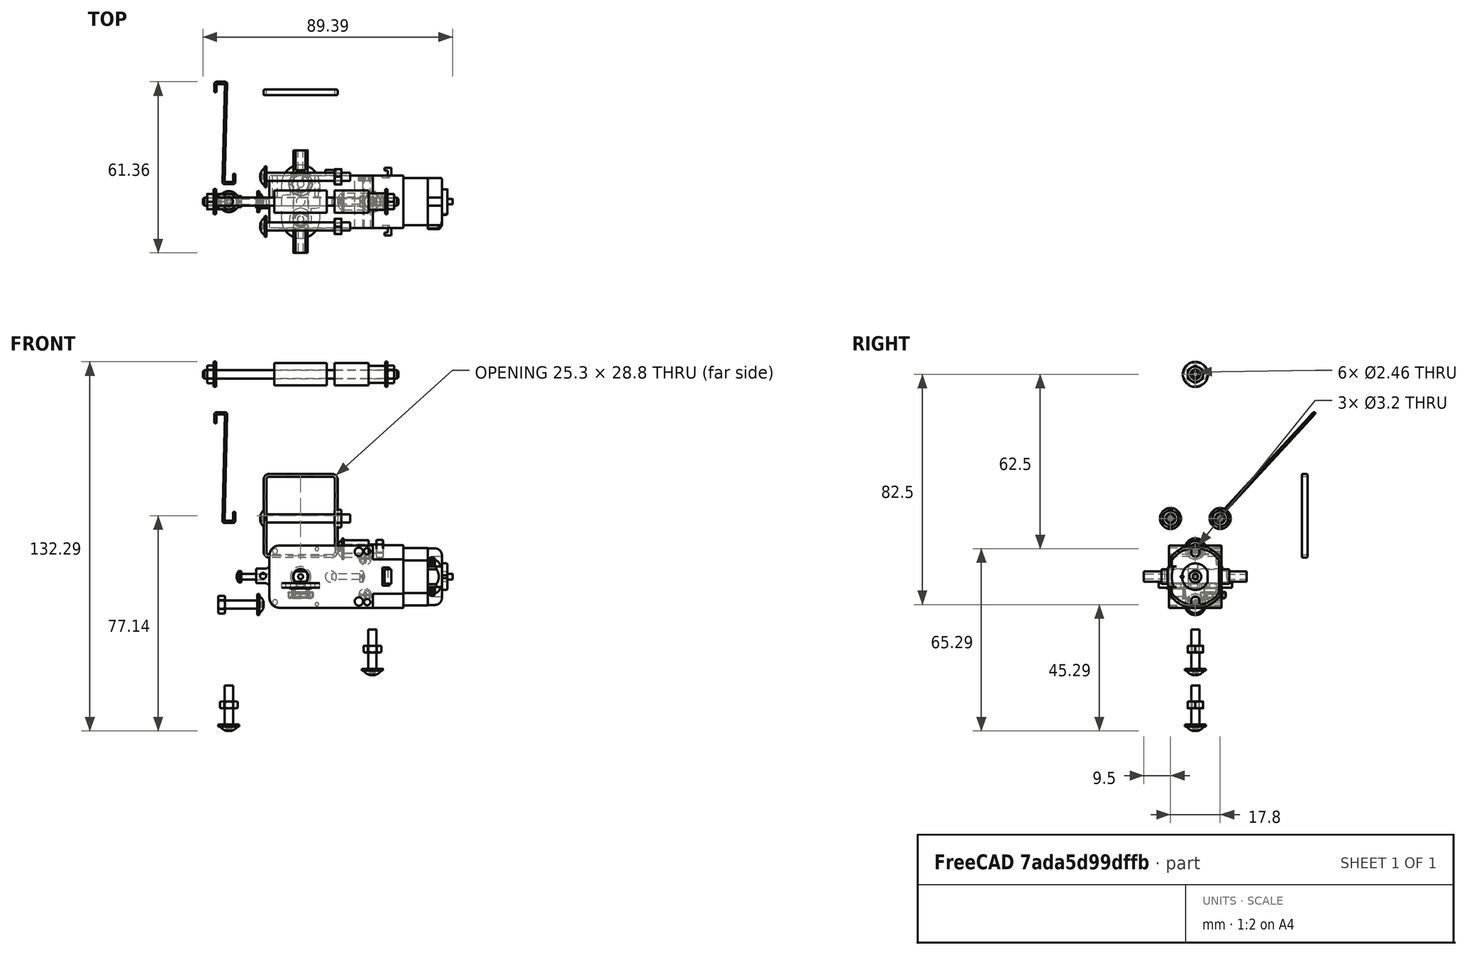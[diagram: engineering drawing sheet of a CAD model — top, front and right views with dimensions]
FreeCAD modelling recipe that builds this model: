
FCSTD DOCUMENT  (FreeCAD 0.21R33771 (Git))
Label: walking_robot_05_false_color
License: CERN Open Hardware Licence permissive
LicenseURL: https://cern-ohl.web.cern.ch/
objects: PartDesign::Body×27, PartDesign::SubShapeBinder×26, Sketcher::SketchObject×22, Part::FeaturePython×19, Part::Part2DObjectPython×19, PartDesign::Pad×15, PartDesign::FeatureBase×12, Part::Feature×10, PartDesign::Plane×7, App::DocumentObjectGroup×5, TechDraw::DrawViewDimension×5, PartDesign::FeaturePython×4, PartDesign::Fillet×3, Spreadsheet::Sheet×2, PartDesign::CoordinateSystem×2, Part::Box×2, Part::Cut×2, App::Part×2, PartDesign::Pocket×2, PartDesign::AdditivePipe×1, +4 more types
note: 199 computed .brp shape members not serialized (recipe doc carries the construction recipe); baked Part::Feature solids carry a one-line shape summary decoded from their .brp

FEATURE [Spreadsheet::Sheet] Spreadsheet
  cells = A1='acrylic_thick; B1(acrylic_thick)==4.9 mm; A2='acrylic_thin; B2(acrylic_thin)=2.8; A3='cam_length; B3(cam_length)=10; A4='angle; B4(angle)=270
FEATURE [Part::Feature] Compound002  label="motoreducteur001"
  Placement = pos=(25.85,-9.4,11.15) rot=(-1,0,0;1.5708rad)
  shape: bbox 70.34 x 38.2 x 22.5 mm, 234 faces, 3 solids (baked)
FEATURE [PartDesign::CoordinateSystem] Local_CS002
  AttacherType = Attacher::AttachEngine3D
  AttachmentOffset = pos=(0,0,0) rot=(0,-1,0;1.5708rad)
  MapMode = 11
  Placement = pos=(-2.8e-15,-19.1,1.8e-15) rot=(0,0,-1;1.5708rad)
  Support = -> [Compound002]
FEATURE [PartDesign::CoordinateSystem] Local_CS003
  AttacherType = Attacher::AttachEngine3D
  AttachmentOffset = pos=(0,0,0) rot=(0,1,0;1.5708rad)
  MapMode = 11
  Placement = pos=(-2.8e-15,19.1,1.9e-15) rot=(0,0,1;4.71239rad)
  Support = -> [Compound002]
FEATURE [PartDesign::SubShapeBinder] Binder
  BindCopyOnChange = 0
  BindMode = 0
  ClaimChildren = false
  Context = -> Body [Binder.]
  Fuse = false
  MakeFace = true
  OffsetFill = false
  OffsetIntersection = false
  OffsetJoinType = 0
  OffsetOpenResult = false
  PartialLoad = false
  Relative = true
  Support = -> [Part001]
  _Version = 2
FEATURE [Sketcher::SketchObject] Sketch
  ExternalGeometry = -> [Binder]
  FullyConstrained = true
  MapMode = 5
  Placement = pos=(-18.4,0,0) rot=(0.57735,-0.57735,-0.57735;2.0944rad)
  Support = -> [Binder]
  expr: Constraints[38] = Spreadsheet.cam_length
  expr: Constraints[81] = Spreadsheet.angle
  sketch-geometry (37):
    g0: ArcOfCircle CenterX=3.55 CenterY=5 CenterZ=0 NormalX=0 NormalY=0 NormalZ=1 AngleXU=0 Radius=0.4 StartAngle=0 EndAngle=3.14159
    g1: ArcOfCircle CenterX=3.55 CenterY=-5 CenterZ=0 NormalX=0 NormalY=0 NormalZ=1 AngleXU=0 Radius=0.4 StartAngle=3.14159 EndAngle=6.28319
    g2: LineSegment StartX=3.15 StartY=5 StartZ=0 EndX=3.15 EndY=-5 EndZ=0
    g3: LineSegment StartX=3.95 StartY=-5 StartZ=0 EndX=3.95 EndY=5 EndZ=0
    g4: ArcOfCircle CenterX=-3.55 CenterY=5 CenterZ=0 NormalX=0 NormalY=0 NormalZ=1 AngleXU=0 Radius=0.4 StartAngle=3e-16 EndAngle=3.14159
    g5: ArcOfCircle CenterX=-3.55 CenterY=-5 CenterZ=0 NormalX=0 NormalY=0 NormalZ=1 AngleXU=0 Radius=0.4 StartAngle=3.14159 EndAngle=6.28319
    g6: LineSegment StartX=-3.15 StartY=-5 StartZ=0 EndX=-3.15 EndY=5 EndZ=0
    g7: LineSegment StartX=3.55 StartY=5 StartZ=0 EndX=3.55 EndY=-5 EndZ=0
    g8: LineSegment StartX=-3.55 StartY=5 StartZ=0 EndX=-3.55 EndY=-5 EndZ=0
    g9: ArcOfCircle CenterX=1.55 CenterY=5 CenterZ=0 NormalX=0 NormalY=0 NormalZ=1 AngleXU=0 Radius=0.2 StartAngle=0 EndAngle=3.14159
    g10: ArcOfCircle CenterX=1.55 CenterY=-5 CenterZ=0 NormalX=0 NormalY=0 NormalZ=1 AngleXU=0 Radius=0.2 StartAngle=3.14159 EndAngle=6.28319
    g11: LineSegment StartX=1.35 StartY=5 StartZ=0 EndX=1.35 EndY=2.16333 EndZ=0
    g12: LineSegment StartX=1.75 StartY=-5 StartZ=0 EndX=1.75 EndY=5 EndZ=0
    g13: ArcOfCircle CenterX=-1.55 CenterY=5 CenterZ=0 NormalX=0 NormalY=0 NormalZ=1 AngleXU=0 Radius=0.2 StartAngle=5e-16 EndAngle=3.14159
    g14: ArcOfCircle CenterX=-1.55 CenterY=-5 CenterZ=0 NormalX=0 NormalY=0 NormalZ=1 AngleXU=0 Radius=0.2 StartAngle=3.14159 EndAngle=6.28319
    g15: LineSegment StartX=-1.75 StartY=5 StartZ=0 EndX=-1.75 EndY=-5 EndZ=0
    g16: LineSegment StartX=-1.35 StartY=-5 StartZ=0 EndX=-1.35 EndY=-2.16333 EndZ=0
    g17: LineSegment StartX=1.55 StartY=5 StartZ=0 EndX=1.55 EndY=-5 EndZ=0
    g18: LineSegment StartX=-1.55 StartY=5 StartZ=0 EndX=-1.55 EndY=-5 EndZ=0
    g19: LineSegment StartX=3.55 StartY=-4.2e-15 StartZ=0 EndX=1.55 EndY=-3.8e-15 EndZ=0
    g20: ArcOfCircle CenterX=9.6e-15 CenterY=5 CenterZ=0 NormalX=0 NormalY=0 NormalZ=1 AngleXU=0 Radius=7.5 StartAngle=0 EndAngle=3.14159
    g21: ArcOfCircle CenterX=6.9e-15 CenterY=-10 CenterZ=0 NormalX=0 NormalY=0 NormalZ=1 AngleXU=0 Radius=7.5 StartAngle=3.14159 EndAngle=6.28319
    g22: LineSegment StartX=-7.5 StartY=5 StartZ=0 EndX=-7.5 EndY=-10 EndZ=0
    g23: LineSegment StartX=7.5 StartY=-10 StartZ=0 EndX=7.5 EndY=5 EndZ=0
    g24: LineSegment StartX=8.7e-15 StartY=-3.6e-15 StartZ=0 EndX=9.6e-15 EndY=5 EndZ=0
    g25: LineSegment StartX=8.7e-15 StartY=-3.6e-15 StartZ=0 EndX=6.9e-15 EndY=-10 EndZ=0
    g26: Circle CenterX=6.9e-15 CenterY=-10 CenterZ=0 NormalX=0 NormalY=0 NormalZ=1 AngleXU=0 Radius=3.1
    g27: LineSegment StartX=-3.95 StartY=-5 StartZ=0 EndX=-3.95 EndY=5 EndZ=0
    g28: LineSegment StartX=1.55 StartY=-3.8e-15 StartZ=0 EndX=8.7e-15 EndY=-3.6e-15 EndZ=0
    g29: Circle CenterX=8.7e-15 CenterY=-3.6e-15 CenterZ=0 NormalX=0 NormalY=0 NormalZ=1 AngleXU=0 Radius=1.75
    g30: LineSegment StartX=-1.75 StartY=-4.1e-15 StartZ=0 EndX=-1.85 EndY=-4.1e-15 EndZ=0
    g31: LineSegment StartX=-3.55 StartY=-2.9e-15 StartZ=0 EndX=-1.55 EndY=-3.3e-15 EndZ=0
    g32: LineSegment StartX=8.7e-15 StartY=-3.6e-15 StartZ=0 EndX=-1.55 EndY=-3.3e-15 EndZ=0
    g33: LineSegment StartX=-1.35 StartY=2.16333 StartZ=0 EndX=-1.35 EndY=5 EndZ=0
    g34: LineSegment StartX=1.35 StartY=-2.16333 StartZ=0 EndX=1.35 EndY=-5 EndZ=0
    g35: ArcOfCircle CenterX=8.7e-15 CenterY=-3.6e-15 CenterZ=0 NormalX=0 NormalY=0 NormalZ=1 AngleXU=0 Radius=2.55 StartAngle=1.01289 EndAngle=2.1287
    g36: ArcOfCircle CenterX=8.7e-15 CenterY=-3.6e-15 CenterZ=0 NormalX=0 NormalY=0 NormalZ=1 AngleXU=0 Radius=2.55 StartAngle=4.15448 EndAngle=5.2703
  constraints (89):
    c: Tangent(g0,g2) = -1.5708
    c: Tangent(g2,g1) = -1.5708
    c: Tangent(g1,g3) = -1.5708
    c: Tangent(g5,g6) = -1.5708
    c: Tangent(g6,g4) = -1.5708
    c: Radius(g0) = 0.4
    c: Coincident(g7,g0)
    c: Coincident(g7,g1)
    c: Coincident(g8,g4)
    c: Coincident(g8,g5)
    c: Equal(g7,g8)
    c: Distance(g7) = 10
    c: Tangent(g9,g11) = -1.5708
    c: Tangent(g10,g12) = -1.5708
    c: Tangent(g12,g9) = -1.5708
    c: Tangent(g13,g15) = -1.5708
    c: Tangent(g15,g14) = -1.5708
    c: Tangent(g14,g16) = -1.5708
    c: Coincident(g17,g9)
    c: Coincident(g17,g10)
    c: Coincident(g18,g13)
    c: Coincident(g18,g14)
    c: Equal(g17,g7)
    c: Equal(g8,g18)
    c: Symmetric(g10,g9,g19)
    c: Distance(g19) = 2
    c: Perpendicular(g7,g19)
    c: Parallel(g17,g7)
    c: Parallel(g18,g8)
    c: Tangent(g20,g22) = -1.5708
    c: Tangent(g22,g21) = -1.5708
    c: Tangent(g21,g23) = -1.5708
    c: Tangent(g23,g20) = -1.5708
    c: Equal(g20,g21)
    c: Coincident(g24,g20)
    c: Coincident(g25,g21)
    c: Diameter(g20) = 15
    c: Distance(g24) = 5
    c: Distance(g25) = 10
    c: Coincident(g26,g21)
    c: Diameter(g26) = 6.2
    c: Tangent(g27,g4) = 1.5708
    c: Tangent(g27,g5) = 1.5708
    c: Symmetric(g0,g1,g19)
    c: Coincident(g28,g19)
    c: Parallel(g28,g19)
    c: Perpendicular(g28,g24)
    c: Tangent(g0,g3) = -1.5708
    c: PointOnObject(g30,g29)
    c: Horizontal(g30)
    c: Symmetric(g-5,g-5,g30)
    c: DistanceX(g30,g30) = 0.1
    c: Perpendicular(g25,g28)
    c: Symmetric(g14,g13,g31)
    c: Symmetric(g5,g4,g31)
    c: Equal(g31,g19)
    c: Coincident(g32,g31)
    c: Equal(g28,g32)
    c: Perpendicular(g32,g24)
    c: Perpendicular(g32,g18)
    c: Perpendicular(g18,g31)
    c: Tangent(g15,g29)
    c: PointOnObject(g34,g11)
    c: PointOnObject(g33,g-3)
    c: Parallel(g33,g17)
    c: Parallel(g17,g34)
    c: Tangent(g33,g13) = -1.5708
    c: Tangent(g34,g10) = -1.5708
    c: Coincident(g25,g32)
    c: Coincident(g25,g24)
    c: Coincident(g25,g28)
    c: Coincident(g24,g29)
    c: Coincident(g35,g24)
    c: Coincident(g35,g33)
    c: Coincident(g35,g11)
    c: Coincident(g36,g35)
    c: Coincident(g36,g34)
    c: Equal(g36,g-4)
    c: Coincident(g16,g36)
    c: Parallel(g16,g18)
    c: Coincident(g35,g-4)
    c: Angle(g25) = 4.71239
    c: Equal(g5,g1)
    c: Equal(g1,g4)
    c: Equal(g4,g0)
    c: Equal(g13,g9)
    c: Equal(g9,g14)
    c: Equal(g14,g10)
    c: Radius(g9) = 0.2
FEATURE [PartDesign::SubShapeBinder] Binder001
  BindCopyOnChange = 0
  BindMode = 0
  ClaimChildren = false
  Context = -> Body002 [Binder001.]
  Fuse = false
  MakeFace = true
  OffsetFill = false
  OffsetIntersection = false
  OffsetJoinType = 0
  OffsetOpenResult = false
  PartialLoad = false
  Relative = true
  Support = -> [Part001]
  _Version = 2
FEATURE [Part::Box] Box  label="Cube"
  AttacherType = Attacher::AttachEngine3D
  Height = 10
  Length = 10
  Placement = pos=(-5,18.4,-5) rot=(0,0,1;0rad)
  Width = 10
FEATURE [Part::Box] Box001  label="Cube001"
  AttacherType = Attacher::AttachEngine3D
  Height = 10
  Length = 10
  Placement = pos=(-5,-28.4,-5) rot=(0,0,1;0rad)
  Width = 10
FEATURE [Part::Cut] Cut
  Base = -> Compound002
  Tool = -> Box
FEATURE [Part::Cut] Cut001
  Base = -> Cut
  Tool = -> Box001
FEATURE [App::Part] Part001  label="Motor"
  Group = -> [Box001,Compound002,Local_CS002,Local_CS003,Box,Cut,Cut001]
  Origin = -> Origin004
  Placement = pos=(0,0,0) rot=(-0.57735,0.57735,-0.57735;4.18879rad)
FEATURE [PartDesign::Pad] Pad
  Direction = (-1,2e-16,-2e-16)
  Length = 2.8
  Length2 = 10
  Profile = -> Sketch
  ReferenceAxis = -> Sketch [N_Axis]
  Reversed = true
  Type = 0
  expr: Length = Spreadsheet.acrylic_thin
FEATURE [PartDesign::Body] Body  label="cam_right_1"
  Group = -> [Sketch,Binder,Pad]
  Origin = -> Origin001
  Tip = -> Pad
FEATURE [PartDesign::SubShapeBinder] Binder002
  BindCopyOnChange = 0
  BindMode = 0
  ClaimChildren = false
  Context = -> Body003 [Binder002.]
  Fuse = false
  MakeFace = true
  OffsetFill = false
  OffsetIntersection = false
  OffsetJoinType = 0
  OffsetOpenResult = false
  PartialLoad = false
  Relative = true
  Support = -> [Body]
  _Version = 2
FEATURE [PartDesign::Plane] DatumPlane001
  AttachmentOffset = pos=(0,0,0.1) rot=(0,0,1;0rad)
  Length = 60
  MapMode = 5
  Placement = pos=(-18.5,5.2e-15,-3.9e-15) rot=(-0.57735,0.57735,0.57735;4.18879rad)
  ResizeMode = 0
  Support = -> [Binder002]
  Width = 60
FEATURE [Sketcher::SketchObject] Sketch002
  ExternalGeometry = -> [Binder002]
  FullyConstrained = true
  MapMode = 5
  Placement = pos=(-18.5,5.2e-15,-3.9e-15) rot=(-0.57735,0.57735,0.57735;4.18879rad)
  Support = -> [DatumPlane001]
  sketch-geometry (6):
    g0: ArcOfCircle CenterX=-1.6948e-12 CenterY=5 CenterZ=0 NormalX=0 NormalY=0 NormalZ=1 AngleXU=0 Radius=7.5 StartAngle=2.58e-13 EndAngle=3.14159
    g1: ArcOfCircle CenterX=2.174e-12 CenterY=-10 CenterZ=0 NormalX=0 NormalY=0 NormalZ=1 AngleXU=0 Radius=7.5 StartAngle=3.14159 EndAngle=6.28319
    g2: LineSegment StartX=-7.5 StartY=5 StartZ=0 EndX=-7.5 EndY=-10 EndZ=0
    g3: LineSegment StartX=7.5 StartY=-10 StartZ=0 EndX=7.5 EndY=5 EndZ=0
    g4: Circle CenterX=2.174e-12 CenterY=-10 CenterZ=0 NormalX=0 NormalY=0 NormalZ=1 AngleXU=0 Radius=3.1
    g5: Circle CenterX=0 CenterY=0 CenterZ=0 NormalX=0 NormalY=0 NormalZ=1 AngleXU=0 Radius=1
  constraints (12):
    c: Tangent(g0,g2) = -1.5708
    c: Tangent(g2,g1) = -1.5708
    c: Tangent(g1,g3) = -1.5708
    c: Tangent(g3,g0) = -1.5708
    c: Equal(g0,g1)
    c: Coincident(g0,g-3)
    c: Coincident(g1,g-5)
    c: Equal(g0,g-3)
    c: Coincident(g4,g1)
    c: Equal(g4,g-5)
    c: Coincident(g5,g-6)
    c: Diameter(g5) = 2
FEATURE [PartDesign::Pad] Pad002
  Direction = (-1,2e-16,-2e-16)
  Length = 2.8
  Length2 = 10
  Placement = pos=(-18.5,5e-15,-4e-15) rot=(0.57735,-0.57735,-0.57735;2.0944rad)
  Profile = -> Sketch002
  ReferenceAxis = -> Sketch002 [N_Axis]
  Type = 0
  expr: Length = Spreadsheet.acrylic_thin
FEATURE [PartDesign::Body] Body003  label="cam_right_2"
  Group = -> [Binder002,DatumPlane001,Sketch002,Pad002]
  Origin = -> Origin
  Tip = -> Pad002
FEATURE [PartDesign::SubShapeBinder] Binder003
  BindCopyOnChange = 0
  BindMode = 0
  ClaimChildren = false
  Context = -> Body004 [Binder003.]
  Fuse = false
  MakeFace = true
  OffsetFill = false
  OffsetIntersection = false
  OffsetJoinType = 0
  OffsetOpenResult = false
  PartialLoad = false
  Relative = true
  Support = -> [Body003]
  _Version = 2
FEATURE [PartDesign::Plane] DatumPlane002
  AttachmentOffset = pos=(0,0,0.1) rot=(0,0,1;0rad)
  Length = 60
  MapMode = 5
  Placement = pos=(-21.4,5.3e-15,-1.05e-14) rot=(-0.57735,0.57735,0.57735;4.18879rad)
  ResizeMode = 0
  Support = -> [Binder003]
  Width = 60
FEATURE [Sketcher::SketchObject] Sketch003
  ExternalGeometry = -> [Binder003]
  FullyConstrained = true
  MapMode = 5
  Placement = pos=(-21.4,5.3e-15,-1.05e-14) rot=(-0.57735,0.57735,0.57735;4.18879rad)
  Support = -> [DatumPlane002]
  sketch-geometry (6):
    g0: ArcOfCircle CenterX=-1.6956e-12 CenterY=5 CenterZ=0 NormalX=0 NormalY=0 NormalZ=1 AngleXU=0 Radius=7.5 StartAngle=2.581e-13 EndAngle=3.14159
    g1: ArcOfCircle CenterX=2.1765e-12 CenterY=-10 CenterZ=0 NormalX=0 NormalY=0 NormalZ=1 AngleXU=0 Radius=7.5 StartAngle=3.14159 EndAngle=6.28319
    g2: LineSegment StartX=-7.5 StartY=5 StartZ=0 EndX=-7.5 EndY=-10 EndZ=0
    g3: LineSegment StartX=7.5 StartY=-10 StartZ=0 EndX=7.5 EndY=5 EndZ=0
    g4: Circle CenterX=2.1765e-12 CenterY=-10 CenterZ=0 NormalX=0 NormalY=0 NormalZ=1 AngleXU=0 Radius=3.1
    g5: Circle CenterX=0 CenterY=0 CenterZ=0 NormalX=0 NormalY=0 NormalZ=1 AngleXU=0 Radius=3
  constraints (12):
    c: Tangent(g0,g2) = -1.5708
    c: Tangent(g2,g1) = -1.5708
    c: Tangent(g1,g3) = -1.5708
    c: Tangent(g3,g0) = -1.5708
    c: Equal(g0,g1)
    c: Coincident(g0,g-3)
    c: Coincident(g1,g-5)
    c: Equal(g0,g-3)
    c: Coincident(g4,g1)
    c: Equal(g4,g-5)
    c: Coincident(g5,g-6)
    c: Diameter(g5) = 6
FEATURE [PartDesign::Pad] Pad003
  Direction = (-1,3e-16,-3e-16)
  Length = 2.8
  Length2 = 10
  Placement = pos=(-21.4,5e-15,-1e-14) rot=(0.57735,-0.57735,-0.57735;2.0944rad)
  Profile = -> Sketch003
  ReferenceAxis = -> Sketch003 [N_Axis]
  Type = 0
  expr: Length = Spreadsheet.acrylic_thin
FEATURE [PartDesign::Body] Body004  label="cam_right_3"
  Group = -> [Binder003,DatumPlane002,Sketch003,Pad003]
  Origin = -> Origin005
  Tip = -> Pad003
FEATURE [PartDesign::SubShapeBinder] Binder004
  BindCopyOnChange = 0
  BindMode = 0
  ClaimChildren = false
  Context = -> Body002 [Binder004.]
  Fuse = false
  MakeFace = true
  OffsetFill = false
  OffsetIntersection = false
  OffsetJoinType = 0
  OffsetOpenResult = false
  PartialLoad = false
  Relative = true
  Support = -> [Body004]
  _Version = 2
FEATURE [PartDesign::Plane] DatumPlane003
  AttachmentOffset = pos=(0,0,0.1) rot=(0,0,1;0rad)
  Length = 66.5529
  MapMode = 5
  Placement = pos=(-24.3,8.3e-15,-1.41e-14) rot=(-0.57735,0.57735,0.57735;4.18879rad)
  ResizeMode = 0
  Support = -> [Binder004]
  Width = 153.553
FEATURE [Sketcher::SketchObject] Sketch001
  ExternalGeometry = -> [Binder004]
  FullyConstrained = false
  MapMode = 5
  Placement = pos=(-24.3,8.3e-15,-1.41e-14) rot=(-0.57735,0.57735,0.57735;4.18879rad)
  Support = -> [DatumPlane003]
  expr: Constraints[92] = Spreadsheet.angle
  expr: Constraints[98] = Spreadsheet.acrylic_thin
  sketch-geometry (38):
    g0: LineSegment StartX=-10 StartY=84 StartZ=0 EndX=10 EndY=84 EndZ=0
    g1: LineSegment StartX=10 StartY=84 StartZ=0 EndX=10 EndY=-53 EndZ=0
    g2: LineSegment StartX=10 StartY=-53 StartZ=0 EndX=-10 EndY=-53 EndZ=0
    g3: LineSegment StartX=-10 StartY=-53 StartZ=0 EndX=-10 EndY=84 EndZ=0
    g4: LineSegment StartX=4e-15 StartY=-10 StartZ=0 EndX=-10 EndY=-10 EndZ=0
    g5: LineSegment StartX=4e-15 StartY=-10 StartZ=0 EndX=10 EndY=-10 EndZ=0
    g6: ArcOfCircle CenterX=-2e-16 CenterY=75 CenterZ=0 NormalX=0 NormalY=0 NormalZ=1 AngleXU=0 Radius=3.1 StartAngle=2e-16 EndAngle=3.14159
    g7: ArcOfCircle CenterX=6e-16 CenterY=50 CenterZ=0 NormalX=0 NormalY=0 NormalZ=1 AngleXU=0 Radius=3.1 StartAngle=3.14159 EndAngle=6.28319
    g8: LineSegment StartX=-3.1 StartY=75 StartZ=0 EndX=-3.1 EndY=50 EndZ=0
    g9: LineSegment StartX=3.1 StartY=50 StartZ=0 EndX=3.1 EndY=75 EndZ=0
    g10: LineSegment StartX=-2e-16 StartY=75 StartZ=0 EndX=-4e-16 EndY=84 EndZ=0
    g11: Circle CenterX=4e-15 CenterY=-10 CenterZ=0 NormalX=0 NormalY=0 NormalZ=1 AngleXU=0 Radius=1.55
    g12: LineSegment StartX=0 StartY=0 StartZ=0 EndX=4e-15 EndY=-10 EndZ=0
    g13: Circle CenterX=0 CenterY=71 CenterZ=0 NormalX=0 NormalY=0 NormalZ=1 AngleXU=0 Radius=3.1
    g14: LineSegment StartX=0 StartY=71 StartZ=0 EndX=0 EndY=0 EndZ=0
    g15: LineSegment StartX=6e-16 StartY=50 StartZ=0 EndX=1e-16 EndY=62.5 EndZ=0
    g16: LineSegment StartX=-2e-16 StartY=75 StartZ=0 EndX=1e-16 EndY=62.5 EndZ=0
    g17: LineSegment StartX=-10 StartY=-53 StartZ=0 EndX=-6 EndY=-53 EndZ=0
    g18: LineSegment StartX=-6 StartY=-53 StartZ=0 EndX=-6 EndY=-50.2 EndZ=0
    g19: LineSegment StartX=-6 StartY=-50.2 StartZ=0 EndX=-1.25 EndY=-50.2 EndZ=0
    g20: LineSegment StartX=-1.25 StartY=-50.2 StartZ=0 EndX=-1.25 EndY=-47.2 EndZ=0
    g21: LineSegment StartX=-1.25 StartY=-47.2 StartZ=0 EndX=-2.75 EndY=-47.2 EndZ=0
    g22: LineSegment StartX=-2.75 StartY=-47.2 StartZ=0 EndX=-2.75 EndY=-44.7 EndZ=0
    g23: LineSegment StartX=-2.75 StartY=-44.7 StartZ=0 EndX=-1.25 EndY=-44.7 EndZ=0
    g24: LineSegment StartX=-1.25 StartY=-44.7 StartZ=0 EndX=-1.25 EndY=-37.7 EndZ=0
    g25: LineSegment StartX=-1.25 StartY=-37.7 StartZ=0 EndX=1.25 EndY=-37.7 EndZ=0
    g26: LineSegment StartX=1.25 StartY=-37.7 StartZ=0 EndX=1.25 EndY=-44.7 EndZ=0
    g27: LineSegment StartX=1.25 StartY=-44.7 StartZ=0 EndX=2.75 EndY=-44.7 EndZ=0
    g28: LineSegment StartX=2.75 StartY=-44.7 StartZ=0 EndX=2.75 EndY=-47.2 EndZ=0
    g29: LineSegment StartX=2.75 StartY=-47.2 StartZ=0 EndX=1.25 EndY=-47.2 EndZ=0
    g30: LineSegment StartX=1.25 StartY=-47.2 StartZ=0 EndX=1.25 EndY=-50.2 EndZ=0
    g31: LineSegment StartX=1.25 StartY=-50.2 StartZ=0 EndX=6 EndY=-50.2 EndZ=0
    g32: LineSegment StartX=6 StartY=-50.2 StartZ=0 EndX=6 EndY=-53 EndZ=0
    g33: LineSegment StartX=6 StartY=-53 StartZ=0 EndX=10 EndY=-53 EndZ=0
    g34: LineSegment StartX=-7 StartY=-10 StartZ=0 EndX=-7 EndY=20 EndZ=0
    g35: LineSegment StartX=7 StartY=20 StartZ=0 EndX=7 EndY=-10 EndZ=0
    g36: Circle CenterX=-7 CenterY=20 CenterZ=0 NormalX=0 NormalY=0 NormalZ=1 AngleXU=0 Radius=0.6
    g37: Circle CenterX=7 CenterY=20 CenterZ=0 NormalX=0 NormalY=0 NormalZ=1 AngleXU=0 Radius=0.6
  constraints (105):
    c: Coincident(g0,g1)
    c: Coincident(g1,g2)
    c: Coincident(g2,g3)
    c: Coincident(g3,g0)
    c: Distance(g0) = 20
    c: Perpendicular(g3,g0)
    c: Perpendicular(g1,g2)
    c: Perpendicular(g2,g3)
    c: PointOnObject(g4,g3)
    c: PointOnObject(g5,g1)
    c: Perpendicular(g1,g5)
    c: Perpendicular(g3,g4)
    c: Equal(g4,g5)
    c: Distance(g3) = 137
    c: Tangent(g6,g8) = -1.5708
    c: Tangent(g8,g7) = -1.5708
    c: Tangent(g7,g9) = -1.5708
    c: Tangent(g9,g6) = -1.5708
    c: Equal(g6,g7)
    c: Diameter(g7) = 6.2
    c: Distance(g6,g7) = 25
    c: Coincident(g10,g6)
    c: Perpendicular(g0,g10)
    c: Distance(g10) = 9
    c: Symmetric(g0,g0,g10)
    c: Parallel(g8,g3)
    c: Diameter(g11) = 3.1
    c: Coincident(g14,g13)
    c: DistanceY(g14,g14) = 71
    c: Coincident(g14,g12)
    c: Coincident(g15,g7)
    c: Coincident(g16,g6)
    c: Coincident(g16,g15)
    c: Equal(g16,g15)
    c: Parallel(g16,g8)
    c: Tangent(g13,g9)
    c: Vertical(g14)
    c: Coincident(g17,g3)
    c: Coincident(g17,g18)
    c: Coincident(g18,g19)
    c: Coincident(g19,g20)
    c: Coincident(g20,g21)
    c: Coincident(g21,g22)
    c: Coincident(g22,g23)
    c: Coincident(g23,g24)
    c: Coincident(g24,g25)
    c: Coincident(g25,g26)
    c: Coincident(g26,g27)
    c: Coincident(g27,g28)
    c: Coincident(g28,g29)
    c: Coincident(g29,g30)
    c: Coincident(g30,g31)
    c: Coincident(g31,g32)
    c: Coincident(g32,g33)
    c: Coincident(g33,g1)
    c: Perpendicular(g17,g3)
    c: Perpendicular(g33,g1)
    c: Perpendicular(g32,g33)
    c: Perpendicular(g17,g18)
    c: Perpendicular(g19,g18)
    c: Perpendicular(g32,g31)
    c: Perpendicular(g31,g30)
    c: Perpendicular(g19,g20)
    c: Perpendicular(g29,g30)
    c: Perpendicular(g20,g21)
    c: Perpendicular(g28,g29)
    c: Perpendicular(g22,g21)
    c: Perpendicular(g28,g27)
    c: Perpendicular(g23,g22)
    c: Perpendicular(g27,g26)
    c: Perpendicular(g24,g23)
    c: Equal(g18,g32)
    c: Equal(g30,g20)
    c: Equal(g29,g21)
    c: Equal(g23,g27)
    c: Equal(g19,g31)
    c: Distance(g22,g27) = 5.5
    c: Equal(g25,g22)
    c: Equal(g22,g28)
    c: Distance(g24) = 7
    c: Perpendicular(g25,g26)
    c: Equal(g21,g23)
    c: PointOnObject(g34,g4)
    c: Equal(g34,g35)
    c: Distance(g34,g4) = 3
    c: Coincident(g36,g34)
    c: Coincident(g37,g35)
    c: Equal(g37,g36)
    c: Diameter(g37) = 1.2
    c: Distance(g34) = 30
    c: Perpendicular(g5,g35)
    c: Perpendicular(g4,g34)
    c: Angle(g12) = 4.71239
    c: Equal(g17,g33)
    c: Distance(g17) = 4
    c: DistanceY(g3,g12) = 53
    c: Coincident(g12,g-1)
    c: DistanceY(g22,g22) = 2.5
    c: DistanceY(g18,g18) = 2.8
    c: DistanceY(g20,g20) = 3
    c: Equal(g7,g13)
    c: Coincident(g4,g5)
    c: Coincident(g4,g12)
    c: Coincident(g4,g-3)
    c: Coincident(g4,g11)
FEATURE [PartDesign::Pad] Pad004
  Direction = (-1,5e-16,-5e-16)
  Length = 2.8
  Length2 = 10
  Placement = pos=(-24.3,8e-15,-1.4e-14) rot=(0.57735,-0.57735,-0.57735;2.0944rad)
  Profile = -> Sketch001
  ReferenceAxis = -> Sketch001 [N_Axis]
  Type = 0
  expr: Length = Spreadsheet.acrylic_thin
FEATURE [PartDesign::SubShapeBinder] Binder005
  BindCopyOnChange = 0
  BindMode = 0
  ClaimChildren = false
  Context = -> Body005 [Binder005.]
  Fuse = false
  MakeFace = true
  OffsetFill = false
  OffsetIntersection = false
  OffsetJoinType = 0
  OffsetOpenResult = false
  PartialLoad = false
  Relative = true
  Support = -> [Body004]
  _Version = 2
FEATURE [Part::FeaturePython] Screw  label="M3x14-Screw"  # Fasteners workbench fastener (typed FeaturePython)
  Placement = pos=(-15.5,7.6099e-12,-10) rot=(0,1,0;1.5708rad)
  diameter = 1
  invert = false
  leftHanded = false
  length = 6
  lengthCustom = 14
  matchOuter = false
  offset = 0
  thread = false
  type = 25
FEATURE [Part::FeaturePython] Nut  label="M3-Nut"  # Fasteners workbench fastener (typed FeaturePython)
  Placement = pos=(-29.5,7.6239e-12,-10) rot=(0,1,0;1.5708rad)
  baseObject = -> Screw [Edge71]
  diameter = 4
  invert = false
  leftHanded = false
  matchOuter = false
  offset = 0
  thread = false
  type = 25
FEATURE [PartDesign::SubShapeBinder] Binder008
  BindCopyOnChange = 0
  BindMode = 0
  ClaimChildren = false
  Context = -> Body005 [Binder008.]
  Fuse = false
  MakeFace = true
  OffsetFill = false
  OffsetIntersection = false
  OffsetJoinType = 0
  OffsetOpenResult = false
  PartialLoad = false
  Relative = true
  Support = -> [Body002[Pad004.]]
  _Version = 2
FEATURE [Sketcher::SketchObject] Sketch004
  ExternalGeometry = -> [Binder005]
  FullyConstrained = true
  MapMode = 5
  Placement = pos=(-24.3,-1.36e-14,-3.65e-14) rot=(0.57735,0.57735,0.57735;2.0944rad)
  Support = -> [Binder008]
  sketch-geometry (2):
    g0: Circle CenterX=-2.172e-12 CenterY=-10 CenterZ=0 NormalX=0 NormalY=0 NormalZ=1 AngleXU=0 Radius=3
    g1: Circle CenterX=-2.172e-12 CenterY=-10 CenterZ=0 NormalX=0 NormalY=0 NormalZ=1 AngleXU=0 Radius=1.6
  constraints (4):
    c: Diameter(g1) = 3.2
    c: Diameter(g0) = 6
    c: Coincident(g1,g-3)
    c: Coincident(g0,g1)
FEATURE [PartDesign::Pad] Pad005
  Direction = (1,0,4e-16)
  Length = 8.8
  Length2 = 10
  Profile = -> Sketch004
  ReferenceAxis = -> Sketch004 [N_Axis]
  Type = 0
FEATURE [PartDesign::Body] Body005  label="spacer_right"
  Group = -> [Binder005,Sketch004,Pad005,Binder008]
  Origin = -> Origin006
  Tip = -> Pad005
FEATURE [PartDesign::SubShapeBinder] Binder009
  BindCopyOnChange = 0
  BindMode = 0
  ClaimChildren = false
  Context = -> Body007 [Binder009.]
  Fuse = false
  MakeFace = true
  OffsetFill = false
  OffsetIntersection = false
  OffsetJoinType = 0
  OffsetOpenResult = false
  PartialLoad = false
  Relative = true
  Support = -> [Body002[Pad004.]]
  _Version = 2
FEATURE [PartDesign::Plane] DatumPlane
  Length = 74.3266
  MapMode = 5
  Placement = pos=(5.3e-14,-1.145e-13,-53) rot=(1,0,0;3.14159rad)
  ResizeMode = 0
  Support = -> [Binder009]
  Width = 119.627
FEATURE [Sketcher::SketchObject] Sketch006
  ExternalGeometry = -> [Binder009]
  FullyConstrained = true
  MapMode = 5
  Placement = pos=(5.3e-14,-1.145e-13,-53) rot=(0,0,1;3.14159rad)
  Support = -> [DatumPlane]
  sketch-geometry (51):
    g0: LineSegment StartX=-12.3 StartY=40 StartZ=0 EndX=25.7 EndY=40 EndZ=0
    g1: LineSegment StartX=25.7 StartY=40 StartZ=0 EndX=25.7 EndY=0 EndZ=0
    g2: LineSegment StartX=25.7 StartY=0 StartZ=0 EndX=25.7 EndY=-56 EndZ=0
    g3: LineSegment StartX=25.7 StartY=-56 StartZ=0 EndX=-12.3 EndY=-56 EndZ=0
    g4: ArcOfCircle CenterX=-12.3 CenterY=40 CenterZ=0 NormalX=0 NormalY=0 NormalZ=1 AngleXU=0 Radius=4 StartAngle=1.5708 EndAngle=4.71239
    g5: ArcOfCircle CenterX=-12.3 CenterY=-56 CenterZ=0 NormalX=0 NormalY=0 NormalZ=1 AngleXU=0 Radius=4 StartAngle=1.5708 EndAngle=4.71239
    g6: LineSegment StartX=-12.3 StartY=44 StartZ=0 EndX=25.7 EndY=44 EndZ=0
    g7: LineSegment StartX=-12.3 StartY=36 StartZ=0 EndX=15.7 EndY=36 EndZ=0
    g8: LineSegment StartX=-12.3 StartY=-52 StartZ=0 EndX=15.7 EndY=-52 EndZ=0
    g9: LineSegment StartX=-12.3 StartY=-60 StartZ=0 EndX=25.7 EndY=-60 EndZ=0
    g10: ArcOfCircle CenterX=25.7 CenterY=10.1 CenterZ=0 NormalX=0 NormalY=0 NormalZ=1 AngleXU=0 Radius=8 StartAngle=0 EndAngle=0.895665
    g11: ArcOfCircle CenterX=25.7 CenterY=-9.9 CenterZ=0 NormalX=0 NormalY=0 NormalZ=1 AngleXU=0 Radius=8 StartAngle=3.14159 EndAngle=4.03726
    g12: LineSegment StartX=17.7 StartY=10.1 StartZ=0 EndX=17.7 EndY=-9.9 EndZ=0
    g13: LineSegment StartX=33.7 StartY=-9.9 StartZ=0 EndX=33.7 EndY=10.1 EndZ=0
    g14: LineSegment StartX=20.7 StartY=31 StartZ=0 EndX=20.7 EndY=16.345 EndZ=0
    g15: LineSegment StartX=30.7 StartY=16.345 StartZ=0 EndX=30.7 EndY=39 EndZ=0
    g16: ArcOfCircle CenterX=25.7 CenterY=39 CenterZ=0 NormalX=0 NormalY=0 NormalZ=1 AngleXU=0 Radius=5 StartAngle=0 EndAngle=1.5708
    g17: LineSegment StartX=20.7 StartY=-47 StartZ=0 EndX=20.7 EndY=-16.145 EndZ=0
    g18: LineSegment StartX=30.7 StartY=-16.145 StartZ=0 EndX=30.7 EndY=-55 EndZ=0
    g19: ArcOfCircle CenterX=25.7 CenterY=-55 CenterZ=0 NormalX=0 NormalY=0 NormalZ=1 AngleXU=0 Radius=5 StartAngle=4.71239 EndAngle=6.28319
    g20: ArcOfCircle CenterX=25.7 CenterY=-9.9 CenterZ=0 NormalX=0 NormalY=0 NormalZ=1 AngleXU=0 Radius=8 StartAngle=5.38752 EndAngle=6.28319
    g21: ArcOfCircle CenterX=25.7 CenterY=10.1 CenterZ=0 NormalX=0 NormalY=0 NormalZ=1 AngleXU=0 Radius=8 StartAngle=2.24593 EndAngle=3.14159
    g22: Circle CenterX=25.7 CenterY=0 CenterZ=0 NormalX=0 NormalY=0 NormalZ=1 AngleXU=0 Radius=1.55
    g23: LineSegment StartX=24.2 StartY=10.1 StartZ=0 EndX=27.2 EndY=10.1 EndZ=0
    g24: LineSegment StartX=27.2 StartY=10.1 StartZ=0 EndX=27.2 EndY=6.1 EndZ=0
    g25: LineSegment StartX=27.2 StartY=6.1 StartZ=0 EndX=24.2 EndY=6.1 EndZ=0
    g26: LineSegment StartX=24.2 StartY=6.1 StartZ=0 EndX=24.2 EndY=10.1 EndZ=0
    g27: LineSegment StartX=24.3 StartY=10 StartZ=0 EndX=24.3 EndY=10.1 EndZ=0
    g28: LineSegment StartX=24.3 StartY=10 StartZ=0 EndX=24.2 EndY=10 EndZ=0
    g29: LineSegment StartX=27.1 StartY=6 StartZ=0 EndX=27.2 EndY=6 EndZ=0
    g30: LineSegment StartX=27.1 StartY=6 StartZ=0 EndX=27.1 EndY=6.1 EndZ=0
    g31: LineSegment StartX=24.2 StartY=-5.9 StartZ=0 EndX=27.2 EndY=-5.9 EndZ=0
    g32: LineSegment StartX=27.2 StartY=-5.9 StartZ=0 EndX=27.2 EndY=-9.9 EndZ=0
    g33: LineSegment StartX=27.2 StartY=-9.9 StartZ=0 EndX=24.2 EndY=-9.9 EndZ=0
    g34: LineSegment StartX=24.2 StartY=-9.9 StartZ=0 EndX=24.2 EndY=-5.9 EndZ=0
    g35: LineSegment StartX=24.3 StartY=-6 StartZ=0 EndX=24.3 EndY=-5.9 EndZ=0
    g36: LineSegment StartX=24.3 StartY=-6 StartZ=0 EndX=24.2 EndY=-6 EndZ=0
    g37: LineSegment StartX=27.1 StartY=-10 StartZ=0 EndX=27.2 EndY=-10 EndZ=0
    g38: LineSegment StartX=27.1 StartY=-10 StartZ=0 EndX=27.1 EndY=-9.9 EndZ=0
    g39: ArcOfCircle CenterX=15.7 CenterY=-47 CenterZ=0 NormalX=0 NormalY=0 NormalZ=1 AngleXU=0 Radius=5 StartAngle=4.71239 EndAngle=6.28319
    g40: GeomPoint X=20.7 Y=-52 Z=0
    g41: ArcOfCircle CenterX=15.7 CenterY=31 CenterZ=0 NormalX=0 NormalY=0 NormalZ=1 AngleXU=0 Radius=5 StartAngle=0 EndAngle=1.5708
    g42: GeomPoint X=20.7 Y=36 Z=0
    g43: LineSegment StartX=24.2 StartY=10.1 StartZ=0 EndX=17.7 EndY=10.1 EndZ=0
    g44: LineSegment StartX=27.2 StartY=10.1 StartZ=0 EndX=33.7 EndY=10.1 EndZ=0
    g45: LineSegment StartX=24.2 StartY=-9.9 StartZ=0 EndX=17.7 EndY=-9.9 EndZ=0
    g46: LineSegment StartX=27.2 StartY=-9.9 StartZ=0 EndX=33.7 EndY=-9.9 EndZ=0
    g47: LineSegment StartX=24.3 StartY=1.25 StartZ=0 EndX=24.3 EndY=-1.25 EndZ=0
    g48: LineSegment StartX=27.1 StartY=1.25 StartZ=0 EndX=27.1 EndY=-1.25 EndZ=0
    g49: LineSegment StartX=24.3 StartY=1e-15 StartZ=0 EndX=25.7 EndY=0 EndZ=0
    g50: LineSegment StartX=25.7 StartY=0 StartZ=0 EndX=27.1 EndY=1e-15 EndZ=0
  constraints (133):
    c: Horizontal(g0)
    c: Coincident(g0,g1)
    c: Vertical(g1)
    c: Coincident(g1,g2)
    c: Vertical(g2)
    c: Coincident(g2,g3)
    c: Horizontal(g3)
    c: DistanceY(g2,g2) = 56
    c: Equal(g3,g0)
    c: DistanceX(g0,g0) = 38
    c: Coincident(g4,g0)
    c: Coincident(g5,g3)
    c: Equal(g5,g4)
    c: Diameter(g5) = 8
    c: Horizontal(g6)
    c: Horizontal(g7)
    c: Tangent(g4,g6) = 1.5708
    c: Tangent(g4,g7) = -1.5708
    c: Distance(g42,g1) = 5
    c: Horizontal(g8)
    c: Horizontal(g9)
    c: Tangent(g5,g8) = 1.5708
    c: Tangent(g5,g9) = -1.5708
    c: Equal(g6,g9)
    c: Tangent(g12,g11) = -1.5708
    c: Tangent(g13,g10) = -1.5708
    c: Equal(g10,g11)
    c: Diameter(g10) = 16
    c: Vertical(g14)
    c: PointOnObject(g6,g1)
    c: Vertical(g15)
    c: Tangent(g15,g16) = -1.5708
    c: Tangent(g16,g6) = 1.5708
    c: Distance(g15,g1) = 5
    c: Vertical(g17)
    c: Vertical(g18)
    c: Distance(g18,g2) = 5
    c: Tangent(g19,g9) = -1.5708
    c: Tangent(g19,g18) = 1.5708
    c: Equal(g11,g20)
    c: Coincident(g11,g17)
    c: Coincident(g20,g18)
    c: Coincident(g11,g20)
    c: Tangent(g20,g13) = -1.5708
    c: Equal(g10,g21)
    c: Coincident(g21,g14)
    c: Coincident(g10,g21)
    c: Coincident(g10,g15)
    c: Tangent(g21,g12) = -1.5708
    c: Coincident(g22,g1)
    c: Diameter(g22) = 3.1
    c: Coincident(g23,g24)
    c: Coincident(g24,g25)
    c: Coincident(g25,g26)
    c: Coincident(g26,g23)
    c: Coincident(g28,g27)
    c: Coincident(g30,g29)
    c: Equal(g28,g27)
    c: Equal(g27,g30)
    c: Equal(g30,g29)
    c: Coincident(g31,g32)
    c: Coincident(g32,g33)
    c: Coincident(g33,g34)
    c: Coincident(g34,g31)
    c: Coincident(g36,g35)
    c: Coincident(g38,g37)
    c: Coincident(g37,g-5)
    c: Coincident(g35,g-6)
    c: Coincident(g-4,g29)
    c: Coincident(g27,g-3)
    c: PointOnObject(g40,g8)
    c: PointOnObject(g40,g17)
    c: Tangent(g8,g39) = -1.5708
    c: Tangent(g17,g39) = -1.5708
    c: Radius(g39) = 5
    c: Symmetric(g11,g18,g2)
    c: PointOnObject(g42,g7)
    c: PointOnObject(g42,g14)
    c: Tangent(g7,g41) = 1.5708
    c: Tangent(g14,g41) = 1.5708
    c: Equal(g41,g39)
    c: DistanceY(g1,g1) = 40
    c: Distance(g27) = 0.1
    c: Perpendicular(g-3,g27)
    c: Perpendicular(g28,g27)
    c: PointOnObject(g28,g26)
    c: PointOnObject(g27,g23)
    c: Perpendicular(g28,g26)
    c: Perpendicular(g23,g27)
    c: Perpendicular(g-4,g30)
    c: Perpendicular(g29,g30)
    c: PointOnObject(g29,g24)
    c: PointOnObject(g30,g25)
    c: Perpendicular(g25,g30)
    c: Perpendicular(g29,g24)
    c: Perpendicular(g-5,g38)
    c: Perpendicular(g37,g38)
    c: Perpendicular(g35,g-6)
    c: Perpendicular(g36,g35)
    c: Equal(g35,g36)
    c: Equal(g36,g37)
    c: Equal(g37,g38)
    c: Equal(g38,g27)
    c: PointOnObject(g35,g31)
    c: PointOnObject(g36,g34)
    c: Perpendicular(g34,g36)
    c: Perpendicular(g31,g35)
    c: PointOnObject(g38,g33)
    c: PointOnObject(g37,g32)
    c: Perpendicular(g32,g37)
    c: Perpendicular(g33,g38)
    c: Coincident(g43,g23)
    c: Coincident(g43,g12)
    c: Coincident(g44,g23)
    c: Coincident(g44,g10)
    c: Perpendicular(g44,g24)
    c: Perpendicular(g43,g26)
    c: Coincident(g45,g33)
    c: Coincident(g45,g11)
    c: Coincident(g46,g32)
    c: Coincident(g46,g13)
    c: Perpendicular(g32,g46)
    c: Coincident(g47,g-8)
    c: Coincident(g47,g-7)
    c: Coincident(g48,g-8)
    c: Coincident(g48,g-7)
    c: Coincident(g50,g49)
    c: PointOnObject(g50,g48)
    c: Equal(g49,g50)
    c: Perpendicular(g49,g47)
    c: Perpendicular(g48,g50)
    c: Symmetric(g47,g47,g49)
    c: Coincident(g22,g49)
FEATURE [PartDesign::Pad] Pad006
  Direction = (-6e-16,2.1e-15,1)
  Length = 2.8
  Length2 = 10
  Placement = pos=(2.9e-14,-1.09e-13,-53) rot=(1,0,0;3.14159rad)
  Profile = -> Sketch006
  ReferenceAxis = -> Sketch006 [N_Axis]
  Type = 0
  expr: Length = Spreadsheet.acrylic_thin
FEATURE [PartDesign::Body] Body007  label="feet_right"
  Group = -> [Sketch006,Binder009,DatumPlane,Pad006]
  Origin = -> Origin009
  Tip = -> Pad006
FEATURE [PartDesign::FeatureBase] Clone
  BaseFeature = -> Body
FEATURE [PartDesign::Body] Body008  label="cam_left_1"
  Group = -> [Clone]
  Origin = -> Origin010
  Placement = pos=(0,0,0) rot=(0,1,0;3.14159rad)
  Tip = -> Clone
FEATURE [PartDesign::FeatureBase] Clone001
  BaseFeature = -> Body003
FEATURE [PartDesign::Body] Body009  label="cam_left_2"
  Group = -> [Clone001]
  Origin = -> Origin011
  Placement = pos=(0,0,0) rot=(0,1,0;3.14159rad)
  Tip = -> Clone001
FEATURE [PartDesign::FeatureBase] Clone002
  BaseFeature = -> Body004
FEATURE [PartDesign::Body] Body010  label="cam_left_3"
  Group = -> [Clone002]
  Origin = -> Origin012
  Placement = pos=(0,0,0) rot=(0,1,0;3.14159rad)
  Tip = -> Clone002
FEATURE [PartDesign::FeatureBase] Clone003
  BaseFeature = -> Body005
FEATURE [PartDesign::Body] Body011  label="spacer_left"
  Group = -> [Clone003]
  Origin = -> Origin013
  Placement = pos=(0,0,0) rot=(0,1,0;3.14159rad)
  Tip = -> Clone003
FEATURE [PartDesign::FeatureBase] Clone007
  BaseFeature = -> Body007
FEATURE [PartDesign::Body] Body015  label="feet_left"
  Group = -> [Clone007]
  Origin = -> Origin017
  Placement = pos=(1e-14,0,-83.2) rot=(0,1,0;3.14159rad)
  Tip = -> Clone007
FEATURE [PartDesign::Fillet] Fillet
  Base = -> Pad004 [Edge1,Edge2,Edge11,Edge14,Edge53,Edge20,Edge38,Edge35,Edge50,Edge23,Edge41,Edge32,Edge26,Edge47,Edge44,Edge29]
  BaseFeature = -> Pad004
  Placement = pos=(-24.3,8e-15,-1.4e-14) rot=(0.57735,-0.57735,-0.57735;2.0944rad)
  Radius = 0.4
  SupportTransform = false
  UseAllEdges = false
FEATURE [PartDesign::Fillet] Fillet001
  Base = -> Fillet [Edge91,Edge93]
  BaseFeature = -> Fillet
  Placement = pos=(-24.3,8e-15,-1.4e-14) rot=(0.57735,-0.57735,-0.57735;2.0944rad)
  Radius = 5
  SupportTransform = false
  UseAllEdges = false
FEATURE [PartDesign::SubShapeBinder] Binder010
  BindCopyOnChange = 0
  BindMode = 0
  ClaimChildren = false
  Context = -> Body017 [Binder010.]
  Fuse = false
  MakeFace = true
  OffsetFill = false
  OffsetIntersection = false
  OffsetJoinType = 0
  OffsetOpenResult = false
  PartialLoad = false
  Relative = true
  Support = -> [Part001]
  _Version = 2
FEATURE [PartDesign::SubShapeBinder] Binder011
  BindCopyOnChange = 0
  BindMode = 0
  ClaimChildren = false
  Context = -> Body017 [Binder011.]
  Fuse = false
  MakeFace = true
  OffsetFill = false
  OffsetIntersection = false
  OffsetJoinType = 0
  OffsetOpenResult = false
  PartialLoad = false
  Relative = true
  Support = -> [Body002]
  _Version = 2
FEATURE [PartDesign::SubShapeBinder] Binder012
  BindCopyOnChange = 0
  BindMode = 0
  ClaimChildren = false
  Context = -> Body017 [Binder012.]
  Fuse = false
  MakeFace = true
  OffsetFill = false
  OffsetIntersection = false
  OffsetJoinType = 0
  OffsetOpenResult = false
  PartialLoad = false
  Relative = true
  Support = -> [Body014]
  _Version = 2
FEATURE [Sketcher::SketchObject] Sketch007
  ExternalGeometry = -> [Binder010,Binder011,Binder012]
  FullyConstrained = true
  MapMode = 5
  Placement = pos=(-9.4,0,0) rot=(0.57735,-0.57735,-0.57735;2.0944rad)
  Support = -> [Binder010]
  expr: Constraints[77] = Spreadsheet.acrylic_thin
  expr: Constraints[80] = Spreadsheet.acrylic_thin
  expr: Constraints[84] = Spreadsheet.acrylic_thin * 2
  sketch-geometry (39):
    g0: Circle CenterX=0 CenterY=10.85 CenterZ=0 NormalX=0 NormalY=0 NormalZ=1 AngleXU=0 Radius=2.1
    g1: Circle CenterX=-8.9 CenterY=20.85 CenterZ=0 NormalX=0 NormalY=0 NormalZ=1 AngleXU=0 Radius=1.55
    g2: Circle CenterX=8.9 CenterY=20.85 CenterZ=0 NormalX=0 NormalY=0 NormalZ=1 AngleXU=0 Radius=1.55
    g3: Circle CenterX=-1.19e-14 CenterY=72.5 CenterZ=0 NormalX=0 NormalY=0 NormalZ=1 AngleXU=0 Radius=1.55
    g4: ArcOfCircle CenterX=-8.15 CenterY=75.1 CenterZ=0 NormalX=0 NormalY=0 NormalZ=1 AngleXU=0 Radius=3 StartAngle=1.5708 EndAngle=3.14159
    g5: ArcOfCircle CenterX=8.15 CenterY=75.1 CenterZ=0 NormalX=0 NormalY=0 NormalZ=1 AngleXU=0 Radius=3 StartAngle=1.6841e-12 EndAngle=1.5708
    g6: LineSegment StartX=11.15 StartY=75.1 StartZ=0 EndX=11.15 EndY=36.85 EndZ=0
    g7: ArcOfCircle CenterX=8.15 CenterY=9.85 CenterZ=0 NormalX=0 NormalY=0 NormalZ=1 AngleXU=0 Radius=3 StartAngle=4.71239 EndAngle=6.28319
    g8: LineSegment StartX=8.15 StartY=6.85 StartZ=0 EndX=-11.15 EndY=6.85 EndZ=0
    g9: LineSegment StartX=-11.15 StartY=39.85 StartZ=0 EndX=-11.15 EndY=75.1 EndZ=0
    g10: GeomPoint X=11.15 Y=6.85 Z=0
    g11: ArcOfCircle CenterX=-3.18082 CenterY=49.59 CenterZ=0 NormalX=0 NormalY=0 NormalZ=1 AngleXU=0 Radius=3 StartAngle=1.5708 EndAngle=3.14159
    g12: LineSegment StartX=-3.18082 StartY=52.59 StartZ=0 EndX=3.18082 EndY=52.59 EndZ=0
    g13: ArcOfCircle CenterX=3.18082 CenterY=49.59 CenterZ=0 NormalX=0 NormalY=0 NormalZ=1 AngleXU=0 Radius=3 StartAngle=-7.3053e-12 EndAngle=1.5708
    g14: ArcOfCircle CenterX=3.18082 CenterY=28.85 CenterZ=0 NormalX=0 NormalY=0 NormalZ=1 AngleXU=0 Radius=3 StartAngle=4.71239 EndAngle=6.28319
    g15: LineSegment StartX=3.18082 StartY=25.85 StartZ=0 EndX=-3.18082 EndY=25.85 EndZ=0
    g16: ArcOfCircle CenterX=-3.18082 CenterY=28.85 CenterZ=0 NormalX=0 NormalY=0 NormalZ=1 AngleXU=0 Radius=3 StartAngle=3.14159 EndAngle=4.71239
    g17: LineSegment StartX=-6.18082 StartY=28.85 StartZ=0 EndX=-6.18082 EndY=49.59 EndZ=0
    g18: LineSegment StartX=6.18082 StartY=49.59 StartZ=0 EndX=6.18082 EndY=28.85 EndZ=0
    g19: LineSegment StartX=-11.15 StartY=6.85 StartZ=0 EndX=-37.15 EndY=6.85 EndZ=0
    g20: ArcOfCircle CenterX=-37.15 CenterY=7.85 CenterZ=0 NormalX=0 NormalY=0 NormalZ=1 AngleXU=0 Radius=1 StartAngle=3.14159 EndAngle=4.71239
    g21: ArcOfCircle CenterX=-39.15 CenterY=7.85 CenterZ=0 NormalX=0 NormalY=0 NormalZ=1 AngleXU=0 Radius=1 StartAngle=0 EndAngle=3.14159
    g22: ArcOfCircle CenterX=-41.15 CenterY=7.85 CenterZ=0 NormalX=0 NormalY=0 NormalZ=1 AngleXU=0 Radius=1 StartAngle=3.14159 EndAngle=6.28319
    g23: LineSegment StartX=-42.15 StartY=7.85 StartZ=0 EndX=-42.15 EndY=35.85 EndZ=0
    g24: ArcOfCircle CenterX=-41.15 CenterY=35.85 CenterZ=0 NormalX=0 NormalY=0 NormalZ=1 AngleXU=0 Radius=1 StartAngle=-1.8e-15 EndAngle=3.14159
    g25: ArcOfCircle CenterX=-39.15 CenterY=35.85 CenterZ=0 NormalX=0 NormalY=0 NormalZ=1 AngleXU=0 Radius=1 StartAngle=3.14159 EndAngle=6.28319
    g26: ArcOfCircle CenterX=-37.15 CenterY=35.85 CenterZ=0 NormalX=0 NormalY=0 NormalZ=1 AngleXU=0 Radius=1 StartAngle=1.5708 EndAngle=3.14159
    g27: LineSegment StartX=-37.15 StartY=36.85 StartZ=0 EndX=-14.15 EndY=36.85 EndZ=0
    g28: ArcOfCircle CenterX=-14.15 CenterY=39.85 CenterZ=0 NormalX=0 NormalY=0 NormalZ=1 AngleXU=0 Radius=3 StartAngle=4.71239 EndAngle=6.28319
    g29: LineSegment StartX=-8.15 StartY=78.1 StartZ=0 EndX=8.15 EndY=78.1 EndZ=0
    g30: ArcOfCircle CenterX=12.55 CenterY=13.85 CenterZ=0 NormalX=0 NormalY=0 NormalZ=1 AngleXU=0 Radius=1.4 StartAngle=6e-16 EndAngle=3.14159
    g31: LineSegment StartX=13.95 StartY=13.85 StartZ=0 EndX=13.95 EndY=8.25 EndZ=0
    g32: ArcOfCircle CenterX=15.35 CenterY=8.25 CenterZ=0 NormalX=0 NormalY=0 NormalZ=1 AngleXU=0 Radius=1.4 StartAngle=3.14159 EndAngle=6.28319
    g33: LineSegment StartX=16.75 StartY=8.25 StartZ=0 EndX=16.75 EndY=39.65 EndZ=0
    g34: ArcOfCircle CenterX=15.35 CenterY=39.65 CenterZ=0 NormalX=0 NormalY=0 NormalZ=1 AngleXU=0 Radius=1.4 StartAngle=-9e-16 EndAngle=3.14159
    g35: LineSegment StartX=13.95 StartY=39.65 StartZ=0 EndX=13.95 EndY=36.85 EndZ=0
    g36: LineSegment StartX=13.95 StartY=36.85 StartZ=0 EndX=11.15 EndY=36.85 EndZ=0
    g37: LineSegment StartX=8.15 StartY=6.85 StartZ=0 EndX=15.35 EndY=6.85 EndZ=0
    g38: LineSegment StartX=11.15 StartY=13.85 StartZ=0 EndX=11.15 EndY=9.85 EndZ=0
  constraints (98):
    c: Equal(g1,g2)
    c: Diameter(g1) = 3.1
    c: Diameter(g3) = 3.1
    c: Tangent(g5,g6) = 1.5708
    c: Tangent(g7,g8) = 1.5708
    c: Tangent(g9,g4) = 1.5708
    c: Horizontal(g8)
    c: Vertical(g6)
    c: Vertical(g9)
    c: Equal(g4,g5)
    c: Equal(g5,g7)
    c: PointOnObject(g10,g6)
    c: PointOnObject(g10,g8)
    c: Distance(g0,g8) = 4
    c: Tangent(g11,g12) = 1.5708
    c: Tangent(g12,g13) = 1.5708
    c: Tangent(g14,g15) = 1.5708
    c: Tangent(g15,g16) = 1.5708
    c: Tangent(g17,g11) = 1.5708
    c: Horizontal(g12)
    c: Horizontal(g15)
    c: Vertical(g17)
    c: Radius(g11) = 3
    c: Coincident(g0,g-5)
    c: Coincident(g1,g-3)
    c: Coincident(g2,g-4)
    c: PointOnObject(g38,g-7)
    c: Tangent(g16,g17) = 1.5708
    c: Vertical(g18)
    c: Tangent(g18,g14) = 1.5708
    c: Tangent(g18,g13) = 1.5708
    c: Equal(g11,g13)
    c: Equal(g13,g14)
    c: Equal(g14,g16)
    c: PointOnObject(g16,g-10)
    c: PointOnObject(g14,g-11)
    c: Horizontal(g15,g-10)
    c: PointOnObject(g19,g-6)
    c: Horizontal(g19)
    c: Tangent(g19,g20) = 1.5708
    c: Tangent(g20,g21) = 1.5708
    c: Tangent(g21,g22) = 1.5708
    c: Vertical(g23)
    c: Tangent(g23,g24) = 1.5708
    c: Tangent(g24,g25) = 1.5708
    c: Tangent(g25,g26) = 1.5708
    c: Horizontal(g27)
    c: Coincident(g8,g19)
    c: Tangent(g9,g28) = -1.5708
    c: Tangent(g27,g28) = -1.5708
    c: Tangent(g26,g27) = 1.5708
    c: Tangent(g22,g23) = 1.5708
    c: Equal(g20,g21)
    c: Equal(g20,g22)
    c: Equal(g20,g24)
    c: Equal(g20,g25)
    c: Equal(g20,g26)
    c: Radius(g20) = 1
    c: Angle(g20) = 1.5708
    c: Angle(g21) = 3.14159
    c: Angle(g26) = 1.5708
    c: Angle(g25) = 3.14159
    c: Radius(g4) = 3
    c: Equal(g28,g4)
    c: DistanceY(g8,g27) = 30
    c: DistanceX(g19,g19) = 26
    c: Vertical(g9,g8)
    c: Horizontal(g29)
    c: Tangent(g29,g4) = 1.5708
    c: Tangent(g29,g5) = 1.5708
    c: Vertical(g31)
    c: Tangent(g31,g32) = -1.5708
    c: Vertical(g33)
    c: Vertical(g35)
    c: Coincident(g35,g36)
    c: Horizontal(g36)
    c: Equal(g36,g35)
    c: DistanceX(g36,g36) = 2.8
    c: Tangent(g33,g34) = -1.5708
    c: Tangent(g34,g35) = -1.5708
    c: Diameter(g34) = 2.8
    c: Equal(g32,g34)
    c: Tangent(g32,g33) = -1.5708
    c: Tangent(g30,g31) = 1.5708
    c: DistanceY(g32,g30) = 5.6
    c: Tangent(g30,g6) = -1.5708
    c: Coincident(g37,g7)
    c: Horizontal(g37)
    c: Horizontal(g36,g27)
    c: Tangent(g37,g32) = -1.5708
    c: Coincident(g6,g36)
    c: Vertical(g38)
    c: Coincident(g38,g30)
    c: Tangent(g38,g7) = 1.5708
    c: Diameter(g0) = 4.2
    c: Symmetric(g-12,g-13,g3)
    c: Tangent(g29,g-12)
    c: PointOnObject(g11,g-14)
FEATURE [PartDesign::Pad] Pad007
  Direction = (-1,0,0)
  Length = 2.8
  Length2 = 10
  Profile = -> Sketch007
  ReferenceAxis = -> Sketch007 [N_Axis]
  Type = 0
  expr: Length = Spreadsheet.acrylic_thin
FEATURE [PartDesign::Body] Body017  label="body_right"
  Group = -> [Sketch007,Binder010,Binder011,Binder012,Pad007]
  Origin = -> Origin019
  Tip = -> Pad007
FEATURE [Part::Feature] Part__Feature  label="batt_9V005_cp_sp"
  shape: bbox 13.59 x 26.29 x 1.575 mm, 21 faces (baked)
FEATURE [Part::Feature] Part__Feature003  label="batt_9V005_cp_sp003"
  shape: bbox 7.925 x 7.925 x 3.557 mm, 27 faces (baked)
FEATURE [Part::Feature] Part__Feature004  label="batt_9V005_cp_sp004"
  shape: bbox 9.35 x 9.35 x 4.186 mm, 125 faces (baked)
FEATURE [Part::Feature] Part__Feature005  label="batt_9V005_cp_sp005"
  shape: bbox 15.74 x 25.33 x 0.8457 mm, 1 faces, 0 solids (baked)
FEATURE [Part::Feature] Part__Feature006  label="batt_9V005_cp_sp006"
  shape: bbox 15.38 x 24.78 x 2e-07 mm, 1 faces, 0 solids (baked)
FEATURE [Part::Feature] Part__Feature007  label="batt_9V005_cp_sp007"
  shape: bbox 16.6 x 26 x 42.82 mm, 188 faces, 0 solids (baked)
FEATURE [Part::Feature] Part__Feature008  label="batt_9V005_cp_sp008"
  shape: bbox 7.6 x 8.776 x 3 mm, 28 faces, 0 solids (baked)
FEATURE [Part::Feature] Part__Feature009  label="batt_9V005_cp_sp009"
  shape: bbox 6.35 x 6.35 x 1.5 mm, 2 faces, 0 solids (baked)
FEATURE [Part::Feature] Part__Feature010  label="batt_9V005_cp_sp010"
  shape: bbox 8 x 8 x 3.2 mm, 10 faces, 0 solids (baked)
FEATURE [App::Part] batt_9V005_cp_sp  label="batt_9V005_cp_sp011"
  Group = -> [Part__Feature,Part__Feature003,Part__Feature004,Part__Feature005,Part__Feature006,Part__Feature007,Part__Feature008,Part__Feature009,Part__Feature010]
  Origin = -> Origin020
  Placement = pos=(0,25,40) rot=(0,0,1;0rad)
FEATURE [PartDesign::FeatureBase] Clone008
  BaseFeature = -> Body017
FEATURE [PartDesign::Body] Body018  label="body_left"
  Group = -> [Clone008]
  Origin = -> Origin021
  Placement = pos=(21.6,0,0) rot=(0,0,1;0rad)
  Tip = -> Clone008
FEATURE [PartDesign::SubShapeBinder] Binder013
  BindCopyOnChange = 0
  BindMode = 0
  ClaimChildren = false
  Context = -> Body019 [Binder013.]
  Fuse = false
  MakeFace = true
  OffsetFill = false
  OffsetIntersection = false
  OffsetJoinType = 0
  OffsetOpenResult = false
  PartialLoad = false
  Relative = true
  Support = -> [Body017]
  _Version = 2
FEATURE [PartDesign::SubShapeBinder] Binder014
  BindCopyOnChange = 0
  BindMode = 0
  ClaimChildren = false
  Context = -> Body019 [Binder014.]
  Fuse = false
  MakeFace = true
  OffsetFill = false
  OffsetIntersection = false
  OffsetJoinType = 0
  OffsetOpenResult = false
  PartialLoad = false
  Relative = true
  Support = -> [Body018]
  _Version = 2
FEATURE [Sketcher::SketchObject] Sketch008
  ExternalGeometry = -> [Binder014]
  FullyConstrained = true
  MapMode = 5
  Placement = pos=(0,0,0) rot=(0.57735,0.57735,0.57735;2.0944rad)
  Support = -> [YZ_Plane020]
  sketch-geometry (2):
    g0: Circle CenterX=5e-16 CenterY=72.5 CenterZ=0 NormalX=0 NormalY=0 NormalZ=1 AngleXU=0 Radius=1.55
    g1: Circle CenterX=5e-16 CenterY=72.5 CenterZ=0 NormalX=0 NormalY=0 NormalZ=1 AngleXU=0 Radius=4
  constraints (4):
    c: Coincident(g0,g-3)
    c: Coincident(g1,g0)
    c: Equal(g0,g-3)
    c: Diameter(g1) = 8
FEATURE [PartDesign::Pad] Pad008
  Direction = (1,-2e-16,3e-16)
  Length = 18.8
  Length2 = 10
  Midplane = true
  Placement = pos=(0,0,0) rot=(0.57735,0.57735,0.57735;2.0944rad)
  Profile = -> Sketch008
  ReferenceAxis = -> Sketch008 [N_Axis]
  Type = 0
FEATURE [PartDesign::Body] Body019  label="spacer_top_centre"
  Group = -> [Sketch008,Binder013,Binder014,Pad008]
  Origin = -> Origin022
  Tip = -> Pad008
FEATURE [PartDesign::SubShapeBinder] Binder015
  BindCopyOnChange = 0
  BindMode = 0
  ClaimChildren = false
  Context = -> Body020 [Binder015.]
  Fuse = false
  MakeFace = true
  OffsetFill = false
  OffsetIntersection = false
  OffsetJoinType = 0
  OffsetOpenResult = false
  PartialLoad = false
  Relative = true
  Support = -> [Body017]
  _Version = 2
FEATURE [PartDesign::SubShapeBinder] Binder016
  BindCopyOnChange = 0
  BindMode = 0
  ClaimChildren = false
  Context = -> Body020 [Binder016.]
  Fuse = false
  MakeFace = true
  OffsetFill = false
  OffsetIntersection = false
  OffsetJoinType = 0
  OffsetOpenResult = false
  PartialLoad = false
  Relative = true
  Support = -> [Body002]
  _Version = 2
FEATURE [Sketcher::SketchObject] Sketch009
  ExternalGeometry = -> [Binder015]
  FullyConstrained = true
  MapMode = 5
  Placement = pos=(-12.2,0,0) rot=(0.57735,-0.57735,-0.57735;2.0944rad)
  Support = -> [Binder015]
  sketch-geometry (2):
    g0: Circle CenterX=-5.8e-15 CenterY=72.5 CenterZ=0 NormalX=0 NormalY=0 NormalZ=1 AngleXU=0 Radius=1.55
    g1: Circle CenterX=-5.8e-15 CenterY=72.5 CenterZ=0 NormalX=0 NormalY=0 NormalZ=1 AngleXU=0 Radius=4
  constraints (4):
    c: Coincident(g1,g0)
    c: Diameter(g1) = 8
    c: Equal(g0,g-3)
    c: Coincident(g0,g-3)
FEATURE [PartDesign::Pad] Pad009
  Direction = (-1,0,0)
  Length = 10
  Length2 = 10
  Profile = -> Sketch009
  ReferenceAxis = -> Sketch009 [N_Axis]
  Type = 3
  UpToFace = -> Binder016 [Face1]
FEATURE [Sketcher::SketchObject] Sketch010
  ExternalGeometry = -> [Pad009,Binder016]
  FullyConstrained = true
  MapMode = 5
  Placement = pos=(-24.3,-1.09e-14,-2.58e-14) rot=(0.57735,-0.57735,-0.57735;2.0944rad)
  Support = -> [Pad009]
  sketch-geometry (2):
    g0: Circle CenterX=-2.06e-14 CenterY=72.5 CenterZ=0 NormalX=0 NormalY=0 NormalZ=1 AngleXU=0 Radius=3
    g1: Circle CenterX=-2.06e-14 CenterY=72.5 CenterZ=0 NormalX=0 NormalY=0 NormalZ=1 AngleXU=0 Radius=1.55
  constraints (4):
    c: Equal(g1,g-6)
    c: Coincident(g0,g-6)
    c: Coincident(g0,g1)
    c: Diameter(g0) = 6
FEATURE [PartDesign::Pad] Pad010
  BaseFeature = -> Pad009
  Direction = (-1,-3e-16,-1e-15)
  Length = 6
  Length2 = 10
  Profile = -> Sketch010
  ReferenceAxis = -> Sketch010 [N_Axis]
  Type = 0
  expr: Length = Spreadsheet.acrylic_thin * 2 + 0.4
FEATURE [PartDesign::Body] Body020  label="spacer_top_right"
  Group = -> [Binder015,Binder016,Sketch009,Pad009,Sketch010,Pad010]
  Origin = -> Origin023
  Tip = -> Pad010
FEATURE [PartDesign::FeatureBase] Clone009
  BaseFeature = -> Body020
FEATURE [PartDesign::Body] Body021  label="spacer_top_left"
  Group = -> [Clone009]
  Origin = -> Origin024
  Placement = pos=(0,0,0) rot=(0,0,1;3.14159rad)
  Tip = -> Clone009
FEATURE [Part::FeaturePython] ThreadedRod  label="M3x70-ThreadedRod"  # Fasteners workbench fastener (typed FeaturePython)
  Placement = pos=(-35,0,72.5) rot=(0,-1,0;1.5708rad)
  diameter = 4
  diameterCustom = 6
  invert = false
  leftHanded = false
  length = 70
  matchOuter = false
  offset = 0
  pitchCustom = 1
  thread = false
  type = 4
FEATURE [PartDesign::SubShapeBinder] Binder017
  BindCopyOnChange = 0
  BindMode = 0
  ClaimChildren = false
  Context = -> Body022 [Binder017.]
  Fuse = false
  MakeFace = true
  OffsetFill = false
  OffsetIntersection = false
  OffsetJoinType = 0
  OffsetOpenResult = false
  PartialLoad = false
  Relative = true
  Support = -> [Body017]
  _Version = 2
FEATURE [PartDesign::SubShapeBinder] Binder018
  BindCopyOnChange = 0
  BindMode = 0
  ClaimChildren = false
  Context = -> Body022 [Binder018.]
  Fuse = false
  MakeFace = true
  OffsetFill = false
  OffsetIntersection = false
  OffsetJoinType = 0
  OffsetOpenResult = false
  PartialLoad = false
  Relative = true
  Support = -> [Body018]
  _Version = 2
FEATURE [PartDesign::SubShapeBinder] Binder019
  BindCopyOnChange = 0
  BindMode = 0
  ClaimChildren = false
  Context = -> Body022 [Binder019.]
  Fuse = false
  MakeFace = true
  OffsetFill = false
  OffsetIntersection = false
  OffsetJoinType = 0
  OffsetOpenResult = false
  PartialLoad = false
  Relative = true
  Support = -> [Part001]
  _Version = 2
FEATURE [Sketcher::SketchObject] Sketch011
  ExternalGeometry = -> [Binder017,Binder018]
  FullyConstrained = true
  MapMode = 5
  Placement = pos=(0,-11.15,0) rot=(1,0,0;1.5708rad)
  Support = -> [Binder019]
  expr: Constraints[23] = Spreadsheet.acrylic_thin - 0.3
  expr: Constraints[24] = Spreadsheet.acrylic_thin + 0.3
  sketch-geometry (36):
    g0: LineSegment StartX=-9.4 StartY=36.85 StartZ=0 EndX=-12.2 EndY=36.85 EndZ=0
    g1: LineSegment StartX=-12.2 StartY=36.85 StartZ=0 EndX=-12.2 EndY=76.6 EndZ=0
    g2: ArcOfCircle CenterX=-10.7 CenterY=76.6 CenterZ=0 NormalX=0 NormalY=0 NormalZ=1 AngleXU=0 Radius=1.5 StartAngle=1.5708 EndAngle=3.14159
    g3: LineSegment StartX=-5 StartY=79.6 StartZ=0 EndX=-5 EndY=81.6 EndZ=0
    g4: LineSegment StartX=-9.4 StartY=36.85 StartZ=0 EndX=-9.4 EndY=11.35 EndZ=0
    g5: LineSegment StartX=-9.4 StartY=11.35 StartZ=0 EndX=-12.2 EndY=11.35 EndZ=0
    g6: LineSegment StartX=-12.2 StartY=11.35 StartZ=0 EndX=-12.2 EndY=8.25 EndZ=0
    g7: LineSegment StartX=-12.2 StartY=8.25 StartZ=0 EndX=0 EndY=8.25 EndZ=0
    g8: LineSegment StartX=-10.7 StartY=78.1 StartZ=0 EndX=-6.5 EndY=78.1 EndZ=0
    g9: ArcOfCircle CenterX=-6.5 CenterY=79.6 CenterZ=0 NormalX=0 NormalY=0 NormalZ=1 AngleXU=0 Radius=1.5 StartAngle=4.71239 EndAngle=6.28319
    g10: LineSegment StartX=12.2 StartY=11.35 StartZ=0 EndX=9.4 EndY=11.35 EndZ=0
    g11: LineSegment StartX=9.4 StartY=11.35 StartZ=0 EndX=9.4 EndY=36.85 EndZ=0
    g12: LineSegment StartX=9.4 StartY=36.85 StartZ=0 EndX=12.2 EndY=36.85 EndZ=0
    g13: LineSegment StartX=12.2 StartY=36.85 StartZ=0 EndX=12.2 EndY=76.6 EndZ=0
    g14: ArcOfCircle CenterX=10.7 CenterY=76.6 CenterZ=0 NormalX=0 NormalY=0 NormalZ=1 AngleXU=0 Radius=1.5 StartAngle=4e-15 EndAngle=1.5708
    g15: LineSegment StartX=10.7 StartY=78.1 StartZ=0 EndX=6.5 EndY=78.1 EndZ=0
    g16: ArcOfCircle CenterX=6.5 CenterY=79.6 CenterZ=0 NormalX=0 NormalY=0 NormalZ=1 AngleXU=0 Radius=1.5 StartAngle=3.14159 EndAngle=4.71239
    g17: LineSegment StartX=5 StartY=79.6 StartZ=0 EndX=5 EndY=81.6 EndZ=0
    g18: LineSegment StartX=12.2 StartY=11.35 StartZ=0 EndX=12.2 EndY=8.25 EndZ=0
    g19: LineSegment StartX=12.2 StartY=8.25 StartZ=0 EndX=0 EndY=8.25 EndZ=0
    g20: LineSegment StartX=-19 StartY=104.35 StartZ=0 EndX=19 EndY=104.35 EndZ=0
    g21: LineSegment StartX=19 StartY=104.35 StartZ=0 EndX=19 EndY=96.3913 EndZ=0
    g22: LineSegment StartX=19 StartY=83.1 StartZ=0 EndX=6.5 EndY=83.1 EndZ=0
    g23: LineSegment StartX=-19 StartY=83.1 StartZ=0 EndX=-19 EndY=86.8087 EndZ=0
    g24: LineSegment StartX=-6.5 StartY=83.1 StartZ=0 EndX=-19 EndY=83.1 EndZ=0
    g25: ArcOfCircle CenterX=-6.5 CenterY=81.6 CenterZ=0 NormalX=0 NormalY=0 NormalZ=1 AngleXU=0 Radius=1.5 StartAngle=-3.6e-15 EndAngle=1.5708
    g26: GeomPoint X=-5 Y=83.1 Z=0
    g27: ArcOfCircle CenterX=6.5 CenterY=81.6 CenterZ=0 NormalX=0 NormalY=0 NormalZ=1 AngleXU=0 Radius=1.5 StartAngle=1.5708 EndAngle=3.14159
    g28: ArcOfCircle CenterX=-18 CenterY=94.1 CenterZ=0 NormalX=0 NormalY=0 NormalZ=1 AngleXU=0 Radius=2.5 StartAngle=1.98231 EndAngle=3.14159
    g29: ArcOfCircle CenterX=-18 CenterY=89.1 CenterZ=0 NormalX=0 NormalY=0 NormalZ=1 AngleXU=0 Radius=2.5 StartAngle=3.14159 EndAngle=4.30087
    g30: LineSegment StartX=-20.5 StartY=94.1 StartZ=0 EndX=-20.5 EndY=89.1 EndZ=0
    g31: ArcOfCircle CenterX=18 CenterY=94.1 CenterZ=0 NormalX=0 NormalY=0 NormalZ=1 AngleXU=0 Radius=2.5 StartAngle=6e-16 EndAngle=1.15928
    g32: ArcOfCircle CenterX=18 CenterY=89.1 CenterZ=0 NormalX=0 NormalY=0 NormalZ=1 AngleXU=0 Radius=2.5 StartAngle=5.12391 EndAngle=6.28319
    g33: LineSegment StartX=20.5 StartY=89.1 StartZ=0 EndX=20.5 EndY=94.1 EndZ=0
    g34: LineSegment StartX=-19 StartY=96.3913 StartZ=0 EndX=-19 EndY=104.35 EndZ=0
    g35: LineSegment StartX=19 StartY=86.8087 StartZ=0 EndX=19 EndY=83.1 EndZ=0
  constraints (94):
    c: Coincident(g-3,g0)
    c: Coincident(g0,g-3)
    c: Coincident(g0,g1)
    c: Vertical(g1)
    c: Tangent(g1,g2) = 1.5708
    c: Vertical(g3)
    c: Coincident(g0,g4)
    c: Vertical(g4)
    c: Coincident(g4,g5)
    c: Horizontal(g5)
    c: Coincident(g5,g6)
    c: Vertical(g6)
    c: Coincident(g6,g7)
    c: Horizontal(g7)
    c: Radius(g2) = 1.5
    c: Angle(g2) = 1.5708
    c: DistanceX(g-2,g3) = -5
    c: DistanceY(g3,g26) = 3.5
    c: Tangent(g2,g8) = 1.5708
    c: Tangent(g8,g9) = -1.5708
    c: Tangent(g9,g3) = -1.5708
    c: Equal(g9,g2)
    c: Equal(g0,g5)
    c: DistanceY(g5,g-5) = 2.5
    c: DistanceY(g6,g6) = 3.1
    c: PointOnObject(g7,g-2)
    c: Horizontal(g10)
    c: Coincident(g10,g11)
    c: Coincident(g11,g-4)
    c: Vertical(g11)
    c: Coincident(g11,g12)
    c: Coincident(g12,g-4)
    c: Coincident(g12,g13)
    c: Vertical(g13)
    c: Tangent(g13,g14) = -1.5708
    c: Horizontal(g15)
    c: Tangent(g15,g16) = 1.5708
    c: Vertical(g17)
    c: Tangent(g14,g15) = -1.5708
    c: Equal(g14,g16)
    c: Equal(g16,g2)
    c: Tangent(g16,g17) = 1.5708
    c: Equal(g13,g1)
    c: Equal(g15,g8)
    c: Equal(g11,g4)
    c: Equal(g10,g5)
    c: Coincident(g10,g18)
    c: Vertical(g18)
    c: Coincident(g18,g19)
    c: Coincident(g19,g7)
    c: Horizontal(g19)
    c: PointOnObject(g-9,g8)
    c: Coincident(g20,g21)
    c: Coincident(g35,g22)
    c: Coincident(g24,g23)
    c: Coincident(g34,g20)
    c: Horizontal(g20)
    c: Vertical(g21)
    c: Vertical(g23)
    c: DistanceY(g23,g34) = 21.25
    c: DistanceX(g24,g22) = 38
    c: Symmetric(g24,g35,g-2)
    c: Horizontal(g24)
    c: Horizontal(g22)
    c: PointOnObject(g26,g24)
    c: PointOnObject(g26,g3)
    c: Tangent(g24,g25) = -1.5708
    c: Tangent(g3,g25) = -1.5708
    c: Tangent(g22,g27) = -1.5708
    c: Tangent(g17,g27) = 1.5708
    c: Equal(g25,g27)
    c: Equal(g27,g9)
    c: Tangent(g28,g30) = -1.5708
    c: Tangent(g30,g29) = -1.5708
    c: Equal(g28,g29)
    c: Vertical(g30)
    c: Tangent(g32,g33) = -1.5708
    c: Tangent(g33,g31) = -1.5708
    c: Equal(g31,g32)
    c: Symmetric(g28,g31,g-2)
    c: Symmetric(g29,g32,g-2)
    c: DistanceY(g29,g28) = 5
    c: Equal(g28,g31)
    c: DistanceX(g23,g29) = 1
    c: Radius(g28) = 2.5
    c: DistanceY(g23,g29) = 6
    c: Coincident(g23,g29)
    c: Coincident(g34,g28)
    c: Coincident(g21,g31)
    c: Coincident(g35,g32)
    c: Vertical(g34)
    c: Vertical(g23,g28)
    c: Vertical(g21,g32)
    c: Vertical(g35)
FEATURE [PartDesign::Pad] Pad011
  Direction = (0,-1,2e-16)
  Length = 2.8
  Length2 = 10
  Profile = -> Sketch011
  ReferenceAxis = -> Sketch011 [N_Axis]
  Type = 0
  expr: Length = Spreadsheet.acrylic_thin
FEATURE [PartDesign::SubShapeBinder] Binder020
  BindCopyOnChange = 0
  BindMode = 0
  ClaimChildren = false
  Context = -> Body023 [Binder020.]
  Fuse = false
  MakeFace = true
  OffsetFill = false
  OffsetIntersection = false
  OffsetJoinType = 0
  OffsetOpenResult = false
  PartialLoad = false
  Relative = true
  Support = -> [Body020]
  _Version = 2
FEATURE [PartDesign::SubShapeBinder] Binder021
  BindCopyOnChange = 0
  BindMode = 0
  ClaimChildren = false
  Context = -> Body023 [Binder021.]
  Fuse = false
  MakeFace = true
  OffsetFill = false
  OffsetIntersection = false
  OffsetJoinType = 0
  OffsetOpenResult = false
  PartialLoad = false
  Relative = true
  Support = -> [Body002]
  _Version = 2
FEATURE [PartDesign::Plane] DatumPlane004
  AttachmentOffset = pos=(0,0,0.1) rot=(0,0,1;0rad)
  Length = 148.256
  MapMode = 5
  Placement = pos=(-27.2,9e-15,1.36e-14) rot=(0.57735,-0.57735,-0.57735;2.0944rad)
  ResizeMode = 0
  Support = -> [Binder021]
  Width = 130.375
FEATURE [Sketcher::SketchObject] Sketch012
  ExternalGeometry = -> [Binder020,Binder021]
  FullyConstrained = true
  MapMode = 5
  Placement = pos=(-27.2,9e-15,1.36e-14) rot=(-0.57735,0.57735,0.57735;4.18879rad)
  Support = -> [DatumPlane004]
  sketch-geometry (34):
    g0: LineSegment StartX=-44.0703 StartY=62.2032 StartZ=0 EndX=-2.75559 EndY=81.4686 EndZ=0
    g1: LineSegment StartX=7.87582 StartY=77.5991 StartZ=0 EndX=23.7603 EndY=43.5348 EndZ=0
    g2: LineSegment StartX=27.747 StartY=42.0837 StartZ=0 EndX=61.2804 EndY=57.7206 EndZ=0
    g3: LineSegment StartX=61.2804 StartY=57.7206 StartZ=0 EndX=65.5066 EndY=48.6575 EndZ=0
    g4: LineSegment StartX=65.5066 StartY=48.6575 StartZ=0 EndX=31.9732 EndY=33.0207 EndZ=0
    g5: LineSegment StartX=14.6972 StartY=39.3086 StartZ=0 EndX=2.64634 EndY=65.1517 EndZ=0
    g6: LineSegment StartX=-6.75058 StartY=68.5719 StartZ=0 EndX=-39.8442 EndY=53.1402 EndZ=0
    g7: ArcOfCircle CenterX=-41.9572 CenterY=57.6717 CenterZ=0 NormalX=0 NormalY=0 NormalZ=1 AngleXU=0 Radius=5 StartAngle=2.00713 EndAngle=5.14872
    g8: ArcOfCircle CenterX=26.4792 CenterY=44.8027 CenterZ=0 NormalX=0 NormalY=0 NormalZ=1 AngleXU=0 Radius=3 StartAngle=3.57792 EndAngle=5.14872
    g9: LineSegment StartX=-44.0703 StartY=62.2032 StartZ=0 EndX=-39.8442 EndY=53.1402 EndZ=0
    g10: LineSegment StartX=-6.75058 StartY=68.5719 StartZ=0 EndX=2.64634 EndY=65.1517 EndZ=0
    g11: ArcOfCircle CenterX=26.4792 CenterY=44.8027 CenterZ=0 NormalX=0 NormalY=0 NormalZ=1 AngleXU=0 Radius=13 StartAngle=3.57792 EndAngle=5.14872
    g12: LineSegment StartX=-41.9572 StartY=57.6717 StartZ=0 EndX=-5.70494 EndY=74.5764 EndZ=0
    g13: LineSegment StartX=5.70494 StartY=70.4236 StartZ=0 EndX=22.6097 EndY=34.1713 EndZ=0
    g14: LineSegment StartX=22.6097 StartY=34.1713 StartZ=0 EndX=63.3935 EndY=53.1891 EndZ=0
    g15: LineSegment StartX=-5.70494 StartY=74.5764 StartZ=0 EndX=5.70494 EndY=70.4236 EndZ=0
    g16: LineSegment StartX=-1.92e-14 StartY=72.5 StartZ=0 EndX=-2.05212 EndY=66.8618 EndZ=0
    g17: Circle CenterX=-1.92e-14 CenterY=72.5 CenterZ=0 NormalX=0 NormalY=0 NormalZ=1 AngleXU=0 Radius=3
    g18: ArcOfCircle CenterX=0.625359 CenterY=74.2182 CenterZ=0 NormalX=0 NormalY=0 NormalZ=1 AngleXU=0 Radius=8 StartAngle=0.436332 EndAngle=2.00713
    g19: LineSegment StartX=71.0274 StartY=51.0155 StartZ=0 EndX=76.4652 EndY=53.5512 EndZ=0
    g20: LineSegment StartX=76.4652 StartY=53.5512 StartZ=0 EndX=76.9881 EndY=59.5284 EndZ=0
    g21: LineSegment StartX=76.9881 StartY=59.5284 StartZ=0 EndX=72.0732 EndY=62.9698 EndZ=0
    g22: LineSegment StartX=72.0732 StartY=62.9698 StartZ=0 EndX=66.6354 EndY=60.4341 EndZ=0
    g23: LineSegment StartX=66.6354 StartY=60.4341 StartZ=0 EndX=66.1124 EndY=54.4569 EndZ=0
    g24: LineSegment StartX=66.1124 StartY=54.4569 StartZ=0 EndX=71.0274 EndY=51.0155 EndZ=0
    g25: Circle CenterX=71.5503 CenterY=56.9926 CenterZ=0 NormalX=0 NormalY=0 NormalZ=1 AngleXU=0 Radius=6
    g26: LineSegment StartX=63.3935 StartY=53.1891 StartZ=0 EndX=66.1124 EndY=54.4569 EndZ=0
    g27: LineSegment StartX=72.0732 StartY=62.9698 StartZ=0 EndX=70.3828 EndY=66.595 EndZ=0
    g28: LineSegment StartX=70.3828 StartY=66.595 StartZ=0 EndX=61.7027 EndY=62.5475 EndZ=0
    g29: LineSegment StartX=61.7027 StartY=62.5475 StartZ=0 EndX=61.2804 EndY=57.7206 EndZ=0
    g30: LineSegment StartX=65.5066 StartY=48.6575 StartZ=0 EndX=69.4756 EndY=45.8784 EndZ=0
    g31: LineSegment StartX=69.4756 StartY=45.8784 StartZ=0 EndX=78.1557 EndY=49.926 EndZ=0
    g32: LineSegment StartX=78.1557 StartY=49.926 StartZ=0 EndX=76.4652 EndY=53.5512 EndZ=0
    g33: Circle CenterX=-41.9572 CenterY=57.6717 CenterZ=0 NormalX=0 NormalY=0 NormalZ=1 AngleXU=0 Radius=0.6
  constraints (84):
    c: Coincident(g2,g3)
    c: Coincident(g3,g4)
    c: Tangent(g6,g7) = 1.5708
    c: Tangent(g1,g8) = -1.5708
    c: Tangent(g2,g8) = -1.5708
    c: Perpendicular(g2,g3)
    c: Perpendicular(g4,g3)
    c: Perpendicular(g5,g4)
    c: Perpendicular(g2,g1)
    c: Tangent(g7,g0) = 1.5708
    c: Perpendicular(g5,g6)
    c: Angle(g7) = 3.14159
    c: Coincident(g9,g0)
    c: Coincident(g9,g6)
    c: Distance(g9) = 10
    c: Coincident(g10,g6)
    c: Coincident(g10,g5)
    c: Tangent(g11,g5) = 1.5708
    c: Tangent(g11,g4) = 1.5708
    c: Coincident(g11,g8)
    c: Symmetric(g2,g3,g14)
    c: Perpendicular(g14,g3)
    c: Coincident(g14,g13)
    c: Distance(g14) = 45
    c: Perpendicular(g13,g14)
    c: Perpendicular(g12,g13)
    c: Coincident(g12,g7)
    c: Angle(g10,g5) = 2.35619
    c: Coincident(g12,g15)
    c: Coincident(g13,g15)
    c: Perpendicular(g16,g10)
    c: Perpendicular(g16,g15)
    c: Symmetric(g6,g5,g16)
    c: Symmetric(g12,g13,g16)
    c: Coincident(g16,g-3)
    c: Equal(g12,g13)
    c: Distance(g12) = 40
    c: Coincident(g17,g16)
    c: Equal(g17,g-3)
    c: Tangent(g18,g1) = 1.5708
    c: Tangent(g18,g0) = 1.5708
    c: Equal(g3,g9)
    c: Coincident(g19,g20)
    c: Coincident(g20,g21)
    c: Coincident(g21,g22)
    c: Coincident(g22,g23)
    c: Coincident(g23,g24)
    c: Coincident(g24,g19)
    c: Equal(g19, g20-g24) x5
    c: PointOnObject(g19,g25)
    c: PointOnObject(g20,g25)
    c: PointOnObject(g21,g25)
    c: PointOnObject(g22,g25)
    c: PointOnObject(g23,g25)
    c: PointOnObject(g24,g25)
    c: Parallel(g22,g14)
    c: Coincident(g26,g14)
    c: Coincident(g26,g23)
    c: Perpendicular(g3,g26)
    c: Distance(g23) = 6
    c: Distance(g26) = 3
    c: Coincident(g22,g27)
    c: Coincident(g27,g28)
    c: Coincident(g28,g29)
    c: Coincident(g29,g2)
    c: Coincident(g4,g30)
    c: Coincident(g30,g31)
    c: Coincident(g31,g32)
    c: Coincident(g32,g19)
    c: Equal(g27,g32)
    c: Perpendicular(g22,g27)
    c: Perpendicular(g32,g19)
    c: Distance(g27) = 4
    c: Perpendicular(g28,g27)
    c: Perpendicular(g31,g32)
    c: Parallel(g24,g30)
    c: Parallel(g29,g23)
    c: Distance(g10) = 10
    c: Distance(g16) = 6
    c: Radius(g18) = 8
    c: Radius(g8) = 3
    c: Coincident(g33,g7)
    c: Diameter(g33) = 1.2
    c: Angle(g16) = -1.91986
FEATURE [PartDesign::Pad] Pad012
  Direction = (-1,-2e-16,-8e-16)
  Length = 2.8
  Length2 = 10
  Placement = pos=(-27.2,-1.2e-14,-2.9e-14) rot=(0.57735,-0.57735,-0.57735;2.0944rad)
  Profile = -> Sketch012
  ReferenceAxis = -> Sketch012 [N_Axis]
  Type = 0
  expr: Length = Spreadsheet.acrylic_thin
FEATURE [PartDesign::Body] Body023  label="arm_right"
  Group = -> [Binder020,Binder021,DatumPlane004,Sketch012,Pad012]
  Origin = -> Origin026
  Tip = -> Pad012
FEATURE [PartDesign::FeatureBase] Clone010
  BaseFeature = -> Body023
FEATURE [PartDesign::Body] Body024  label="arm_left"
  Group = -> [Clone010]
  Origin = -> Origin027
  Placement = pos=(57.2,30.65,6.9) rot=(1,0,0;0.436332rad)
  Tip = -> Clone010
FEATURE [Part::FeaturePython] Washer  label="M3-Washer"  # Fasteners workbench fastener (typed FeaturePython)
  Placement = pos=(-30.3,1.6e-14,72.5) rot=(0,-1,0;1.5708rad)
  baseObject = -> Body020 [Edge11]
  diameter = 1
  invert = false
  matchOuter = false
  offset = 0
  type = 11
FEATURE [Part::FeaturePython] Nut001  label="M3-Nut063"  # Fasteners workbench fastener (typed FeaturePython)
  Placement = pos=(-31.1,1.6e-14,72.5) rot=(0,-1,0;1.5708rad)
  baseObject = -> Washer [Edge1]
  diameter = 4
  invert = false
  leftHanded = false
  matchOuter = false
  offset = 0
  thread = false
  type = 25
FEATURE [Part::FeaturePython] Washer001  label="M3-Washer001"  # Fasteners workbench fastener (typed FeaturePython)
  Placement = pos=(30.3,-1.6e-14,72.5) rot=(0,1,0;1.5708rad)
  baseObject = -> Body021 [Edge11]
  diameter = 1
  invert = false
  matchOuter = false
  offset = 0
  type = 11
FEATURE [Part::FeaturePython] Nut002  label="M3-Nut064"  # Fasteners workbench fastener (typed FeaturePython)
  Placement = pos=(31.1,-1.6e-14,72.5) rot=(0,1,0;1.5708rad)
  baseObject = -> Washer001 [Edge1]
  diameter = 4
  invert = false
  leftHanded = false
  matchOuter = false
  offset = 0
  thread = false
  type = 25
FEATURE [Part::FeaturePython] Screw001  label="M2x10-Screw"  # Fasteners workbench fastener (typed FeaturePython)
  Placement = pos=(-21.3,1e-14,-9e-15) rot=(0,-1,0;1.5708rad)
  baseObject = -> Body003 [Edge18]
  diameter = 2
  invert = false
  leftHanded = false
  length = 5
  lengthCustom = 10
  matchOuter = false
  offset = 0
  thread = false
  type = 49
FEATURE [Part::FeaturePython] Screw002  label="M2x10-Screw001"  # Fasteners workbench fastener (typed FeaturePython)
  Placement = pos=(21.3,1e-14,1e-14) rot=(0,1,0;1.5708rad)
  baseObject = -> Body009 [Edge18]
  diameter = 2
  invert = false
  leftHanded = false
  length = 5
  lengthCustom = 10
  matchOuter = false
  offset = 0
  thread = false
  type = 49
FEATURE [Part::FeaturePython] Screw003  label="M3x14-Screw021"  # Fasteners workbench fastener (typed FeaturePython)
  Placement = pos=(-25.7,-1.09e-13,-53) rot=(0.969846,0.243717,0;3.14159rad)
  baseObject = -> Body007 [Edge86]
  diameter = 1
  invert = true
  leftHanded = false
  length = 6
  lengthCustom = 14
  matchOuter = false
  offset = 0
  thread = false
  type = 25
FEATURE [Part::FeaturePython] Nut003  label="M3-Nut060"  # Fasteners workbench fastener (typed FeaturePython)
  Placement = pos=(-25.7,-1.08e-13,-44.75) rot=(1,0,0;3.14159rad)
  baseObject = -> Screw003 [Edge71]
  diameter = 4
  invert = false
  leftHanded = false
  matchOuter = false
  offset = 5.75
  thread = false
  type = 25
FEATURE [Part::FeaturePython] Screw004  label="M3x14-Screw022"  # Fasteners workbench fastener (typed FeaturePython)
  Placement = pos=(25.7,-1.03e-13,-33) rot=(0.969846,-0.243717,0;3.14159rad)
  baseObject = -> Body015 [Edge87]
  diameter = 1
  invert = false
  leftHanded = false
  length = 6
  lengthCustom = 14
  matchOuter = false
  offset = 0
  thread = false
  type = 25
FEATURE [Part::FeaturePython] Nut004  label="M3-Nut061"  # Fasteners workbench fastener (typed FeaturePython)
  Placement = pos=(25.7,-1.04e-13,-24.75) rot=(1,0,0;3.14159rad)
  baseObject = -> Screw004 [Edge71]
  diameter = 4
  invert = false
  leftHanded = false
  matchOuter = false
  offset = 5.75
  thread = false
  type = 25
FEATURE [Part::FeaturePython] Screw005  label="M3x30-Screw"  # Fasteners workbench fastener (typed FeaturePython)
  Placement = pos=(-12.2,-8.9,20.85) rot=(0,-1,0;1.5708rad)
  baseObject = -> Body017 [Edge105]
  diameter = 1
  invert = false
  leftHanded = false
  length = 10
  lengthCustom = 30
  matchOuter = false
  offset = 0
  thread = false
  type = 25
FEATURE [Part::FeaturePython] Nut005  label="M3-Nut065"  # Fasteners workbench fastener (typed FeaturePython)
  Placement = pos=(12.2,-8.9,20.85) rot=(0,1,0;1.5708rad)
  baseObject = -> Body018 [Edge104]
  diameter = 4
  invert = true
  leftHanded = false
  matchOuter = false
  offset = 0
  thread = false
  type = 25
FEATURE [Part::FeaturePython] Screw006  label="M3x30-Screw001"  # Fasteners workbench fastener (typed FeaturePython)
  Placement = pos=(-12.2,8.9,20.85) rot=(0,-1,0;1.5708rad)
  baseObject = -> Body017 [Edge108]
  diameter = 1
  invert = false
  leftHanded = false
  length = 10
  lengthCustom = 30
  matchOuter = false
  offset = 0
  thread = false
  type = 25
FEATURE [Part::FeaturePython] Nut006  label="M3-Nut066"  # Fasteners workbench fastener (typed FeaturePython)
  Placement = pos=(12.2,8.9,20.85) rot=(0,1,0;1.5708rad)
  baseObject = -> Body018 [Edge107]
  diameter = 4
  invert = true
  leftHanded = false
  matchOuter = false
  offset = 0
  thread = false
  type = 25
FEATURE [App::DocumentObjectGroup] Group001  label="3D_prints"
  Group = -> [Body005,Body011,Body019,Body020,Body021]
FEATURE [Part::FeaturePython] Screw007  label="M3x14-Screw023"  # Fasteners workbench fastener (typed FeaturePython)
  Placement = pos=(15.5,-2.165e-12,10) rot=(0,-1,0;1.5708rad)
  baseObject = -> Body011 [Edge6]
  diameter = 1
  invert = false
  leftHanded = false
  length = 6
  lengthCustom = 14
  matchOuter = false
  offset = 0
  thread = false
  type = 25
FEATURE [Part::FeaturePython] Nut007  label="M3-Nut062"  # Fasteners workbench fastener (typed FeaturePython)
  Placement = pos=(29.5,-2.168e-12,10) rot=(0,-1,0;1.5708rad)
  baseObject = -> Screw007 [Edge71]
  diameter = 4
  invert = false
  leftHanded = false
  matchOuter = false
  offset = 0
  thread = false
  type = 25
FEATURE [App::DocumentObjectGroup] Group  label="Fasteners"
  Group = -> [Washer,Nut001,Washer001,Nut002,ThreadedRod,Screw,Nut,Screw001,Screw002,Screw003,Nut003,Screw004,Nut004,Screw005,Nut005,Screw006,Nut006,Screw007,Nut007]
FEATURE [PartDesign::SubShapeBinder] Binder022
  BindCopyOnChange = 0
  BindMode = 0
  ClaimChildren = false
  Context = -> Body025 [Binder022.]
  Fuse = false
  MakeFace = true
  OffsetFill = false
  OffsetIntersection = false
  OffsetJoinType = 0
  OffsetOpenResult = false
  PartialLoad = false
  Relative = true
  Support = -> [Body017[Pad007.]]
  _Version = 2
FEATURE [Sketcher::SketchObject] Sketch013
  ExternalGeometry = -> [Binder022]
  FullyConstrained = true
  MapMode = 5
  Placement = pos=(0,0,0) rot=(0.57735,0.57735,0.57735;2.0944rad)
  Support = -> [YZ_Plane026]
  sketch-geometry (4):
    g0: LineSegment StartX=38.15 StartY=36.85 StartZ=0 EndX=40.15 EndY=36.85 EndZ=0
    g1: LineSegment StartX=40.15 StartY=36.85 StartZ=0 EndX=40.15 EndY=35.85 EndZ=0
    g2: LineSegment StartX=40.15 StartY=35.85 StartZ=0 EndX=38.15 EndY=35.85 EndZ=0
    g3: LineSegment StartX=38.15 StartY=35.85 StartZ=0 EndX=38.15 EndY=36.85 EndZ=0
  constraints (11):
    c: Coincident(g0,g1)
    c: Coincident(g1,g2)
    c: Coincident(g2,g3)
    c: Coincident(g3,g0)
    c: Horizontal(g0)
    c: Horizontal(g2)
    c: Vertical(g1)
    c: Vertical(g3)
    c: DistanceX(g0,g0) = 2
    c: DistanceY(g1,g1) = 1
    c: Symmetric(g2,g1,g-3)
FEATURE [PartDesign::Pad] Pad013
  Direction = (1,-2e-16,3e-16)
  Length = 22.5
  Length2 = 10
  Midplane = true
  Placement = pos=(0,0,0) rot=(0.57735,0.57735,0.57735;2.0944rad)
  Profile = -> Sketch013
  ReferenceAxis = -> Sketch013 [N_Axis]
  Type = 0
FEATURE [PartDesign::FeaturePython] Bend  # WARN: FeaturePython — macro-defined, semantics opaque (R4)
  AutoMiter = true
  BaseFeature = -> Pad013
  BendType = 0
  LengthList = [26]
  LengthSpec = 0
  ReliefFactor = 0.7
  UseReliefFactor = false
  angle = 90
  baseObject = -> Pad013 [Face5]
  bendAList = [90]
  extend1 = 0
  extend2 = 0
  gap1 = 0
  gap2 = 0
  invert = false
  kfactor = 0.5
  length = 26
  maxExtendDist = 5
  minGap = 0.2
  minReliefGap = 1
  miterangle1 = 0
  miterangle2 = 0
  offset = 0
  radius = 1
  reliefType = 0
  reliefd = 1
  reliefw = 0.8
  sketchflip = false
  sketchinvert = false
  unfold = false
FEATURE [PartDesign::FeaturePython] Bend001  # WARN: FeaturePython — macro-defined, semantics opaque (R4)
  AutoMiter = true
  BaseFeature = -> Bend
  BendType = 0
  LengthList = [22.5]
  LengthSpec = 0
  ReliefFactor = 0.7
  UseReliefFactor = false
  angle = 90
  baseObject = -> Bend [Face3]
  bendAList = [90]
  extend1 = 0
  extend2 = 0
  gap1 = 0
  gap2 = 0
  invert = false
  kfactor = 0.5
  length = 22.5
  maxExtendDist = 5
  minGap = 0.2
  minReliefGap = 1
  miterangle1 = 0
  miterangle2 = 0
  offset = 0
  radius = 1
  reliefType = 0
  reliefd = 1
  reliefw = 0.8
  sketchflip = false
  sketchinvert = false
  unfold = false
FEATURE [PartDesign::SubShapeBinder] Binder023
  BindCopyOnChange = 0
  BindMode = 0
  ClaimChildren = false
  Context = -> Body025 [Binder023.]
  Fuse = false
  MakeFace = true
  OffsetFill = false
  OffsetIntersection = false
  OffsetJoinType = 0
  OffsetOpenResult = false
  PartialLoad = false
  Relative = true
  Support = -> [Body018[Clone008.]]
  _Version = 2
FEATURE [PartDesign::FeaturePython] Bend002  # WARN: FeaturePython — macro-defined, semantics opaque (R4)
  AutoMiter = true
  BaseFeature = -> Bend001
  BendType = 0
  LengthList = [26]
  LengthSpec = 0
  ReliefFactor = 0.7
  UseReliefFactor = false
  angle = 90
  baseObject = -> Bend001 [Face3]
  bendAList = [90]
  extend1 = 0
  extend2 = 0
  gap1 = 0
  gap2 = 0
  invert = false
  kfactor = 0.5
  length = 26
  maxExtendDist = 5
  minGap = 0.2
  minReliefGap = 1
  miterangle1 = 0
  miterangle2 = 0
  offset = 0
  radius = 1
  reliefType = 0
  reliefd = 1
  reliefw = 0.8
  sketchflip = false
  sketchinvert = false
  unfold = false
FEATURE [PartDesign::FeaturePython] Bend003  # WARN: FeaturePython — macro-defined, semantics opaque (R4)
  AutoMiter = true
  BaseFeature = -> Bend002
  BendType = 0
  LengthList = [0.1]
  LengthSpec = 0
  ReliefFactor = 0.7
  UseReliefFactor = false
  angle = 90
  baseObject = -> Bend002 [Face3]
  bendAList = [90]
  extend1 = 0
  extend2 = 0
  gap1 = 0
  gap2 = 0
  invert = false
  kfactor = 0.5
  length = 0.1
  maxExtendDist = 5
  minGap = 0.2
  minReliefGap = 1
  miterangle1 = 0
  miterangle2 = 0
  offset = 0
  radius = 1
  reliefType = 0
  reliefd = 1
  reliefw = 0.8
  sketchflip = false
  sketchinvert = false
  unfold = false
FEATURE [PartDesign::Fillet] Fillet002
  Base = -> Bend003 [Edge1,Edge2,Edge3,Edge4,Edge5,Edge6,Edge7,Edge8,Edge9,Edge10,Edge11,Edge12,Edge13,Edge14,Edge15,Edge16,Edge17,Edge18,Edge19,Edge20,Edge21,Edge22,Edge23,Edge24,Edge25,Edge26,Edge27,Edge28,Edge29,Edge30,Edge31,Edge32,Edge33,Edge34,Edge35,Edge36,Edge37,Edge38,Edge39,Edge40,+32 more]
  BaseFeature = -> Bend003
  Radius = 0.4
  Refine = true
  SupportTransform = false
  UseAllEdges = true
FEATURE [PartDesign::Body] Body025  label="elastic_band"
  Group = -> [Binder022,Sketch013,Pad013,Bend,Bend001,Binder023,Bend002,Bend003,Fillet002]
  Origin = -> Origin028
  Tip = -> Fillet002
FEATURE [PartDesign::SubShapeBinder] Binder024
  BindCopyOnChange = 0
  BindMode = 0
  ClaimChildren = false
  Context = -> Body026 [Binder024.]
  Fuse = false
  MakeFace = true
  OffsetFill = false
  OffsetIntersection = false
  OffsetJoinType = 0
  OffsetOpenResult = false
  PartialLoad = false
  Relative = true
  Support = -> [Body017[Pad007.]]
  _Version = 2
FEATURE [Sketcher::SketchObject] Sketch014
  ExternalGeometry = -> [Binder024]
  FullyConstrained = true
  MapMode = 5
  Placement = pos=(-9.4,0,0) rot=(0.57735,0.57735,0.57735;2.0944rad)
  Support = -> [Binder024]
  sketch-geometry (10):
    g0: ArcOfCircle CenterX=14.15 CenterY=31.85 CenterZ=0 NormalX=0 NormalY=0 NormalZ=1 AngleXU=0 Radius=3 StartAngle=1.5708 EndAngle=3.14159
    g1: LineSegment StartX=14.15 StartY=34.85 StartZ=0 EndX=39.15 EndY=34.85 EndZ=0
    g2: ArcOfCircle CenterX=39.15 CenterY=31.85 CenterZ=0 NormalX=0 NormalY=0 NormalZ=1 AngleXU=0 Radius=3 StartAngle=1e-16 EndAngle=1.5708
    g3: LineSegment StartX=42.15 StartY=31.85 StartZ=0 EndX=42.15 EndY=11.85 EndZ=0
    g4: ArcOfCircle CenterX=39.15 CenterY=11.85 CenterZ=0 NormalX=0 NormalY=0 NormalZ=1 AngleXU=0 Radius=3 StartAngle=4.71239 EndAngle=6.28319
    g5: LineSegment StartX=39.15 StartY=8.85 StartZ=0 EndX=14.15 EndY=8.85 EndZ=0
    g6: ArcOfCircle CenterX=14.15 CenterY=11.85 CenterZ=0 NormalX=0 NormalY=0 NormalZ=1 AngleXU=0 Radius=3 StartAngle=3.14159 EndAngle=4.71239
    g7: LineSegment StartX=11.15 StartY=11.85 StartZ=0 EndX=11.15 EndY=31.85 EndZ=0
    g8: GeomPoint X=11.15 Y=34.85 Z=0
    g9: GeomPoint X=42.15 Y=8.85 Z=0
  constraints (24):
    c: Tangent(g0,g1) = 1.5708
    c: Tangent(g1,g2) = 1.5708
    c: Tangent(g2,g3) = 1.5708
    c: Tangent(g3,g4) = 1.5708
    c: Tangent(g4,g5) = 1.5708
    c: Tangent(g5,g6) = 1.5708
    c: Tangent(g6,g7) = 1.5708
    c: Tangent(g7,g0) = 1.5708
    c: Horizontal(g1)
    c: Horizontal(g5)
    c: Vertical(g3)
    c: Vertical(g7)
    c: Equal(g0,g2)
    c: Equal(g2,g4)
    c: Equal(g4,g6)
    c: PointOnObject(g8,g1)
    c: PointOnObject(g8,g7)
    c: PointOnObject(g9,g3)
    c: PointOnObject(g9,g5)
    c: Radius(g0) = 3
    c: PointOnObject(g2,g-4)
    c: Vertical(g0,g-3)
    c: PointOnObject(g1,g-5)
    c: PointOnObject(g4,g-6)
FEATURE [PartDesign::Pad] Pad014
  Direction = (1,0,0)
  Length = 1
  Length2 = 10
  Profile = -> Sketch014
  ReferenceAxis = -> Sketch014 [N_Axis]
  Type = 0
FEATURE [PartDesign::Body] Body026  label="foam_battery_right"
  Group = -> [Binder024,Sketch014,Pad014]
  Origin = -> Origin029
  Tip = -> Pad014
FEATURE [PartDesign::FeatureBase] Clone011
  BaseFeature = -> Body026
FEATURE [PartDesign::Body] Body027  label="foam_battery_left"
  Group = -> [Clone011]
  Origin = -> Origin030
  Placement = pos=(17.8,0,0) rot=(0,0,1;0rad)
  Tip = -> Clone011
FEATURE [PartDesign::SubShapeBinder] Binder025
  BindCopyOnChange = 0
  BindMode = 0
  ClaimChildren = false
  Context = -> Body028 [Binder025.]
  Fuse = false
  MakeFace = true
  OffsetFill = false
  OffsetIntersection = false
  OffsetJoinType = 0
  OffsetOpenResult = false
  PartialLoad = false
  Relative = true
  Support = -> [Body007[Pad006.]]
  _Version = 2
FEATURE [Sketcher::SketchObject] Sketch015
  ExternalGeometry = -> [Binder025]
  FullyConstrained = true
  MapMode = 5
  Placement = pos=(2.92e-14,-1.081e-13,-53) rot=(1,0,0;3.14159rad)
  Support = -> [Binder025]
  sketch-geometry (21):
    g0: LineSegment StartX=-25.7 StartY=44 StartZ=0 EndX=12.3 EndY=44 EndZ=0
    g1: ArcOfCircle CenterX=12.3 CenterY=40 CenterZ=0 NormalX=0 NormalY=0 NormalZ=1 AngleXU=0 Radius=4 StartAngle=4.71239 EndAngle=7.85398
    g2: LineSegment StartX=12.3 StartY=36 StartZ=0 EndX=-15.7 EndY=36 EndZ=0
    g3: ArcOfCircle CenterX=-15.7 CenterY=31 CenterZ=0 NormalX=0 NormalY=0 NormalZ=1 AngleXU=0 Radius=5 StartAngle=1.5708 EndAngle=3.14159
    g4: LineSegment StartX=-20.7 StartY=31 StartZ=0 EndX=-20.7 EndY=16.345 EndZ=0
    g5: ArcOfCircle CenterX=-25.7 CenterY=10.1 CenterZ=0 NormalX=0 NormalY=0 NormalZ=1 AngleXU=0 Radius=8 StartAngle=1e-16 EndAngle=0.895665
    g6: LineSegment StartX=-17.7 StartY=10.1 StartZ=0 EndX=-17.7 EndY=-9.9 EndZ=0
    g7: ArcOfCircle CenterX=-25.7 CenterY=-9.9 CenterZ=0 NormalX=0 NormalY=0 NormalZ=1 AngleXU=0 Radius=8 StartAngle=5.38752 EndAngle=6.28319
    g8: LineSegment StartX=-20.7 StartY=-16.145 StartZ=0 EndX=-20.7 EndY=-47 EndZ=0
    g9: ArcOfCircle CenterX=-15.7 CenterY=-47 CenterZ=0 NormalX=0 NormalY=0 NormalZ=1 AngleXU=0 Radius=5 StartAngle=3.14159 EndAngle=4.71239
    g10: LineSegment StartX=-15.7 StartY=-52 StartZ=0 EndX=12.3 EndY=-52 EndZ=0
    g11: ArcOfCircle CenterX=12.3 CenterY=-56 CenterZ=0 NormalX=0 NormalY=0 NormalZ=1 AngleXU=0 Radius=4 StartAngle=4.71239 EndAngle=7.85398
    g12: LineSegment StartX=12.3 StartY=-60 StartZ=0 EndX=-25.7 EndY=-60 EndZ=0
    g13: ArcOfCircle CenterX=-25.7 CenterY=-55 CenterZ=0 NormalX=0 NormalY=0 NormalZ=1 AngleXU=0 Radius=5 StartAngle=3.14159 EndAngle=4.71239
    g14: LineSegment StartX=-30.7 StartY=-55 StartZ=0 EndX=-30.7 EndY=-16.145 EndZ=0
    g15: ArcOfCircle CenterX=-25.7 CenterY=-9.9 CenterZ=0 NormalX=0 NormalY=0 NormalZ=1 AngleXU=0 Radius=8 StartAngle=3.14159 EndAngle=4.03726
    g16: LineSegment StartX=-33.7 StartY=-9.9 StartZ=0 EndX=-33.7 EndY=10.1 EndZ=0
    g17: ArcOfCircle CenterX=-25.7 CenterY=10.1 CenterZ=0 NormalX=0 NormalY=0 NormalZ=1 AngleXU=0 Radius=8 StartAngle=2.24593 EndAngle=3.14159
    g18: LineSegment StartX=-30.7 StartY=16.345 StartZ=0 EndX=-30.7 EndY=39 EndZ=0
    g19: ArcOfCircle CenterX=-25.7 CenterY=39 CenterZ=0 NormalX=0 NormalY=0 NormalZ=1 AngleXU=0 Radius=5 StartAngle=1.5708 EndAngle=3.14159
    g20: Circle CenterX=-25.7 CenterY=0 CenterZ=0 NormalX=0 NormalY=0 NormalZ=1 AngleXU=0 Radius=4.5
  constraints (46):
    c: Horizontal(g0)
    c: Tangent(g0,g1) = 1.5708
    c: Horizontal(g2)
    c: Tangent(g2,g3) = -1.5708
    c: Vertical(g6)
    c: Tangent(g6,g7) = 1.5708
    c: Vertical(g8)
    c: Tangent(g8,g9) = -1.5708
    c: Horizontal(g10)
    c: Tangent(g10,g11) = 1.5708
    c: Tangent(g11,g12) = 1.5708
    c: Vertical(g14)
    c: Vertical(g16)
    c: Tangent(g16,g17) = 1.5708
    c: Vertical(g18)
    c: Tangent(g18,g19) = 1.5708
    c: Tangent(g19,g0) = 1.5708
    c: Tangent(g1,g2) = 1.5708
    c: Tangent(g3,g4) = -1.5708
    c: Tangent(g5,g6) = 1.5708
    c: Coincident(g17,g18)
    c: Coincident(g4,g5)
    c: Vertical(g4)
    c: Coincident(g7,g8)
    c: Tangent(g9,g10) = -1.5708
    c: Tangent(g13,g14) = 1.5708
    c: Coincident(g14,g15)
    c: Tangent(g15,g16) = 1.5708
    c: Coincident(g19,g-7)
    c: Coincident(g1,g-3)
    c: Coincident(g3,g-8)
    c: Coincident(g5,g-11)
    c: Coincident(g5,g17)
    c: Coincident(g7,g-13)
    c: Coincident(g15,g7)
    c: Coincident(g9,g-5)
    c: Coincident(g11,g-4)
    c: Coincident(g13,g-6)
    c: Equal(g1,g-3)
    c: Equal(g-11,g5)
    c: Equal(g-5,g9)
    c: Tangent(g12,g13) = 1.5708
    c: Equal(g13,g-6)
    c: Equal(g15,g-13)
    c: Coincident(g20,g-9)
    c: Diameter(g20) = 9
FEATURE [PartDesign::Pad] Pad015
  Direction = (5e-16,-2.2e-15,-1)
  Length = 2
  Length2 = 10
  Profile = -> Sketch015
  ReferenceAxis = -> Sketch015 [N_Axis]
  Type = 0
FEATURE [PartDesign::Body] Body028  label="foam_feet_right"
  Group = -> [Binder025,Sketch015,Pad015]
  Origin = -> Origin031
  Tip = -> Pad015
FEATURE [PartDesign::FeatureBase] Clone012
  BaseFeature = -> Body028
FEATURE [PartDesign::Body] Body029  label="foam_feet_left"
  Group = -> [Clone012]
  Origin = -> Origin032
  Placement = pos=(1.1e-14,0,-88) rot=(0,1,0;3.14159rad)
  Tip = -> Clone012
FEATURE [Part::Part2DObjectPython] Shape2DView  label="foam_battery_right_DXF"  # Draft 2D object (typed FeaturePython)
  AutoUpdate = true
  Base = -> Body026
  Clip = false
  FuseArch = false
  HiddenLines = false
  InPlace = true
  OnlySolids = false
  Projection = (-1,0,0)
  ProjectionMode = 0
  SegmentLength = 0.05
  Tessellation = false
  VisibleOnly = false
FEATURE [Part::Part2DObjectPython] Shape2DView001  label="foam_feet_right_DXF"  # Draft 2D object (typed FeaturePython)
  AutoUpdate = true
  Base = -> Body028
  Clip = false
  FuseArch = false
  HiddenLines = false
  InPlace = true
  OnlySolids = false
  Projection = (0,0,1)
  ProjectionMode = 0
  SegmentLength = 0.05
  Tessellation = false
  VisibleOnly = false
FEATURE [Part::Part2DObjectPython] Shape2DView002  label="foam_feet_left_DXF"  # Draft 2D object (typed FeaturePython)
  AutoUpdate = true
  Base = -> Body029
  Clip = false
  FuseArch = false
  HiddenLines = false
  InPlace = true
  OnlySolids = false
  Projection = (0,0,1)
  ProjectionMode = 0
  SegmentLength = 0.05
  Tessellation = false
  VisibleOnly = false
FEATURE [Part::Part2DObjectPython] Shape2DView003  label="foam_battery_left_DXF"  # Draft 2D object (typed FeaturePython)
  AutoUpdate = true
  Base = -> Body027
  Clip = false
  FuseArch = false
  HiddenLines = false
  InPlace = true
  OnlySolids = false
  Projection = (-1,0,0)
  ProjectionMode = 0
  SegmentLength = 0.05
  Tessellation = false
  VisibleOnly = false
FEATURE [Part::Part2DObjectPython] Shape2DView004  label="cam_right_1_DXF"  # Draft 2D object (typed FeaturePython)
  AutoUpdate = true
  Base = -> Body
  Clip = false
  FuseArch = false
  HiddenLines = false
  InPlace = true
  OnlySolids = false
  Projection = (-1,0,0)
  ProjectionMode = 0
  SegmentLength = 0.05
  Tessellation = false
  VisibleOnly = false
FEATURE [Part::Part2DObjectPython] Shape2DView005  label="cam_right_2_DXF"  # Draft 2D object (typed FeaturePython)
  AutoUpdate = true
  Base = -> Body003
  Clip = false
  FuseArch = false
  HiddenLines = false
  InPlace = true
  OnlySolids = false
  Projection = (-1,0,0)
  ProjectionMode = 0
  SegmentLength = 0.05
  Tessellation = false
  VisibleOnly = false
FEATURE [Part::Part2DObjectPython] Shape2DView006  label="cam_right_3_DXF"  # Draft 2D object (typed FeaturePython)
  AutoUpdate = true
  Base = -> Body004
  Clip = false
  FuseArch = false
  HiddenLines = false
  InPlace = true
  OnlySolids = false
  Projection = (-1,0,0)
  ProjectionMode = 0
  SegmentLength = 0.05
  Tessellation = false
  VisibleOnly = false
FEATURE [Part::Part2DObjectPython] Shape2DView008  label="cam_left_1_DXF"  # Draft 2D object (typed FeaturePython)
  AutoUpdate = true
  Base = -> Body008
  Clip = false
  FuseArch = false
  HiddenLines = false
  InPlace = true
  OnlySolids = false
  Projection = (1,0,0)
  ProjectionMode = 0
  SegmentLength = 0.05
  Tessellation = false
  VisibleOnly = false
FEATURE [Part::Part2DObjectPython] Shape2DView009  label="cam_left_2_DXF"  # Draft 2D object (typed FeaturePython)
  AutoUpdate = true
  Base = -> Body009
  Clip = false
  FuseArch = false
  HiddenLines = false
  InPlace = true
  OnlySolids = false
  Projection = (1,0,0)
  ProjectionMode = 0
  SegmentLength = 0.05
  Tessellation = false
  VisibleOnly = false
FEATURE [Part::Part2DObjectPython] Shape2DView010  label="cam_left_3_DXF"  # Draft 2D object (typed FeaturePython)
  AutoUpdate = true
  Base = -> Body010
  Clip = false
  FuseArch = false
  HiddenLines = false
  InPlace = true
  OnlySolids = false
  Projection = (1,0,0)
  ProjectionMode = 0
  SegmentLength = 0.05
  Tessellation = false
  VisibleOnly = false
FEATURE [Part::Part2DObjectPython] Shape2DView012  label="feet_right_DXF"  # Draft 2D object (typed FeaturePython)
  AutoUpdate = true
  Base = -> Body007
  Clip = false
  FuseArch = false
  HiddenLines = false
  InPlace = true
  OnlySolids = false
  Projection = (0,0,1)
  ProjectionMode = 0
  SegmentLength = 0.05
  Tessellation = false
  VisibleOnly = false
FEATURE [Part::Part2DObjectPython] Shape2DView013  label="feet_left_DXF"  # Draft 2D object (typed FeaturePython)
  AutoUpdate = true
  Base = -> Body015
  Clip = false
  FuseArch = false
  HiddenLines = false
  InPlace = true
  OnlySolids = false
  Projection = (0,0,1)
  ProjectionMode = 0
  SegmentLength = 0.05
  Tessellation = false
  VisibleOnly = false
FEATURE [Part::Part2DObjectPython] Shape2DView014  label="body_right_DXF"  # Draft 2D object (typed FeaturePython)
  AutoUpdate = true
  Base = -> Body017
  Clip = false
  FuseArch = false
  HiddenLines = false
  InPlace = true
  OnlySolids = false
  Projection = (-1,0,0)
  ProjectionMode = 0
  SegmentLength = 0.05
  Tessellation = false
  VisibleOnly = false
FEATURE [Part::Part2DObjectPython] Shape2DView015  label="body_left_DXF"  # Draft 2D object (typed FeaturePython)
  AutoUpdate = true
  Base = -> Body018
  Clip = false
  FuseArch = false
  HiddenLines = false
  InPlace = true
  OnlySolids = false
  Projection = (1,0,0)
  ProjectionMode = 0
  SegmentLength = 0.05
  Tessellation = false
  VisibleOnly = false
FEATURE [Part::Part2DObjectPython] Shape2DView016  label="arm_right_DXF"  # Draft 2D object (typed FeaturePython)
  AutoUpdate = true
  Base = -> Body024
  Clip = false
  FuseArch = false
  HiddenLines = false
  InPlace = true
  OnlySolids = false
  Projection = (1,0,0)
  ProjectionMode = 0
  SegmentLength = 0.05
  Tessellation = false
  VisibleOnly = false
FEATURE [Part::Part2DObjectPython] Shape2DView019  label="arm_left_DXF"  # Draft 2D object (typed FeaturePython)
  AutoUpdate = true
  Base = -> Body024
  Clip = false
  FuseArch = false
  HiddenLines = false
  InPlace = true
  OnlySolids = false
  Projection = (-1,0,0)
  ProjectionMode = 0
  SegmentLength = 0.05
  Tessellation = false
  VisibleOnly = false
FEATURE [PartDesign::SubShapeBinder] Binder028
  BindCopyOnChange = 0
  BindMode = 0
  ClaimChildren = false
  Context = -> Body030 [Binder028.]
  Fuse = false
  MakeFace = true
  OffsetFill = false
  OffsetIntersection = false
  OffsetJoinType = 0
  OffsetOpenResult = false
  PartialLoad = false
  Relative = true
  Support = -> [Body024]
  _Version = 2
FEATURE [PartDesign::SubShapeBinder] Binder029
  BindCopyOnChange = 0
  BindMode = 0
  ClaimChildren = false
  Context = -> Body030 [Binder029.]
  Fuse = false
  MakeFace = true
  OffsetFill = false
  OffsetIntersection = false
  OffsetJoinType = 0
  OffsetOpenResult = false
  PartialLoad = false
  Relative = true
  Support = -> [Body014]
  _Version = 2
FEATURE [Sketcher::SketchObject] Sketch016
  ExternalGeometry = -> [Binder028,Binder029]
  FullyConstrained = true
  MapMode = 5
  Placement = pos=(27.1,3.3e-15,1.4e-15) rot=(0.57735,0.57735,0.57735;2.0944rad)
  Support = -> [Binder029]
  sketch-geometry (3):
    g0: LineSegment StartX=43.8765 StartY=76.4783 StartZ=0 EndX=7.42656 EndY=40.422 EndZ=0
    g1: LineSegment StartX=7.42656 StartY=40.422 StartZ=0 EndX=7 EndY=40 EndZ=0
    g2: LineSegment StartX=43.8765 StartY=76.4783 StartZ=0 EndX=44.3031 EndY=76.9002 EndZ=0
  constraints (8):
    c: Coincident(g1,g0)
    c: Parallel(g1,g0)
    c: Coincident(g2,g0)
    c: Parallel(g2,g0)
    c: Coincident(g1,g-4)
    c: PointOnObject(g0,g-4)
    c: Coincident(g2,g-3)
    c: PointOnObject(g0,g-3)
FEATURE [PartDesign::Plane] DatumPlane005
  AttachmentOffset = pos=(0,0,0) rot=(1,0,0;1.5708rad)
  Length = 72.3981
  MapMode = 7
  Placement = pos=(27.1,43.8765,76.4783) rot=(0,0.924915,0.380174;3.14159rad)
  ResizeMode = 0
  Support = -> [Sketch016]
  Width = 138.227
FEATURE [Sketcher::SketchObject] Sketch017
  ExternalGeometry = -> [Binder028,Binder029]
  FullyConstrained = true
  MapMode = 5
  Placement = pos=(27.1,43.8765,76.4783) rot=(0,0.924915,0.380174;3.14159rad)
  Support = -> [DatumPlane005]
  sketch-geometry (9):
    g0: LineSegment StartX=-3.3e-14 StartY=-52.3704 StartZ=0 EndX=2.8 EndY=-52.3704 EndZ=0
    g1: LineSegment StartX=-2.9 StartY=0.6 StartZ=0 EndX=-0.1 EndY=0.6 EndZ=0
    g2: ArcOfCircle CenterX=2.8 CenterY=-51.8704 CenterZ=0 NormalX=0 NormalY=0 NormalZ=1 AngleXU=0 Radius=0.5 StartAngle=4.71239 EndAngle=6.28319
    g3: LineSegment StartX=3.3 StartY=-51.8704 StartZ=0 EndX=3.3 EndY=-47.8704 EndZ=0
    g4: ArcOfCircle CenterX=-2.9 CenterY=0.1 CenterZ=0 NormalX=0 NormalY=0 NormalZ=1 AngleXU=0 Radius=0.5 StartAngle=1.5708 EndAngle=3.14159
    g5: LineSegment StartX=-3.4 StartY=0.1 StartZ=0 EndX=-3.4 EndY=-3.9 EndZ=0
    g6: ArcOfCircle CenterX=-0.1 CenterY=0.1 CenterZ=0 NormalX=0 NormalY=0 NormalZ=1 AngleXU=0 Radius=0.5 StartAngle=6.26587 EndAngle=7.85398
    g7: ArcOfCircle CenterX=-3.55e-14 CenterY=-51.8704 CenterZ=0 NormalX=0 NormalY=0 NormalZ=1 AngleXU=0 Radius=0.5 StartAngle=3.12427 EndAngle=4.71239
    g8: LineSegment StartX=-0.499925 StartY=-51.8618 StartZ=0 EndX=0.399925 EndY=0.0913411 EndZ=0
  constraints (20):
    c: Tangent(g2,g0) = -1.5708
    c: Tangent(g3,g2) = -1.5708
    c: Radius(g2) = 0.5
    c: Perpendicular(g0,g3)
    c: Distance(g3) = 4
    c: Tangent(g4,g1) = 1.5708
    c: Perpendicular(g5,g1)
    c: Equal(g4,g2)
    c: Equal(g3,g5)
    c: Tangent(g4,g5) = -1.5708
    c: Tangent(g0,g7) = -1.5708
    c: Tangent(g6,g1) = 1.5708
    c: Equal(g6,g4)
    c: Equal(g7,g2)
    c: Tangent(g6,g8) = -1.5708
    c: Tangent(g8,g7) = 1.5708
    c: Symmetric(g-5,g-5,g7)
    c: Symmetric(g-6,g-6,g2)
    c: Symmetric(g-3,g-3,g1)
    c: Symmetric(g-4,g-4,g1)
FEATURE [PartDesign::Plane] DatumPlane006
  AttachmentOffset = pos=(0,0,4) rot=(0,0,1;0rad)
  Length = 72.415
  MapMode = 7
  Placement = pos=(30.5,41.1039,73.7355) rot=(1,0,0;2.35076rad)
  ResizeMode = 0
  Support = -> [Sketch017]
  Width = 138.494
FEATURE [Sketcher::SketchObject] Sketch018
  FullyConstrained = true
  MapMode = 5
  Placement = pos=(30.5,41.1039,73.7355) rot=(1,0,0;2.35076rad)
  Support = -> [DatumPlane006]
  sketch-geometry (1):
    g0: Circle CenterX=0 CenterY=0 CenterZ=0 NormalX=0 NormalY=0 NormalZ=1 AngleXU=0 Radius=0.4
  constraints (2):
    c: Diameter(g0) = 0.8
    c: Coincident(g0,g-1)
FEATURE [PartDesign::AdditivePipe] AdditivePipe
  AuxilleryCurvelinear = true
  AuxillerySpineTangent = false
  Binormal = (0,0,0)
  Mode = 0
  Placement = pos=(30.5,41.1039,73.7355) rot=(1,0,0;2.35076rad)
  Profile = -> Sketch018
  Spine = -> Sketch017 [Edge1,Edge2,Edge3,Edge4,Edge5,Edge6,Edge7,Edge8,Edge9]
  SpineTangent = false
  Transformation = 0
  Transition = 0
FEATURE [PartDesign::Body] Body030  label="brass_wire_left"
  Group = -> [Binder028,Binder029,Sketch016,DatumPlane005,Sketch017,DatumPlane006,Sketch018,AdditivePipe]
  Origin = -> Origin033
  Tip = -> AdditivePipe
FEATURE [PartDesign::FeatureBase] Clone013
  BaseFeature = -> Body030
FEATURE [PartDesign::Body] Body031  label="brass_wire_right"
  Group = -> [Clone013]
  Origin = -> Origin034
  Placement = pos=(-4e-15,-32.75,11.6) rot=(0,0.694658,0.71934;3.14159rad)
  Tip = -> Clone013
FEATURE [App::DocumentObjectGroup] Group003  label="other_parts"
  Group = -> [Part001,batt_9V005_cp_sp,Body025,Body026,Body027,Body028,Body029,Body030,Body031]
FEATURE [TechDraw::DrawSVGTemplate] Template
  Height = 210
  Orientation = 1
  Template = <userpath>/Documents/FreeCAD/Templates/A4_Landscape_blank.svg
  Width = 297
FEATURE [TechDraw::DrawViewPart] View
  CoarseView = false
  Direction = (0,-0.707107,0.707107)
  Focus = 100
  HardHidden = false
  IsoCount = 0
  IsoHidden = false
  IsoVisible = false
  LockPosition = false
  Perspective = false
  Rotation = 0
  ScaleType = 0
  ScrubCount = 0
  SeamHidden = false
  SeamVisible = false
  SmoothHidden = false
  SmoothVisible = true
  Source = -> [Body030]
  X = 148.5
  XDirection = (0,0.707107,0.707107)
  Y = 105
FEATURE [TechDraw::DrawViewDimension] Dimension001
  AngleOverride = false
  Arbitrary = false
  ArbitraryTolerances = false
  EqualTolerance = true
  ExtensionAngle = 0
  FormatSpec = %.2w
  FormatSpecOverTolerance = %+.2w
  FormatSpecUnderTolerance = %+.2w
  Inverted = false
  LineAngle = 0
  LockPosition = false
  MeasureType = 1
  OverTolerance = 0
  References2D = -> [View]
  Rotation = 0
  ScaleType = 0
  TheoreticalExact = false
  Type = 1
  UnderTolerance = 0
  X = -15.7775
  Y = 11.3138
FEATURE [TechDraw::DrawViewDimension] Dimension002
  AngleOverride = false
  Arbitrary = false
  ArbitraryTolerances = false
  EqualTolerance = true
  ExtensionAngle = 0
  FormatSpec = %.2w
  FormatSpecOverTolerance = %+.2w
  FormatSpecUnderTolerance = %+.2w
  Inverted = false
  LineAngle = 0
  LockPosition = false
  MeasureType = 1
  OverTolerance = 0
  References2D = -> [View]
  Rotation = 0
  ScaleType = 0
  TheoreticalExact = false
  Type = 2
  UnderTolerance = 0
  X = -41.2836
  Y = 11.8169
FEATURE [TechDraw::DrawViewDimension] Dimension
  AngleOverride = false
  Arbitrary = false
  ArbitraryTolerances = false
  EqualTolerance = true
  ExtensionAngle = 0
  FormatSpec = %.2w
  FormatSpecOverTolerance = %+.2w
  FormatSpecUnderTolerance = %+.2w
  Inverted = false
  LineAngle = 0
  LockPosition = false
  MeasureType = 1
  OverTolerance = 0
  References2D = -> [View]
  Rotation = 0
  ScaleType = 0
  TheoreticalExact = false
  Type = 2
  UnderTolerance = 0
  X = 36.672
  Y = 8.64568
FEATURE [TechDraw::DrawViewDimension] Dimension003
  AngleOverride = false
  Arbitrary = false
  ArbitraryTolerances = false
  EqualTolerance = true
  ExtensionAngle = 0
  FormatSpec = %.2w
  FormatSpecOverTolerance = %+.2w
  FormatSpecUnderTolerance = %+.2w
  Inverted = false
  LineAngle = 0
  LockPosition = false
  MeasureType = 1
  OverTolerance = 0
  References2D = -> [View]
  Rotation = 0
  ScaleType = 0
  TheoreticalExact = false
  Type = 1
  UnderTolerance = 0
  X = 15.7775
  Y = -14.8137
FEATURE [TechDraw::DrawViewDimension] Dimension004
  AngleOverride = false
  Arbitrary = false
  ArbitraryTolerances = false
  EqualTolerance = true
  ExtensionAngle = 0
  FormatSpec = %.2w
  FormatSpecOverTolerance = %+.2w
  FormatSpecUnderTolerance = %+.2w
  Inverted = false
  LineAngle = 0
  LockPosition = false
  MeasureType = 1
  OverTolerance = 0
  References2D = -> [View]
  Rotation = 0
  ScaleType = 0
  TheoreticalExact = false
  Type = 1
  UnderTolerance = 0
  X = 1.18251
  Y = -21.3199
FEATURE [TechDraw::DrawViewAnnotation] Annotation
  Font = Droid Sans Mono
  LineSpace = 100
  LockPosition = false
  MaxWidth = -1
  Rotation = 0
  ScaleType = 0
  Text = Brass Wire, 0.8mm dia | length  = 4+4+2.8+2.8+51.95 | length = approx 66 mm long
  TextSize = 3
  TextStyle = 0
  X = 150.297
  Y = 144.338
FEATURE [TechDraw::DrawPage] Page
  KeepUpdated = true
  NextBalloonIndex = 1
  ProjectionType = 1
  Template = -> Template
  Views = -> [View,Dimension001,Dimension002,Dimension,Dimension003,Dimension004,Annotation]
FEATURE [Sketcher::SketchObject] Sketch019
  FullyConstrained = true
  MapMode = 5
  Placement = pos=(-27.1,7.1e-15,-1.82e-14) rot=(0.57735,-0.57735,-0.57735;2.0944rad)
  Support = -> [Fillet001]
  sketch-geometry (1):
    g0: Circle CenterX=0 CenterY=0 CenterZ=0 NormalX=0 NormalY=0 NormalZ=1 AngleXU=0 Radius=3.5
  constraints (2):
    c: Coincident(g0,g-1)
    c: Diameter(g0) = 7
FEATURE [PartDesign::Pocket] Pocket
  BaseFeature = -> Fillet001
  Direction = (1,-1e-16,5e-16)
  Length = 5
  Length2 = 5
  Placement = pos=(-24.3,8e-15,-1.4e-14) rot=(0.57735,-0.57735,-0.57735;2.0944rad)
  Profile = -> Sketch019
  ReferenceAxis = -> Sketch019 [N_Axis]
  Type = 1
FEATURE [PartDesign::Body] Body002  label="leg_right"
  Group = -> [Sketch001,Binder001,Binder004,DatumPlane003,Pad004,Fillet,Fillet001,Sketch019,Pocket]
  Origin = -> Origin003
  Tip = -> Pocket
FEATURE [PartDesign::FeatureBase] Clone006
  BaseFeature = -> Body002
FEATURE [PartDesign::Body] Body014  label="leg_left"
  Group = -> [Clone006]
  Origin = -> Origin016
  Placement = pos=(0,0,20) rot=(0,0,1;3.14159rad)
  Tip = -> Clone006
FEATURE [Part::Part2DObjectPython] Shape2DView007  label="leg_right_DXF"  # Draft 2D object (typed FeaturePython)
  AutoUpdate = true
  Base = -> Body002
  Clip = false
  FuseArch = false
  HiddenLines = false
  InPlace = true
  OnlySolids = false
  Projection = (-1,0,0)
  ProjectionMode = 0
  SegmentLength = 0.05
  Tessellation = false
  VisibleOnly = false
FEATURE [Part::Part2DObjectPython] Shape2DView011  label="leg_left_DXF"  # Draft 2D object (typed FeaturePython)
  AutoUpdate = true
  Base = -> Body014
  Clip = false
  FuseArch = false
  HiddenLines = false
  InPlace = true
  OnlySolids = false
  Projection = (1,0,0)
  ProjectionMode = 0
  SegmentLength = 0.05
  Tessellation = false
  VisibleOnly = false
FEATURE [Sketcher::SketchObject] Sketch020  label="Sketch_MuSo"
  AttachmentOffset = pos=(-8.7,-37,-84) rot=(0,0,1;-1.5708rad)
  FullyConstrained = false
  MapMode = 5
  Placement = pos=(12.7,-8.7,8.53e-14) rot=(0,0,1;0rad)
  Support = -> [Pocket]
  sketch-geometry (369):
    g0: BSplineCurve PolesCount=2 KnotsCount=2 Degree=1 IsPeriodic=0
    g1: BSplineCurve PolesCount=2 KnotsCount=2 Degree=1 IsPeriodic=0
    g2: BSplineCurve PolesCount=4 KnotsCount=2 Degree=3 IsPeriodic=0
    g3: BSplineCurve PolesCount=2 KnotsCount=2 Degree=1 IsPeriodic=0
    g4: BSplineCurve PolesCount=4 KnotsCount=2 Degree=3 IsPeriodic=0
    g5: BSplineCurve PolesCount=2 KnotsCount=2 Degree=1 IsPeriodic=0
    g6: BSplineCurve PolesCount=2 KnotsCount=2 Degree=1 IsPeriodic=0
    g7: BSplineCurve PolesCount=2 KnotsCount=2 Degree=1 IsPeriodic=0
    g8: BSplineCurve PolesCount=4 KnotsCount=2 Degree=3 IsPeriodic=0
    g9: BSplineCurve PolesCount=2 KnotsCount=2 Degree=1 IsPeriodic=0
    g10: BSplineCurve PolesCount=4 KnotsCount=2 Degree=3 IsPeriodic=0
    g11: BSplineCurve PolesCount=2 KnotsCount=2 Degree=1 IsPeriodic=0
    g12: BSplineCurve PolesCount=2 KnotsCount=2 Degree=1 IsPeriodic=0
    g13: BSplineCurve PolesCount=2 KnotsCount=2 Degree=1 IsPeriodic=0
    g14: BSplineCurve PolesCount=2 KnotsCount=2 Degree=1 IsPeriodic=0
    g15: BSplineCurve PolesCount=2 KnotsCount=2 Degree=1 IsPeriodic=0
    g16: BSplineCurve PolesCount=4 KnotsCount=2 Degree=3 IsPeriodic=0
    g17: BSplineCurve PolesCount=2 KnotsCount=2 Degree=1 IsPeriodic=0
    g18: BSplineCurve PolesCount=4 KnotsCount=2 Degree=3 IsPeriodic=0
    g19: BSplineCurve PolesCount=2 KnotsCount=2 Degree=1 IsPeriodic=0
    g20: BSplineCurve PolesCount=2 KnotsCount=2 Degree=1 IsPeriodic=0
    g21: BSplineCurve PolesCount=2 KnotsCount=2 Degree=1 IsPeriodic=0
    g22: BSplineCurve PolesCount=2 KnotsCount=2 Degree=1 IsPeriodic=0
    g23: BSplineCurve PolesCount=2 KnotsCount=2 Degree=1 IsPeriodic=0
    g24: BSplineCurve PolesCount=2 KnotsCount=2 Degree=1 IsPeriodic=0
    g25: BSplineCurve PolesCount=4 KnotsCount=2 Degree=3 IsPeriodic=0
    g26: BSplineCurve PolesCount=2 KnotsCount=2 Degree=1 IsPeriodic=0
    g27: BSplineCurve PolesCount=4 KnotsCount=2 Degree=3 IsPeriodic=0
    g28: BSplineCurve PolesCount=4 KnotsCount=2 Degree=3 IsPeriodic=0
    g29: BSplineCurve PolesCount=2 KnotsCount=2 Degree=1 IsPeriodic=0
    g30: BSplineCurve PolesCount=2 KnotsCount=2 Degree=1 IsPeriodic=0
    g31: BSplineCurve PolesCount=2 KnotsCount=2 Degree=1 IsPeriodic=0
    g32: BSplineCurve PolesCount=4 KnotsCount=2 Degree=3 IsPeriodic=0
    g33: BSplineCurve PolesCount=4 KnotsCount=2 Degree=3 IsPeriodic=0
    g34: BSplineCurve PolesCount=2 KnotsCount=2 Degree=1 IsPeriodic=0
    g35: BSplineCurve PolesCount=2 KnotsCount=2 Degree=1 IsPeriodic=0
    g36: BSplineCurve PolesCount=4 KnotsCount=2 Degree=3 IsPeriodic=0
    g37: BSplineCurve PolesCount=4 KnotsCount=2 Degree=3 IsPeriodic=0
    g38: BSplineCurve PolesCount=4 KnotsCount=2 Degree=3 IsPeriodic=0
    g39: BSplineCurve PolesCount=4 KnotsCount=2 Degree=3 IsPeriodic=0
    g40: BSplineCurve PolesCount=2 KnotsCount=2 Degree=1 IsPeriodic=0
    g41: BSplineCurve PolesCount=4 KnotsCount=2 Degree=3 IsPeriodic=0
    g42: BSplineCurve PolesCount=4 KnotsCount=2 Degree=3 IsPeriodic=0
    g43: BSplineCurve PolesCount=4 KnotsCount=2 Degree=3 IsPeriodic=0
    g44: BSplineCurve PolesCount=4 KnotsCount=2 Degree=3 IsPeriodic=0
    g45: BSplineCurve PolesCount=4 KnotsCount=2 Degree=3 IsPeriodic=0
    g46: BSplineCurve PolesCount=2 KnotsCount=2 Degree=1 IsPeriodic=0
    g47: BSplineCurve PolesCount=4 KnotsCount=2 Degree=3 IsPeriodic=0
    g48: BSplineCurve PolesCount=4 KnotsCount=2 Degree=3 IsPeriodic=0
    g49: BSplineCurve PolesCount=4 KnotsCount=2 Degree=3 IsPeriodic=0
    g50: BSplineCurve PolesCount=4 KnotsCount=2 Degree=3 IsPeriodic=0
    g51: BSplineCurve PolesCount=4 KnotsCount=2 Degree=3 IsPeriodic=0
    g52: BSplineCurve PolesCount=4 KnotsCount=2 Degree=3 IsPeriodic=0
    g53: BSplineCurve PolesCount=4 KnotsCount=2 Degree=3 IsPeriodic=0
    g54: BSplineCurve PolesCount=4 KnotsCount=2 Degree=3 IsPeriodic=0
    g55: BSplineCurve PolesCount=4 KnotsCount=2 Degree=3 IsPeriodic=0
    g56: BSplineCurve PolesCount=2 KnotsCount=2 Degree=1 IsPeriodic=0
    g57: BSplineCurve PolesCount=2 KnotsCount=2 Degree=1 IsPeriodic=0
    g58: BSplineCurve PolesCount=2 KnotsCount=2 Degree=1 IsPeriodic=0
    g59: BSplineCurve PolesCount=2 KnotsCount=2 Degree=1 IsPeriodic=0
    g60: BSplineCurve PolesCount=2 KnotsCount=2 Degree=1 IsPeriodic=0
    g61: BSplineCurve PolesCount=2 KnotsCount=2 Degree=1 IsPeriodic=0
    g62: BSplineCurve PolesCount=2 KnotsCount=2 Degree=1 IsPeriodic=0
    g63: BSplineCurve PolesCount=2 KnotsCount=2 Degree=1 IsPeriodic=0
    g64: BSplineCurve PolesCount=2 KnotsCount=2 Degree=1 IsPeriodic=0
    g65: BSplineCurve PolesCount=2 KnotsCount=2 Degree=1 IsPeriodic=0
    g66: BSplineCurve PolesCount=4 KnotsCount=2 Degree=3 IsPeriodic=0
    g67: BSplineCurve PolesCount=2 KnotsCount=2 Degree=1 IsPeriodic=0
    g68: BSplineCurve PolesCount=4 KnotsCount=2 Degree=3 IsPeriodic=0
    g69: BSplineCurve PolesCount=2 KnotsCount=2 Degree=1 IsPeriodic=0
    g70: BSplineCurve PolesCount=2 KnotsCount=2 Degree=1 IsPeriodic=0
    g71: BSplineCurve PolesCount=2 KnotsCount=2 Degree=1 IsPeriodic=0
    g72: BSplineCurve PolesCount=4 KnotsCount=2 Degree=3 IsPeriodic=0
    g73: BSplineCurve PolesCount=2 KnotsCount=2 Degree=1 IsPeriodic=0
    g74: BSplineCurve PolesCount=4 KnotsCount=2 Degree=3 IsPeriodic=0
    g75: BSplineCurve PolesCount=2 KnotsCount=2 Degree=1 IsPeriodic=0
    g76: BSplineCurve PolesCount=2 KnotsCount=2 Degree=1 IsPeriodic=0
    g77: BSplineCurve PolesCount=2 KnotsCount=2 Degree=1 IsPeriodic=0
    g78: BSplineCurve PolesCount=2 KnotsCount=2 Degree=1 IsPeriodic=0
    g79: BSplineCurve PolesCount=2 KnotsCount=2 Degree=1 IsPeriodic=0
    g80: BSplineCurve PolesCount=4 KnotsCount=2 Degree=3 IsPeriodic=0
    g81: BSplineCurve PolesCount=2 KnotsCount=2 Degree=1 IsPeriodic=0
    g82: BSplineCurve PolesCount=4 KnotsCount=2 Degree=3 IsPeriodic=0
    g83: BSplineCurve PolesCount=2 KnotsCount=2 Degree=1 IsPeriodic=0
    g84: BSplineCurve PolesCount=2 KnotsCount=2 Degree=1 IsPeriodic=0
    g85: BSplineCurve PolesCount=2 KnotsCount=2 Degree=1 IsPeriodic=0
    g86: BSplineCurve PolesCount=2 KnotsCount=2 Degree=1 IsPeriodic=0
    g87: BSplineCurve PolesCount=4 KnotsCount=2 Degree=3 IsPeriodic=0
    g88: BSplineCurve PolesCount=4 KnotsCount=2 Degree=3 IsPeriodic=0
    g89: BSplineCurve PolesCount=2 KnotsCount=2 Degree=1 IsPeriodic=0
    g90: BSplineCurve PolesCount=4 KnotsCount=2 Degree=3 IsPeriodic=0
    g91: BSplineCurve PolesCount=4 KnotsCount=2 Degree=3 IsPeriodic=0
    g92: BSplineCurve PolesCount=2 KnotsCount=2 Degree=1 IsPeriodic=0
    g93: BSplineCurve PolesCount=2 KnotsCount=2 Degree=1 IsPeriodic=0
    g94: BSplineCurve PolesCount=2 KnotsCount=2 Degree=1 IsPeriodic=0
    g95: BSplineCurve PolesCount=4 KnotsCount=2 Degree=3 IsPeriodic=0
    g96: BSplineCurve PolesCount=4 KnotsCount=2 Degree=3 IsPeriodic=0
    g97: BSplineCurve PolesCount=2 KnotsCount=2 Degree=1 IsPeriodic=0
    g98: BSplineCurve PolesCount=2 KnotsCount=2 Degree=1 IsPeriodic=0
    g99: BSplineCurve PolesCount=2 KnotsCount=2 Degree=1 IsPeriodic=0
    g100: BSplineCurve PolesCount=4 KnotsCount=2 Degree=3 IsPeriodic=0
    g101: BSplineCurve PolesCount=4 KnotsCount=2 Degree=3 IsPeriodic=0
    g102: BSplineCurve PolesCount=2 KnotsCount=2 Degree=1 IsPeriodic=0
    g103: BSplineCurve PolesCount=4 KnotsCount=2 Degree=3 IsPeriodic=0
    g104: BSplineCurve PolesCount=4 KnotsCount=2 Degree=3 IsPeriodic=0
    g105: BSplineCurve PolesCount=4 KnotsCount=2 Degree=3 IsPeriodic=0
    g106: BSplineCurve PolesCount=4 KnotsCount=2 Degree=3 IsPeriodic=0
    g107: BSplineCurve PolesCount=4 KnotsCount=2 Degree=3 IsPeriodic=0
    g108: BSplineCurve PolesCount=2 KnotsCount=2 Degree=1 IsPeriodic=0
    g109: BSplineCurve PolesCount=4 KnotsCount=2 Degree=3 IsPeriodic=0
    g110: BSplineCurve PolesCount=4 KnotsCount=2 Degree=3 IsPeriodic=0
    g111: BSplineCurve PolesCount=4 KnotsCount=2 Degree=3 IsPeriodic=0
    g112: BSplineCurve PolesCount=4 KnotsCount=2 Degree=3 IsPeriodic=0
    g113: BSplineCurve PolesCount=4 KnotsCount=2 Degree=3 IsPeriodic=0
    g114: BSplineCurve PolesCount=4 KnotsCount=2 Degree=3 IsPeriodic=0
    g115: BSplineCurve PolesCount=2 KnotsCount=2 Degree=1 IsPeriodic=0
    g116: BSplineCurve PolesCount=4 KnotsCount=2 Degree=3 IsPeriodic=0
    g117: BSplineCurve PolesCount=2 KnotsCount=2 Degree=1 IsPeriodic=0
    g118: BSplineCurve PolesCount=4 KnotsCount=2 Degree=3 IsPeriodic=0
    g119: BSplineCurve PolesCount=4 KnotsCount=2 Degree=3 IsPeriodic=0
    g120: BSplineCurve PolesCount=4 KnotsCount=2 Degree=3 IsPeriodic=0
    g121: BSplineCurve PolesCount=4 KnotsCount=2 Degree=3 IsPeriodic=0
    g122: BSplineCurve PolesCount=4 KnotsCount=2 Degree=3 IsPeriodic=0
    g123: BSplineCurve PolesCount=2 KnotsCount=2 Degree=1 IsPeriodic=0
    g124: BSplineCurve PolesCount=4 KnotsCount=2 Degree=3 IsPeriodic=0
    g125: BSplineCurve PolesCount=4 KnotsCount=2 Degree=3 IsPeriodic=0
    g126: BSplineCurve PolesCount=2 KnotsCount=2 Degree=1 IsPeriodic=0
    g127: BSplineCurve PolesCount=4 KnotsCount=2 Degree=3 IsPeriodic=0
    g128: BSplineCurve PolesCount=4 KnotsCount=2 Degree=3 IsPeriodic=0
    g129: BSplineCurve PolesCount=4 KnotsCount=2 Degree=3 IsPeriodic=0
    g130: BSplineCurve PolesCount=4 KnotsCount=2 Degree=3 IsPeriodic=0
    g131: BSplineCurve PolesCount=4 KnotsCount=2 Degree=3 IsPeriodic=0
    g132: BSplineCurve PolesCount=2 KnotsCount=2 Degree=1 IsPeriodic=0
    g133: BSplineCurve PolesCount=4 KnotsCount=2 Degree=3 IsPeriodic=0
    g134: BSplineCurve PolesCount=4 KnotsCount=2 Degree=3 IsPeriodic=0
    g135: BSplineCurve PolesCount=2 KnotsCount=2 Degree=1 IsPeriodic=0
    g136: BSplineCurve PolesCount=2 KnotsCount=2 Degree=1 IsPeriodic=0
    g137: BSplineCurve PolesCount=2 KnotsCount=2 Degree=1 IsPeriodic=0
    g138: BSplineCurve PolesCount=4 KnotsCount=2 Degree=3 IsPeriodic=0
    g139: BSplineCurve PolesCount=4 KnotsCount=2 Degree=3 IsPeriodic=0
    g140: BSplineCurve PolesCount=2 KnotsCount=2 Degree=1 IsPeriodic=0
    g141: BSplineCurve PolesCount=2 KnotsCount=2 Degree=1 IsPeriodic=0
    g142: BSplineCurve PolesCount=2 KnotsCount=2 Degree=1 IsPeriodic=0
    g143: BSplineCurve PolesCount=4 KnotsCount=2 Degree=3 IsPeriodic=0
    g144: BSplineCurve PolesCount=4 KnotsCount=2 Degree=3 IsPeriodic=0
    g145: BSplineCurve PolesCount=2 KnotsCount=2 Degree=1 IsPeriodic=0
    g146: BSplineCurve PolesCount=4 KnotsCount=2 Degree=3 IsPeriodic=0
    g147: BSplineCurve PolesCount=4 KnotsCount=2 Degree=3 IsPeriodic=0
    g148: BSplineCurve PolesCount=2 KnotsCount=2 Degree=1 IsPeriodic=0
    g149: BSplineCurve PolesCount=4 KnotsCount=2 Degree=3 IsPeriodic=0
    g150: BSplineCurve PolesCount=4 KnotsCount=2 Degree=3 IsPeriodic=0
    g151: BSplineCurve PolesCount=2 KnotsCount=2 Degree=1 IsPeriodic=0
    g152: BSplineCurve PolesCount=2 KnotsCount=2 Degree=1 IsPeriodic=0
    g153: BSplineCurve PolesCount=2 KnotsCount=2 Degree=1 IsPeriodic=0
    g154: BSplineCurve PolesCount=4 KnotsCount=2 Degree=3 IsPeriodic=0
    g155: BSplineCurve PolesCount=4 KnotsCount=2 Degree=3 IsPeriodic=0
    g156: BSplineCurve PolesCount=2 KnotsCount=2 Degree=1 IsPeriodic=0
    g157: BSplineCurve PolesCount=2 KnotsCount=2 Degree=1 IsPeriodic=0
    g158: BSplineCurve PolesCount=2 KnotsCount=2 Degree=1 IsPeriodic=0
    g159: BSplineCurve PolesCount=2 KnotsCount=2 Degree=1 IsPeriodic=0
    g160: BSplineCurve PolesCount=4 KnotsCount=2 Degree=3 IsPeriodic=0
    g161: BSplineCurve PolesCount=2 KnotsCount=2 Degree=1 IsPeriodic=0
    g162: BSplineCurve PolesCount=4 KnotsCount=2 Degree=3 IsPeriodic=0
    g163: BSplineCurve PolesCount=4 KnotsCount=2 Degree=3 IsPeriodic=0
    g164: BSplineCurve PolesCount=4 KnotsCount=2 Degree=3 IsPeriodic=0
    g165: BSplineCurve PolesCount=4 KnotsCount=2 Degree=3 IsPeriodic=0
    g166: BSplineCurve PolesCount=2 KnotsCount=2 Degree=1 IsPeriodic=0
    g167: BSplineCurve PolesCount=4 KnotsCount=2 Degree=3 IsPeriodic=0
    g168: BSplineCurve PolesCount=4 KnotsCount=2 Degree=3 IsPeriodic=0
    g169: BSplineCurve PolesCount=2 KnotsCount=2 Degree=1 IsPeriodic=0
    g170: BSplineCurve PolesCount=4 KnotsCount=2 Degree=3 IsPeriodic=0
    g171: BSplineCurve PolesCount=4 KnotsCount=2 Degree=3 IsPeriodic=0
    g172: BSplineCurve PolesCount=4 KnotsCount=2 Degree=3 IsPeriodic=0
    g173: BSplineCurve PolesCount=4 KnotsCount=2 Degree=3 IsPeriodic=0
    g174: BSplineCurve PolesCount=4 KnotsCount=2 Degree=3 IsPeriodic=0
    g175: BSplineCurve PolesCount=4 KnotsCount=2 Degree=3 IsPeriodic=0
    g176: BSplineCurve PolesCount=4 KnotsCount=2 Degree=3 IsPeriodic=0
    g177: BSplineCurve PolesCount=4 KnotsCount=2 Degree=3 IsPeriodic=0
    g178: BSplineCurve PolesCount=2 KnotsCount=2 Degree=1 IsPeriodic=0
    g179: BSplineCurve PolesCount=2 KnotsCount=2 Degree=1 IsPeriodic=0
    g180: BSplineCurve PolesCount=2 KnotsCount=2 Degree=1 IsPeriodic=0
    g181: BSplineCurve PolesCount=2 KnotsCount=2 Degree=1 IsPeriodic=0
    g182: BSplineCurve PolesCount=2 KnotsCount=2 Degree=1 IsPeriodic=0
    g183: BSplineCurve PolesCount=2 KnotsCount=2 Degree=1 IsPeriodic=0
    g184: BSplineCurve PolesCount=2 KnotsCount=2 Degree=1 IsPeriodic=0
    g185: BSplineCurve PolesCount=2 KnotsCount=2 Degree=1 IsPeriodic=0
    g186: BSplineCurve PolesCount=2 KnotsCount=2 Degree=1 IsPeriodic=0
    g187: BSplineCurve PolesCount=2 KnotsCount=2 Degree=1 IsPeriodic=0
    g188: BSplineCurve PolesCount=4 KnotsCount=2 Degree=3 IsPeriodic=0
    g189: BSplineCurve PolesCount=4 KnotsCount=2 Degree=3 IsPeriodic=0
    g190: BSplineCurve PolesCount=2 KnotsCount=2 Degree=1 IsPeriodic=0
    g191: BSplineCurve PolesCount=4 KnotsCount=2 Degree=3 IsPeriodic=0
    g192: BSplineCurve PolesCount=4 KnotsCount=2 Degree=3 IsPeriodic=0
    g193: BSplineCurve PolesCount=2 KnotsCount=2 Degree=1 IsPeriodic=0
    g194: BSplineCurve PolesCount=4 KnotsCount=2 Degree=3 IsPeriodic=0
    g195: BSplineCurve PolesCount=4 KnotsCount=2 Degree=3 IsPeriodic=0
    g196: BSplineCurve PolesCount=4 KnotsCount=2 Degree=3 IsPeriodic=0
    g197: BSplineCurve PolesCount=4 KnotsCount=2 Degree=3 IsPeriodic=0
    g198: BSplineCurve PolesCount=2 KnotsCount=2 Degree=1 IsPeriodic=0
    g199: BSplineCurve PolesCount=4 KnotsCount=2 Degree=3 IsPeriodic=0
    g200: BSplineCurve PolesCount=4 KnotsCount=2 Degree=3 IsPeriodic=0
    g201: BSplineCurve PolesCount=4 KnotsCount=2 Degree=3 IsPeriodic=0
    g202: BSplineCurve PolesCount=4 KnotsCount=2 Degree=3 IsPeriodic=0
    g203: BSplineCurve PolesCount=4 KnotsCount=2 Degree=3 IsPeriodic=0
    g204: BSplineCurve PolesCount=2 KnotsCount=2 Degree=1 IsPeriodic=0
    g205: BSplineCurve PolesCount=4 KnotsCount=2 Degree=3 IsPeriodic=0
    g206: BSplineCurve PolesCount=4 KnotsCount=2 Degree=3 IsPeriodic=0
    g207: BSplineCurve PolesCount=4 KnotsCount=2 Degree=3 IsPeriodic=0
    g208: BSplineCurve PolesCount=4 KnotsCount=2 Degree=3 IsPeriodic=0
    g209: BSplineCurve PolesCount=4 KnotsCount=2 Degree=3 IsPeriodic=0
    g210: BSplineCurve PolesCount=4 KnotsCount=2 Degree=3 IsPeriodic=0
    g211: BSplineCurve PolesCount=4 KnotsCount=2 Degree=3 IsPeriodic=0
    g212: BSplineCurve PolesCount=4 KnotsCount=2 Degree=3 IsPeriodic=0
    g213: BSplineCurve PolesCount=4 KnotsCount=2 Degree=3 IsPeriodic=0
    g214: BSplineCurve PolesCount=2 KnotsCount=2 Degree=1 IsPeriodic=0
    g215: BSplineCurve PolesCount=2 KnotsCount=2 Degree=1 IsPeriodic=0
    g216: BSplineCurve PolesCount=2 KnotsCount=2 Degree=1 IsPeriodic=0
    g217: BSplineCurve PolesCount=2 KnotsCount=2 Degree=1 IsPeriodic=0
    g218: BSplineCurve PolesCount=4 KnotsCount=2 Degree=3 IsPeriodic=0
    g219: BSplineCurve PolesCount=4 KnotsCount=2 Degree=3 IsPeriodic=0
    g220: BSplineCurve PolesCount=2 KnotsCount=2 Degree=1 IsPeriodic=0
    g221: BSplineCurve PolesCount=4 KnotsCount=2 Degree=3 IsPeriodic=0
    g222: BSplineCurve PolesCount=4 KnotsCount=2 Degree=3 IsPeriodic=0
    g223: BSplineCurve PolesCount=2 KnotsCount=2 Degree=1 IsPeriodic=0
    g224: BSplineCurve PolesCount=2 KnotsCount=2 Degree=1 IsPeriodic=0
    g225: BSplineCurve PolesCount=2 KnotsCount=2 Degree=1 IsPeriodic=0
    g226: BSplineCurve PolesCount=4 KnotsCount=2 Degree=3 IsPeriodic=0
    g227: BSplineCurve PolesCount=4 KnotsCount=2 Degree=3 IsPeriodic=0
    g228: BSplineCurve PolesCount=2 KnotsCount=2 Degree=1 IsPeriodic=0
    g229: BSplineCurve PolesCount=2 KnotsCount=2 Degree=1 IsPeriodic=0
    g230: BSplineCurve PolesCount=2 KnotsCount=2 Degree=1 IsPeriodic=0
    g231: BSplineCurve PolesCount=4 KnotsCount=2 Degree=3 IsPeriodic=0
    g232: BSplineCurve PolesCount=4 KnotsCount=2 Degree=3 IsPeriodic=0
    g233: BSplineCurve PolesCount=2 KnotsCount=2 Degree=1 IsPeriodic=0
    g234: BSplineCurve PolesCount=4 KnotsCount=2 Degree=3 IsPeriodic=0
    g235: BSplineCurve PolesCount=4 KnotsCount=2 Degree=3 IsPeriodic=0
    g236: BSplineCurve PolesCount=2 KnotsCount=2 Degree=1 IsPeriodic=0
    g237: BSplineCurve PolesCount=2 KnotsCount=2 Degree=1 IsPeriodic=0
    g238: BSplineCurve PolesCount=2 KnotsCount=2 Degree=1 IsPeriodic=0
    g239: BSplineCurve PolesCount=2 KnotsCount=2 Degree=1 IsPeriodic=0
    g240: BSplineCurve PolesCount=2 KnotsCount=2 Degree=1 IsPeriodic=0
    g241: BSplineCurve PolesCount=2 KnotsCount=2 Degree=1 IsPeriodic=0
    g242: BSplineCurve PolesCount=2 KnotsCount=2 Degree=1 IsPeriodic=0
    g243: BSplineCurve PolesCount=2 KnotsCount=2 Degree=1 IsPeriodic=0
    g244: BSplineCurve PolesCount=2 KnotsCount=2 Degree=1 IsPeriodic=0
    g245: BSplineCurve PolesCount=2 KnotsCount=2 Degree=1 IsPeriodic=0
    g246: BSplineCurve PolesCount=2 KnotsCount=2 Degree=1 IsPeriodic=0
    g247: BSplineCurve PolesCount=4 KnotsCount=2 Degree=3 IsPeriodic=0
    g248: BSplineCurve PolesCount=4 KnotsCount=2 Degree=3 IsPeriodic=0
    g249: BSplineCurve PolesCount=2 KnotsCount=2 Degree=1 IsPeriodic=0
    g250: BSplineCurve PolesCount=4 KnotsCount=2 Degree=3 IsPeriodic=0
    g251: BSplineCurve PolesCount=4 KnotsCount=2 Degree=3 IsPeriodic=0
    g252: BSplineCurve PolesCount=4 KnotsCount=2 Degree=3 IsPeriodic=0
    g253: BSplineCurve PolesCount=4 KnotsCount=2 Degree=3 IsPeriodic=0
    g254: BSplineCurve PolesCount=2 KnotsCount=2 Degree=1 IsPeriodic=0
    g255: BSplineCurve PolesCount=2 KnotsCount=2 Degree=1 IsPeriodic=0
    g256: BSplineCurve PolesCount=2 KnotsCount=2 Degree=1 IsPeriodic=0
    g257: BSplineCurve PolesCount=2 KnotsCount=2 Degree=1 IsPeriodic=0
    g258: BSplineCurve PolesCount=4 KnotsCount=2 Degree=3 IsPeriodic=0
    g259: BSplineCurve PolesCount=4 KnotsCount=2 Degree=3 IsPeriodic=0
    g260: BSplineCurve PolesCount=4 KnotsCount=2 Degree=3 IsPeriodic=0
    g261: BSplineCurve PolesCount=4 KnotsCount=2 Degree=3 IsPeriodic=0
    g262: BSplineCurve PolesCount=4 KnotsCount=2 Degree=3 IsPeriodic=0
    g263: BSplineCurve PolesCount=4 KnotsCount=2 Degree=3 IsPeriodic=0
    g264: BSplineCurve PolesCount=4 KnotsCount=2 Degree=3 IsPeriodic=0
    g265: BSplineCurve PolesCount=4 KnotsCount=2 Degree=3 IsPeriodic=0
    g266: BSplineCurve PolesCount=4 KnotsCount=2 Degree=3 IsPeriodic=0
    g267: BSplineCurve PolesCount=4 KnotsCount=2 Degree=3 IsPeriodic=0
    g268: BSplineCurve PolesCount=2 KnotsCount=2 Degree=1 IsPeriodic=0
    g269: BSplineCurve PolesCount=4 KnotsCount=2 Degree=3 IsPeriodic=0
    g270: BSplineCurve PolesCount=4 KnotsCount=2 Degree=3 IsPeriodic=0
    g271: BSplineCurve PolesCount=2 KnotsCount=2 Degree=1 IsPeriodic=0
    g272: BSplineCurve PolesCount=2 KnotsCount=2 Degree=1 IsPeriodic=0
    g273: BSplineCurve PolesCount=2 KnotsCount=2 Degree=1 IsPeriodic=0
    g274: BSplineCurve PolesCount=2 KnotsCount=2 Degree=1 IsPeriodic=0
    g275: BSplineCurve PolesCount=4 KnotsCount=2 Degree=3 IsPeriodic=0
    g276: BSplineCurve PolesCount=2 KnotsCount=2 Degree=1 IsPeriodic=0
    g277: BSplineCurve PolesCount=4 KnotsCount=2 Degree=3 IsPeriodic=0
    g278: BSplineCurve PolesCount=4 KnotsCount=2 Degree=3 IsPeriodic=0
    g279: BSplineCurve PolesCount=2 KnotsCount=2 Degree=1 IsPeriodic=0
    g280: BSplineCurve PolesCount=4 KnotsCount=2 Degree=3 IsPeriodic=0
    g281: BSplineCurve PolesCount=4 KnotsCount=2 Degree=3 IsPeriodic=0
    g282: BSplineCurve PolesCount=2 KnotsCount=2 Degree=1 IsPeriodic=0
    g283: BSplineCurve PolesCount=4 KnotsCount=2 Degree=3 IsPeriodic=0
    g284: BSplineCurve PolesCount=4 KnotsCount=2 Degree=3 IsPeriodic=0
    g285: BSplineCurve PolesCount=4 KnotsCount=2 Degree=3 IsPeriodic=0
    g286: BSplineCurve PolesCount=4 KnotsCount=2 Degree=3 IsPeriodic=0
    g287: BSplineCurve PolesCount=4 KnotsCount=2 Degree=3 IsPeriodic=0
    g288: BSplineCurve PolesCount=2 KnotsCount=2 Degree=1 IsPeriodic=0
    g289: BSplineCurve PolesCount=4 KnotsCount=2 Degree=3 IsPeriodic=0
    g290: BSplineCurve PolesCount=4 KnotsCount=2 Degree=3 IsPeriodic=0
    g291: BSplineCurve PolesCount=4 KnotsCount=2 Degree=3 IsPeriodic=0
    g292: BSplineCurve PolesCount=4 KnotsCount=2 Degree=3 IsPeriodic=0
    g293: BSplineCurve PolesCount=4 KnotsCount=2 Degree=3 IsPeriodic=0
    g294: BSplineCurve PolesCount=4 KnotsCount=2 Degree=3 IsPeriodic=0
    g295: BSplineCurve PolesCount=2 KnotsCount=2 Degree=1 IsPeriodic=0
    g296: BSplineCurve PolesCount=4 KnotsCount=2 Degree=3 IsPeriodic=0
    g297: BSplineCurve PolesCount=4 KnotsCount=2 Degree=3 IsPeriodic=0
    g298: BSplineCurve PolesCount=4 KnotsCount=2 Degree=3 IsPeriodic=0
    g299: BSplineCurve PolesCount=4 KnotsCount=2 Degree=3 IsPeriodic=0
    g300: BSplineCurve PolesCount=4 KnotsCount=2 Degree=3 IsPeriodic=0
    g301: BSplineCurve PolesCount=4 KnotsCount=2 Degree=3 IsPeriodic=0
    g302: BSplineCurve PolesCount=4 KnotsCount=2 Degree=3 IsPeriodic=0
    g303: BSplineCurve PolesCount=4 KnotsCount=2 Degree=3 IsPeriodic=0
    g304: BSplineCurve PolesCount=4 KnotsCount=2 Degree=3 IsPeriodic=0
    g305: BSplineCurve PolesCount=4 KnotsCount=2 Degree=3 IsPeriodic=0
    g306: BSplineCurve PolesCount=4 KnotsCount=2 Degree=3 IsPeriodic=0
    g307: BSplineCurve PolesCount=4 KnotsCount=2 Degree=3 IsPeriodic=0
    g308: BSplineCurve PolesCount=4 KnotsCount=2 Degree=3 IsPeriodic=0
    g309: BSplineCurve PolesCount=4 KnotsCount=2 Degree=3 IsPeriodic=0
    g310: BSplineCurve PolesCount=4 KnotsCount=2 Degree=3 IsPeriodic=0
    g311: BSplineCurve PolesCount=4 KnotsCount=2 Degree=3 IsPeriodic=0
    g312: BSplineCurve PolesCount=4 KnotsCount=2 Degree=3 IsPeriodic=0
    g313: BSplineCurve PolesCount=4 KnotsCount=2 Degree=3 IsPeriodic=0
    g314: BSplineCurve PolesCount=4 KnotsCount=2 Degree=3 IsPeriodic=0
    g315: BSplineCurve PolesCount=4 KnotsCount=2 Degree=3 IsPeriodic=0
    g316: BSplineCurve PolesCount=4 KnotsCount=2 Degree=3 IsPeriodic=0
    g317: BSplineCurve PolesCount=4 KnotsCount=2 Degree=3 IsPeriodic=0
    g318: BSplineCurve PolesCount=4 KnotsCount=2 Degree=3 IsPeriodic=0
    g319: BSplineCurve PolesCount=4 KnotsCount=2 Degree=3 IsPeriodic=0
    g320: BSplineCurve PolesCount=4 KnotsCount=2 Degree=3 IsPeriodic=0
    g321: BSplineCurve PolesCount=4 KnotsCount=2 Degree=3 IsPeriodic=0
    g322: BSplineCurve PolesCount=4 KnotsCount=2 Degree=3 IsPeriodic=0
    g323: BSplineCurve PolesCount=4 KnotsCount=2 Degree=3 IsPeriodic=0
    g324: BSplineCurve PolesCount=4 KnotsCount=2 Degree=3 IsPeriodic=0
    g325: BSplineCurve PolesCount=4 KnotsCount=2 Degree=3 IsPeriodic=0
    g326: BSplineCurve PolesCount=2 KnotsCount=2 Degree=1 IsPeriodic=0
    g327: BSplineCurve PolesCount=4 KnotsCount=2 Degree=3 IsPeriodic=0
    g328: BSplineCurve PolesCount=4 KnotsCount=2 Degree=3 IsPeriodic=0
    g329: BSplineCurve PolesCount=4 KnotsCount=2 Degree=3 IsPeriodic=0
    g330: BSplineCurve PolesCount=4 KnotsCount=2 Degree=3 IsPeriodic=0
    g331: BSplineCurve PolesCount=4 KnotsCount=2 Degree=3 IsPeriodic=0
    g332: BSplineCurve PolesCount=4 KnotsCount=2 Degree=3 IsPeriodic=0
    g333: BSplineCurve PolesCount=4 KnotsCount=2 Degree=3 IsPeriodic=0
    g334: BSplineCurve PolesCount=4 KnotsCount=2 Degree=3 IsPeriodic=0
    g335: BSplineCurve PolesCount=4 KnotsCount=2 Degree=3 IsPeriodic=0
    g336: BSplineCurve PolesCount=2 KnotsCount=2 Degree=1 IsPeriodic=0
    g337: BSplineCurve PolesCount=4 KnotsCount=2 Degree=3 IsPeriodic=0
    g338: BSplineCurve PolesCount=4 KnotsCount=2 Degree=3 IsPeriodic=0
    g339: BSplineCurve PolesCount=4 KnotsCount=2 Degree=3 IsPeriodic=0
    g340: BSplineCurve PolesCount=4 KnotsCount=2 Degree=3 IsPeriodic=0
    g341: BSplineCurve PolesCount=4 KnotsCount=2 Degree=3 IsPeriodic=0
    g342: BSplineCurve PolesCount=4 KnotsCount=2 Degree=3 IsPeriodic=0
    g343: BSplineCurve PolesCount=4 KnotsCount=2 Degree=3 IsPeriodic=0
    g344: BSplineCurve PolesCount=4 KnotsCount=2 Degree=3 IsPeriodic=0
    g345: BSplineCurve PolesCount=4 KnotsCount=2 Degree=3 IsPeriodic=0
    g346: BSplineCurve PolesCount=4 KnotsCount=2 Degree=3 IsPeriodic=0
    g347: BSplineCurve PolesCount=4 KnotsCount=2 Degree=3 IsPeriodic=0
    g348: BSplineCurve PolesCount=4 KnotsCount=2 Degree=3 IsPeriodic=0
    g349: BSplineCurve PolesCount=4 KnotsCount=2 Degree=3 IsPeriodic=0
    g350: BSplineCurve PolesCount=4 KnotsCount=2 Degree=3 IsPeriodic=0
    g351: BSplineCurve PolesCount=4 KnotsCount=2 Degree=3 IsPeriodic=0
    g352: BSplineCurve PolesCount=4 KnotsCount=2 Degree=3 IsPeriodic=0
    g353: BSplineCurve PolesCount=4 KnotsCount=2 Degree=3 IsPeriodic=0
    g354: BSplineCurve PolesCount=4 KnotsCount=2 Degree=3 IsPeriodic=0
    g355: BSplineCurve PolesCount=4 KnotsCount=2 Degree=3 IsPeriodic=0
    g356: BSplineCurve PolesCount=4 KnotsCount=2 Degree=3 IsPeriodic=0
    g357: BSplineCurve PolesCount=4 KnotsCount=2 Degree=3 IsPeriodic=0
    g358: BSplineCurve PolesCount=4 KnotsCount=2 Degree=3 IsPeriodic=0
    g359: BSplineCurve PolesCount=4 KnotsCount=2 Degree=3 IsPeriodic=0
    g360: BSplineCurve PolesCount=4 KnotsCount=2 Degree=3 IsPeriodic=0
    g361: BSplineCurve PolesCount=4 KnotsCount=2 Degree=3 IsPeriodic=0
    g362: BSplineCurve PolesCount=4 KnotsCount=2 Degree=3 IsPeriodic=0
    g363: BSplineCurve PolesCount=4 KnotsCount=2 Degree=3 IsPeriodic=0
    g364: BSplineCurve PolesCount=4 KnotsCount=2 Degree=3 IsPeriodic=0
    g365: BSplineCurve PolesCount=4 KnotsCount=2 Degree=3 IsPeriodic=0
    g366: BSplineCurve PolesCount=4 KnotsCount=2 Degree=3 IsPeriodic=0
    g367: BSplineCurve PolesCount=4 KnotsCount=2 Degree=3 IsPeriodic=0
    g368: BSplineCurve PolesCount=4 KnotsCount=2 Degree=3 IsPeriodic=0
  constraints (369):
    c: Coincident(g0,g1)
    c: Coincident(g1,g2)
    c: Coincident(g2,g3)
    c: Coincident(g3,g4)
    c: Coincident(g4,g5)
    c: Coincident(g5,g6)
    c: Coincident(g6,g7)
    c: Coincident(g7,g8)
    c: Coincident(g8,g9)
    c: Coincident(g9,g10)
    c: Coincident(g10,g11)
    c: Coincident(g11,g12)
    c: Coincident(g12,g13)
    c: Coincident(g13,g14)
    c: Coincident(g14,g15)
    c: Coincident(g15,g16)
    c: Coincident(g16,g17)
    c: Coincident(g17,g18)
    c: Coincident(g18,g19)
    c: Coincident(g19,g20)
    c: Coincident(g20,g21)
    c: Coincident(g21,g22)
    c: Coincident(g22,g0)
    c: Coincident(g23,g24)
    c: Coincident(g24,g25)
    c: Coincident(g25,g26)
    c: Coincident(g26,g27)
    c: Coincident(g27,g28)
    c: Coincident(g28,g29)
    c: Coincident(g29,g30)
    c: Coincident(g30,g31)
    c: Coincident(g31,g32)
    c: Coincident(g32,g33)
    c: Coincident(g33,g34)
    c: Coincident(g34,g35)
    c: Coincident(g35,g23)
    c: Coincident(g36,g37)
    c: Coincident(g37,g38)
    c: Coincident(g38,g39)
    c: Coincident(g39,g40)
    c: Coincident(g40,g41)
    c: Coincident(g41,g42)
    c: Coincident(g42,g43)
    c: Coincident(g43,g44)
    c: Coincident(g44,g45)
    c: Coincident(g45,g46)
    c: Coincident(g46,g47)
    c: Coincident(g47,g36)
    c: Coincident(g48,g49)
    c: Coincident(g49,g50)
    c: Coincident(g50,g51)
    c: Coincident(g51,g48)
    c: Coincident(g52,g53)
    c: Coincident(g53,g54)
    c: Coincident(g54,g55)
    c: Coincident(g55,g52)
    c: Coincident(g56,g57)
    c: Coincident(g57,g58)
    c: Coincident(g58,g59)
    c: Coincident(g59,g56)
    c: Coincident(g60,g61)
    c: Coincident(g61,g62)
    c: Coincident(g62,g63)
    c: Coincident(g63,g60)
    c: Coincident(g64,g65)
    c: Coincident(g65,g66)
    c: Coincident(g66,g67)
    c: Coincident(g67,g68)
    c: Coincident(g68,g69)
    c: Coincident(g69,g70)
    c: Coincident(g70,g71)
    c: Coincident(g71,g72)
    c: Coincident(g72,g73)
    c: Coincident(g73,g74)
    c: Coincident(g74,g75)
    c: Coincident(g75,g76)
    c: Coincident(g76,g77)
    c: Coincident(g77,g78)
    c: Coincident(g78,g79)
    c: Coincident(g79,g80)
    c: Coincident(g80,g81)
    c: Coincident(g81,g82)
    c: Coincident(g82,g83)
    c: Coincident(g83,g84)
    c: Coincident(g84,g85)
    c: Coincident(g85,g86)
    c: Coincident(g86,g64)
    c: Coincident(g87,g88)
    c: Coincident(g88,g89)
    c: Coincident(g89,g90)
    c: Coincident(g90,g91)
    c: Coincident(g91,g92)
    c: Coincident(g92,g93)
    c: Coincident(g93,g94)
    c: Coincident(g94,g95)
    c: Coincident(g95,g96)
    c: Coincident(g96,g97)
    c: Coincident(g97,g98)
    c: Coincident(g98,g99)
    c: Coincident(g99,g100)
    c: Coincident(g100,g101)
    c: Coincident(g101,g102)
    c: Coincident(g102,g87)
    c: Coincident(g103,g104)
    c: Coincident(g104,g105)
    c: Coincident(g105,g106)
    c: Coincident(g106,g107)
    c: Coincident(g107,g108)
    c: Coincident(g108,g109)
    c: Coincident(g109,g110)
    c: Coincident(g110,g111)
    c: Coincident(g111,g112)
    c: Coincident(g112,g113)
    c: Coincident(g113,g114)
    c: Coincident(g114,g115)
    c: Coincident(g115,g116)
    c: Coincident(g116,g103)
    c: Coincident(g117,g118)
    c: Coincident(g118,g119)
    c: Coincident(g119,g120)
    c: Coincident(g120,g121)
    c: Coincident(g121,g122)
    c: Coincident(g122,g123)
    c: Coincident(g123,g124)
    c: Coincident(g124,g125)
    c: Coincident(g125,g117)
    c: Coincident(g126,g127)
    c: Coincident(g127,g128)
    c: Coincident(g128,g129)
    c: Coincident(g129,g126)
    c: Coincident(g130,g131)
    c: Coincident(g131,g132)
    c: Coincident(g132,g133)
    c: Coincident(g133,g134)
    c: Coincident(g134,g135)
    c: Coincident(g135,g136)
    c: Coincident(g136,g137)
    c: Coincident(g137,g138)
    c: Coincident(g138,g139)
    c: Coincident(g139,g140)
    c: Coincident(g140,g141)
    c: Coincident(g141,g142)
    c: Coincident(g142,g143)
    c: Coincident(g143,g144)
    c: Coincident(g144,g145)
    c: Coincident(g145,g130)
    c: Coincident(g146,g147)
    c: Coincident(g147,g148)
    c: Coincident(g148,g149)
    c: Coincident(g149,g150)
    c: Coincident(g150,g151)
    c: Coincident(g151,g152)
    c: Coincident(g152,g153)
    c: Coincident(g153,g154)
    c: Coincident(g154,g155)
    c: Coincident(g155,g156)
    c: Coincident(g156,g157)
    c: Coincident(g157,g158)
    c: Coincident(g158,g159)
    c: Coincident(g159,g160)
    c: Coincident(g160,g161)
    c: Coincident(g161,g162)
    c: Coincident(g162,g163)
    c: Coincident(g163,g164)
    c: Coincident(g164,g165)
    c: Coincident(g165,g166)
    c: Coincident(g166,g167)
    c: Coincident(g167,g168)
    c: Coincident(g168,g169)
    c: Coincident(g169,g146)
    c: Coincident(g170,g171)
    c: Coincident(g171,g172)
    c: Coincident(g172,g173)
    c: Coincident(g173,g170)
    c: Coincident(g174,g175)
    c: Coincident(g175,g176)
    c: Coincident(g176,g177)
    c: Coincident(g177,g174)
    c: Coincident(g178,g179)
    c: Coincident(g179,g180)
    c: Coincident(g180,g181)
    c: Coincident(g181,g182)
    c: Coincident(g182,g183)
    c: Coincident(g183,g184)
    c: Coincident(g184,g185)
    c: Coincident(g185,g186)
    c: Coincident(g186,g187)
    c: Coincident(g187,g188)
    c: Coincident(g188,g189)
    c: Coincident(g189,g190)
    c: Coincident(g190,g191)
    c: Coincident(g191,g192)
    c: Coincident(g192,g193)
    c: Coincident(g193,g178)
    c: Coincident(g194,g195)
    c: Coincident(g195,g196)
    c: Coincident(g196,g197)
    c: Coincident(g197,g198)
    c: Coincident(g198,g199)
    c: Coincident(g199,g200)
    c: Coincident(g200,g201)
    c: Coincident(g201,g202)
    c: Coincident(g202,g203)
    c: Coincident(g203,g204)
    c: Coincident(g204,g205)
    c: Coincident(g205,g194)
    c: Coincident(g206,g207)
    c: Coincident(g207,g208)
    c: Coincident(g208,g209)
    c: Coincident(g209,g206)
    c: Coincident(g210,g211)
    c: Coincident(g211,g212)
    c: Coincident(g212,g213)
    c: Coincident(g213,g210)
    c: Coincident(g214,g215)
    c: Coincident(g215,g216)
    c: Coincident(g216,g217)
    c: Coincident(g217,g214)
    c: Coincident(g218,g219)
    c: Coincident(g219,g220)
    c: Coincident(g220,g221)
    c: Coincident(g221,g222)
    c: Coincident(g222,g223)
    c: Coincident(g223,g224)
    c: Coincident(g224,g225)
    c: Coincident(g225,g226)
    c: Coincident(g226,g227)
    c: Coincident(g227,g228)
    c: Coincident(g228,g229)
    c: Coincident(g229,g230)
    c: Coincident(g230,g231)
    c: Coincident(g231,g232)
    c: Coincident(g232,g233)
    c: Coincident(g233,g218)
    c: Coincident(g234,g235)
    c: Coincident(g235,g236)
    c: Coincident(g236,g237)
    c: Coincident(g237,g238)
    c: Coincident(g238,g239)
    c: Coincident(g239,g240)
    c: Coincident(g240,g241)
    c: Coincident(g241,g242)
    c: Coincident(g242,g243)
    c: Coincident(g243,g244)
    c: Coincident(g244,g245)
    c: Coincident(g245,g246)
    c: Coincident(g246,g247)
    c: Coincident(g247,g248)
    c: Coincident(g248,g249)
    c: Coincident(g249,g234)
    c: Coincident(g250,g251)
    c: Coincident(g251,g252)
    c: Coincident(g252,g253)
    c: Coincident(g253,g250)
    c: Coincident(g254,g255)
    c: Coincident(g255,g256)
    c: Coincident(g256,g257)
    c: Coincident(g257,g254)
    c: Coincident(g258,g259)
    c: Coincident(g259,g260)
    c: Coincident(g260,g261)
    c: Coincident(g261,g258)
    c: Coincident(g262,g263)
    c: Coincident(g263,g264)
    c: Coincident(g264,g265)
    c: Coincident(g265,g262)
    c: Coincident(g266,g267)
    c: Coincident(g267,g268)
    c: Coincident(g268,g269)
    c: Coincident(g269,g270)
    c: Coincident(g270,g271)
    c: Coincident(g271,g272)
    c: Coincident(g272,g273)
    c: Coincident(g273,g274)
    c: Coincident(g274,g275)
    c: Coincident(g275,g276)
    c: Coincident(g276,g277)
    c: Coincident(g277,g278)
    c: Coincident(g278,g279)
    c: Coincident(g279,g280)
    c: Coincident(g280,g281)
    c: Coincident(g281,g282)
    c: Coincident(g282,g266)
    c: Coincident(g283,g284)
    c: Coincident(g284,g285)
    c: Coincident(g285,g286)
    c: Coincident(g286,g287)
    c: Coincident(g287,g288)
    c: Coincident(g288,g289)
    c: Coincident(g289,g290)
    c: Coincident(g290,g291)
    c: Coincident(g291,g292)
    c: Coincident(g292,g293)
    c: Coincident(g293,g294)
    c: Coincident(g294,g295)
    c: Coincident(g295,g296)
    c: Coincident(g296,g283)
    c: Coincident(g297,g298)
    c: Coincident(g298,g299)
    c: Coincident(g299,g300)
    c: Coincident(g300,g301)
    c: Coincident(g301,g302)
    c: Coincident(g302,g303)
    c: Coincident(g303,g297)
    c: Coincident(g304,g305)
    c: Coincident(g305,g306)
    c: Coincident(g306,g307)
    c: Coincident(g307,g308)
    c: Coincident(g308,g309)
    c: Coincident(g309,g310)
    c: Coincident(g310,g311)
    c: Coincident(g311,g312)
    c: Coincident(g312,g313)
    c: Coincident(g313,g314)
    c: Coincident(g314,g315)
    c: Coincident(g315,g304)
    c: Coincident(g316,g317)
    c: Coincident(g317,g318)
    c: Coincident(g318,g319)
    c: Coincident(g319,g320)
    c: Coincident(g320,g321)
    c: Coincident(g321,g322)
    c: Coincident(g322,g323)
    c: Coincident(g323,g324)
    c: Coincident(g324,g325)
    c: Coincident(g325,g326)
    c: Coincident(g326,g316)
    c: Coincident(g327,g328)
    c: Coincident(g328,g329)
    c: Coincident(g329,g330)
    c: Coincident(g330,g331)
    c: Coincident(g331,g332)
    c: Coincident(g332,g333)
    c: Coincident(g333,g334)
    c: Coincident(g334,g335)
    c: Coincident(g335,g336)
    c: Coincident(g336,g327)
    c: Coincident(g337,g338)
    c: Coincident(g338,g339)
    c: Coincident(g339,g340)
    c: Coincident(g340,g341)
    c: Coincident(g341,g342)
    c: Coincident(g342,g337)
    c: Coincident(g343,g344)
    c: Coincident(g344,g345)
    c: Coincident(g345,g346)
    c: Coincident(g346,g347)
    c: Coincident(g347,g348)
    c: Coincident(g348,g343)
    c: Coincident(g349,g350)
    c: Coincident(g350,g351)
    c: Coincident(g351,g352)
    c: Coincident(g352,g353)
    c: Coincident(g353,g354)
    c: Coincident(g354,g355)
    c: Coincident(g355,g356)
    c: Coincident(g356,g357)
    c: Coincident(g357,g358)
    c: Coincident(g358,g359)
    c: Coincident(g359,g360)
    c: Coincident(g360,g361)
    c: Coincident(g361,g362)
    c: Coincident(g362,g363)
    c: Coincident(g363,g364)
    c: Coincident(g364,g365)
    c: Coincident(g365,g366)
    c: Coincident(g366,g367)
    c: Coincident(g367,g368)
    c: Coincident(g368,g349)
FEATURE [Sketcher::SketchObject] Sketch021  label="Sketch_MA"
  AttachmentOffset = pos=(0.5,-21,-84) rot=(0,0,1;-3.14159rad)
  FullyConstrained = false
  MapMode = 5
  Placement = pos=(-3.3,0.5,4.26e-14) rot=(0,0,1;4.71239rad)
  Support = -> [Pocket]
  sketch-geometry (775):
    g0: BSplineCurve PolesCount=4 KnotsCount=2 Degree=3 IsPeriodic=0
    g1: BSplineCurve PolesCount=4 KnotsCount=2 Degree=3 IsPeriodic=0
    g2: BSplineCurve PolesCount=2 KnotsCount=2 Degree=1 IsPeriodic=0
    g3: BSplineCurve PolesCount=4 KnotsCount=2 Degree=3 IsPeriodic=0
    g4: BSplineCurve PolesCount=2 KnotsCount=2 Degree=1 IsPeriodic=0
    g5: BSplineCurve PolesCount=2 KnotsCount=2 Degree=1 IsPeriodic=0
    g6: BSplineCurve PolesCount=2 KnotsCount=2 Degree=1 IsPeriodic=0
    g7: BSplineCurve PolesCount=4 KnotsCount=2 Degree=3 IsPeriodic=0
    g8: BSplineCurve PolesCount=2 KnotsCount=2 Degree=1 IsPeriodic=0
    g9: BSplineCurve PolesCount=4 KnotsCount=2 Degree=3 IsPeriodic=0
    g10: BSplineCurve PolesCount=4 KnotsCount=2 Degree=3 IsPeriodic=0
    g11: BSplineCurve PolesCount=4 KnotsCount=2 Degree=3 IsPeriodic=0
    g12: BSplineCurve PolesCount=4 KnotsCount=2 Degree=3 IsPeriodic=0
    g13: BSplineCurve PolesCount=4 KnotsCount=2 Degree=3 IsPeriodic=0
    g14: BSplineCurve PolesCount=4 KnotsCount=2 Degree=3 IsPeriodic=0
    g15: BSplineCurve PolesCount=4 KnotsCount=2 Degree=3 IsPeriodic=0
    g16: BSplineCurve PolesCount=4 KnotsCount=2 Degree=3 IsPeriodic=0
    g17: BSplineCurve PolesCount=4 KnotsCount=2 Degree=3 IsPeriodic=0
    g18: BSplineCurve PolesCount=4 KnotsCount=2 Degree=3 IsPeriodic=0
    g19: BSplineCurve PolesCount=4 KnotsCount=2 Degree=3 IsPeriodic=0
    g20: BSplineCurve PolesCount=4 KnotsCount=2 Degree=3 IsPeriodic=0
    g21: BSplineCurve PolesCount=4 KnotsCount=2 Degree=3 IsPeriodic=0
    g22: BSplineCurve PolesCount=4 KnotsCount=2 Degree=3 IsPeriodic=0
    g23: BSplineCurve PolesCount=4 KnotsCount=2 Degree=3 IsPeriodic=0
    g24: BSplineCurve PolesCount=2 KnotsCount=2 Degree=1 IsPeriodic=0
    g25: BSplineCurve PolesCount=2 KnotsCount=2 Degree=1 IsPeriodic=0
    g26: BSplineCurve PolesCount=2 KnotsCount=2 Degree=1 IsPeriodic=0
    g27: BSplineCurve PolesCount=2 KnotsCount=2 Degree=1 IsPeriodic=0
    g28: BSplineCurve PolesCount=2 KnotsCount=2 Degree=1 IsPeriodic=0
    g29: BSplineCurve PolesCount=2 KnotsCount=2 Degree=1 IsPeriodic=0
    g30: BSplineCurve PolesCount=2 KnotsCount=2 Degree=1 IsPeriodic=0
    g31: BSplineCurve PolesCount=2 KnotsCount=2 Degree=1 IsPeriodic=0
    g32: BSplineCurve PolesCount=2 KnotsCount=2 Degree=1 IsPeriodic=0
    g33: BSplineCurve PolesCount=2 KnotsCount=2 Degree=1 IsPeriodic=0
    g34: BSplineCurve PolesCount=2 KnotsCount=2 Degree=1 IsPeriodic=0
    g35: BSplineCurve PolesCount=2 KnotsCount=2 Degree=1 IsPeriodic=0
    g36: BSplineCurve PolesCount=2 KnotsCount=2 Degree=1 IsPeriodic=0
    g37: BSplineCurve PolesCount=2 KnotsCount=2 Degree=1 IsPeriodic=0
    g38: BSplineCurve PolesCount=2 KnotsCount=2 Degree=1 IsPeriodic=0
    g39: BSplineCurve PolesCount=2 KnotsCount=2 Degree=1 IsPeriodic=0
    g40: BSplineCurve PolesCount=2 KnotsCount=2 Degree=1 IsPeriodic=0
    g41: BSplineCurve PolesCount=2 KnotsCount=2 Degree=1 IsPeriodic=0
    g42: BSplineCurve PolesCount=2 KnotsCount=2 Degree=1 IsPeriodic=0
    g43: BSplineCurve PolesCount=2 KnotsCount=2 Degree=1 IsPeriodic=0
    g44: BSplineCurve PolesCount=2 KnotsCount=2 Degree=1 IsPeriodic=0
    g45: BSplineCurve PolesCount=2 KnotsCount=2 Degree=1 IsPeriodic=0
    g46: BSplineCurve PolesCount=2 KnotsCount=2 Degree=1 IsPeriodic=0
    g47: BSplineCurve PolesCount=2 KnotsCount=2 Degree=1 IsPeriodic=0
    g48: BSplineCurve PolesCount=2 KnotsCount=2 Degree=1 IsPeriodic=0
    g49: BSplineCurve PolesCount=2 KnotsCount=2 Degree=1 IsPeriodic=0
    g50: BSplineCurve PolesCount=2 KnotsCount=2 Degree=1 IsPeriodic=0
    g51: BSplineCurve PolesCount=2 KnotsCount=2 Degree=1 IsPeriodic=0
    g52: BSplineCurve PolesCount=2 KnotsCount=2 Degree=1 IsPeriodic=0
    g53: BSplineCurve PolesCount=2 KnotsCount=2 Degree=1 IsPeriodic=0
    g54: BSplineCurve PolesCount=2 KnotsCount=2 Degree=1 IsPeriodic=0
    g55: BSplineCurve PolesCount=2 KnotsCount=2 Degree=1 IsPeriodic=0
    g56: BSplineCurve PolesCount=2 KnotsCount=2 Degree=1 IsPeriodic=0
    g57: BSplineCurve PolesCount=2 KnotsCount=2 Degree=1 IsPeriodic=0
    g58: BSplineCurve PolesCount=2 KnotsCount=2 Degree=1 IsPeriodic=0
    g59: BSplineCurve PolesCount=2 KnotsCount=2 Degree=1 IsPeriodic=0
    g60: BSplineCurve PolesCount=2 KnotsCount=2 Degree=1 IsPeriodic=0
    g61: BSplineCurve PolesCount=4 KnotsCount=2 Degree=3 IsPeriodic=0
    g62: BSplineCurve PolesCount=2 KnotsCount=2 Degree=1 IsPeriodic=0
    g63: BSplineCurve PolesCount=2 KnotsCount=2 Degree=1 IsPeriodic=0
    g64: BSplineCurve PolesCount=2 KnotsCount=2 Degree=1 IsPeriodic=0
    g65: BSplineCurve PolesCount=4 KnotsCount=2 Degree=3 IsPeriodic=0
    g66: BSplineCurve PolesCount=2 KnotsCount=2 Degree=1 IsPeriodic=0
    g67: BSplineCurve PolesCount=2 KnotsCount=2 Degree=1 IsPeriodic=0
    g68: BSplineCurve PolesCount=4 KnotsCount=2 Degree=3 IsPeriodic=0
    g69: BSplineCurve PolesCount=4 KnotsCount=2 Degree=3 IsPeriodic=0
    g70: BSplineCurve PolesCount=2 KnotsCount=2 Degree=1 IsPeriodic=0
    g71: BSplineCurve PolesCount=2 KnotsCount=2 Degree=1 IsPeriodic=0
    g72: BSplineCurve PolesCount=2 KnotsCount=2 Degree=1 IsPeriodic=0
    g73: BSplineCurve PolesCount=2 KnotsCount=2 Degree=1 IsPeriodic=0
    g74: BSplineCurve PolesCount=2 KnotsCount=2 Degree=1 IsPeriodic=0
    g75: BSplineCurve PolesCount=2 KnotsCount=2 Degree=1 IsPeriodic=0
    g76: BSplineCurve PolesCount=2 KnotsCount=2 Degree=1 IsPeriodic=0
    g77: BSplineCurve PolesCount=2 KnotsCount=2 Degree=1 IsPeriodic=0
    g78: BSplineCurve PolesCount=2 KnotsCount=2 Degree=1 IsPeriodic=0
    g79: BSplineCurve PolesCount=2 KnotsCount=2 Degree=1 IsPeriodic=0
    g80: BSplineCurve PolesCount=4 KnotsCount=2 Degree=3 IsPeriodic=0
    g81: BSplineCurve PolesCount=4 KnotsCount=2 Degree=3 IsPeriodic=0
    g82: BSplineCurve PolesCount=4 KnotsCount=2 Degree=3 IsPeriodic=0
    g83: BSplineCurve PolesCount=4 KnotsCount=2 Degree=3 IsPeriodic=0
    g84: BSplineCurve PolesCount=4 KnotsCount=2 Degree=3 IsPeriodic=0
    g85: BSplineCurve PolesCount=4 KnotsCount=2 Degree=3 IsPeriodic=0
    g86: BSplineCurve PolesCount=2 KnotsCount=2 Degree=1 IsPeriodic=0
    g87: BSplineCurve PolesCount=4 KnotsCount=2 Degree=3 IsPeriodic=0
    g88: BSplineCurve PolesCount=4 KnotsCount=2 Degree=3 IsPeriodic=0
    g89: BSplineCurve PolesCount=4 KnotsCount=2 Degree=3 IsPeriodic=0
    g90: BSplineCurve PolesCount=4 KnotsCount=2 Degree=3 IsPeriodic=0
    g91: BSplineCurve PolesCount=4 KnotsCount=2 Degree=3 IsPeriodic=0
    g92: BSplineCurve PolesCount=4 KnotsCount=2 Degree=3 IsPeriodic=0
    g93: BSplineCurve PolesCount=2 KnotsCount=2 Degree=1 IsPeriodic=0
    g94: BSplineCurve PolesCount=2 KnotsCount=2 Degree=1 IsPeriodic=0
    g95: BSplineCurve PolesCount=2 KnotsCount=2 Degree=1 IsPeriodic=0
    g96: BSplineCurve PolesCount=2 KnotsCount=2 Degree=1 IsPeriodic=0
    g97: BSplineCurve PolesCount=2 KnotsCount=2 Degree=1 IsPeriodic=0
    g98: BSplineCurve PolesCount=2 KnotsCount=2 Degree=1 IsPeriodic=0
    g99: BSplineCurve PolesCount=2 KnotsCount=2 Degree=1 IsPeriodic=0
    g100: BSplineCurve PolesCount=2 KnotsCount=2 Degree=1 IsPeriodic=0
    g101: BSplineCurve PolesCount=2 KnotsCount=2 Degree=1 IsPeriodic=0
    g102: BSplineCurve PolesCount=2 KnotsCount=2 Degree=1 IsPeriodic=0
    g103: BSplineCurve PolesCount=2 KnotsCount=2 Degree=1 IsPeriodic=0
    g104: BSplineCurve PolesCount=2 KnotsCount=2 Degree=1 IsPeriodic=0
    g105: BSplineCurve PolesCount=2 KnotsCount=2 Degree=1 IsPeriodic=0
    g106: BSplineCurve PolesCount=4 KnotsCount=2 Degree=3 IsPeriodic=0
    g107: BSplineCurve PolesCount=4 KnotsCount=2 Degree=3 IsPeriodic=0
    g108: BSplineCurve PolesCount=4 KnotsCount=2 Degree=3 IsPeriodic=0
    g109: BSplineCurve PolesCount=4 KnotsCount=2 Degree=3 IsPeriodic=0
    g110: BSplineCurve PolesCount=4 KnotsCount=2 Degree=3 IsPeriodic=0
    g111: BSplineCurve PolesCount=4 KnotsCount=2 Degree=3 IsPeriodic=0
    g112: BSplineCurve PolesCount=2 KnotsCount=2 Degree=1 IsPeriodic=0
    g113: BSplineCurve PolesCount=4 KnotsCount=2 Degree=3 IsPeriodic=0
    g114: BSplineCurve PolesCount=4 KnotsCount=2 Degree=3 IsPeriodic=0
    g115: BSplineCurve PolesCount=4 KnotsCount=2 Degree=3 IsPeriodic=0
    g116: BSplineCurve PolesCount=4 KnotsCount=2 Degree=3 IsPeriodic=0
    g117: BSplineCurve PolesCount=4 KnotsCount=2 Degree=3 IsPeriodic=0
    g118: BSplineCurve PolesCount=4 KnotsCount=2 Degree=3 IsPeriodic=0
    g119: BSplineCurve PolesCount=2 KnotsCount=2 Degree=1 IsPeriodic=0
    g120: BSplineCurve PolesCount=2 KnotsCount=2 Degree=1 IsPeriodic=0
    g121: BSplineCurve PolesCount=2 KnotsCount=2 Degree=1 IsPeriodic=0
    g122: BSplineCurve PolesCount=2 KnotsCount=2 Degree=1 IsPeriodic=0
    g123: BSplineCurve PolesCount=2 KnotsCount=2 Degree=1 IsPeriodic=0
    g124: BSplineCurve PolesCount=2 KnotsCount=2 Degree=1 IsPeriodic=0
    g125: BSplineCurve PolesCount=2 KnotsCount=2 Degree=1 IsPeriodic=0
    g126: BSplineCurve PolesCount=2 KnotsCount=2 Degree=1 IsPeriodic=0
    g127: BSplineCurve PolesCount=2 KnotsCount=2 Degree=1 IsPeriodic=0
    g128: BSplineCurve PolesCount=2 KnotsCount=2 Degree=1 IsPeriodic=0
    g129: BSplineCurve PolesCount=2 KnotsCount=2 Degree=1 IsPeriodic=0
    g130: BSplineCurve PolesCount=2 KnotsCount=2 Degree=1 IsPeriodic=0
    g131: BSplineCurve PolesCount=2 KnotsCount=2 Degree=1 IsPeriodic=0
    g132: BSplineCurve PolesCount=2 KnotsCount=2 Degree=1 IsPeriodic=0
    g133: BSplineCurve PolesCount=2 KnotsCount=2 Degree=1 IsPeriodic=0
    g134: BSplineCurve PolesCount=2 KnotsCount=2 Degree=1 IsPeriodic=0
    g135: BSplineCurve PolesCount=2 KnotsCount=2 Degree=1 IsPeriodic=0
    g136: BSplineCurve PolesCount=2 KnotsCount=2 Degree=1 IsPeriodic=0
    g137: BSplineCurve PolesCount=4 KnotsCount=2 Degree=3 IsPeriodic=0
    g138: BSplineCurve PolesCount=4 KnotsCount=2 Degree=3 IsPeriodic=0
    g139: BSplineCurve PolesCount=2 KnotsCount=2 Degree=1 IsPeriodic=0
    g140: BSplineCurve PolesCount=2 KnotsCount=2 Degree=1 IsPeriodic=0
    g141: BSplineCurve PolesCount=2 KnotsCount=2 Degree=1 IsPeriodic=0
    g142: BSplineCurve PolesCount=4 KnotsCount=2 Degree=3 IsPeriodic=0
    g143: BSplineCurve PolesCount=4 KnotsCount=2 Degree=3 IsPeriodic=0
    g144: BSplineCurve PolesCount=2 KnotsCount=2 Degree=1 IsPeriodic=0
    g145: BSplineCurve PolesCount=2 KnotsCount=2 Degree=1 IsPeriodic=0
    g146: BSplineCurve PolesCount=2 KnotsCount=2 Degree=1 IsPeriodic=0
    g147: BSplineCurve PolesCount=2 KnotsCount=2 Degree=1 IsPeriodic=0
    g148: BSplineCurve PolesCount=2 KnotsCount=2 Degree=1 IsPeriodic=0
    g149: BSplineCurve PolesCount=2 KnotsCount=2 Degree=1 IsPeriodic=0
    g150: BSplineCurve PolesCount=2 KnotsCount=2 Degree=1 IsPeriodic=0
    g151: BSplineCurve PolesCount=2 KnotsCount=2 Degree=1 IsPeriodic=0
    g152: BSplineCurve PolesCount=2 KnotsCount=2 Degree=1 IsPeriodic=0
    g153: BSplineCurve PolesCount=2 KnotsCount=2 Degree=1 IsPeriodic=0
    g154: BSplineCurve PolesCount=2 KnotsCount=2 Degree=1 IsPeriodic=0
    g155: BSplineCurve PolesCount=2 KnotsCount=2 Degree=1 IsPeriodic=0
    g156: BSplineCurve PolesCount=2 KnotsCount=2 Degree=1 IsPeriodic=0
    g157: BSplineCurve PolesCount=2 KnotsCount=2 Degree=1 IsPeriodic=0
    g158: BSplineCurve PolesCount=2 KnotsCount=2 Degree=1 IsPeriodic=0
    g159: BSplineCurve PolesCount=2 KnotsCount=2 Degree=1 IsPeriodic=0
    g160: BSplineCurve PolesCount=2 KnotsCount=2 Degree=1 IsPeriodic=0
    g161: BSplineCurve PolesCount=2 KnotsCount=2 Degree=1 IsPeriodic=0
    g162: BSplineCurve PolesCount=2 KnotsCount=2 Degree=1 IsPeriodic=0
    g163: BSplineCurve PolesCount=2 KnotsCount=2 Degree=1 IsPeriodic=0
    g164: BSplineCurve PolesCount=2 KnotsCount=2 Degree=1 IsPeriodic=0
    g165: BSplineCurve PolesCount=2 KnotsCount=2 Degree=1 IsPeriodic=0
    g166: BSplineCurve PolesCount=2 KnotsCount=2 Degree=1 IsPeriodic=0
    g167: BSplineCurve PolesCount=2 KnotsCount=2 Degree=1 IsPeriodic=0
    g168: BSplineCurve PolesCount=2 KnotsCount=2 Degree=1 IsPeriodic=0
    g169: BSplineCurve PolesCount=2 KnotsCount=2 Degree=1 IsPeriodic=0
    g170: BSplineCurve PolesCount=2 KnotsCount=2 Degree=1 IsPeriodic=0
    g171: BSplineCurve PolesCount=2 KnotsCount=2 Degree=1 IsPeriodic=0
    g172: BSplineCurve PolesCount=2 KnotsCount=2 Degree=1 IsPeriodic=0
    g173: BSplineCurve PolesCount=2 KnotsCount=2 Degree=1 IsPeriodic=0
    g174: BSplineCurve PolesCount=2 KnotsCount=2 Degree=1 IsPeriodic=0
    g175: BSplineCurve PolesCount=2 KnotsCount=2 Degree=1 IsPeriodic=0
    g176: BSplineCurve PolesCount=2 KnotsCount=2 Degree=1 IsPeriodic=0
    g177: BSplineCurve PolesCount=2 KnotsCount=2 Degree=1 IsPeriodic=0
    g178: BSplineCurve PolesCount=2 KnotsCount=2 Degree=1 IsPeriodic=0
    g179: BSplineCurve PolesCount=2 KnotsCount=2 Degree=1 IsPeriodic=0
    g180: BSplineCurve PolesCount=2 KnotsCount=2 Degree=1 IsPeriodic=0
    g181: BSplineCurve PolesCount=2 KnotsCount=2 Degree=1 IsPeriodic=0
    g182: BSplineCurve PolesCount=2 KnotsCount=2 Degree=1 IsPeriodic=0
    g183: BSplineCurve PolesCount=4 KnotsCount=2 Degree=3 IsPeriodic=0
    g184: BSplineCurve PolesCount=4 KnotsCount=2 Degree=3 IsPeriodic=0
    g185: BSplineCurve PolesCount=2 KnotsCount=2 Degree=1 IsPeriodic=0
    g186: BSplineCurve PolesCount=2 KnotsCount=2 Degree=1 IsPeriodic=0
    g187: BSplineCurve PolesCount=4 KnotsCount=2 Degree=3 IsPeriodic=0
    g188: BSplineCurve PolesCount=2 KnotsCount=2 Degree=1 IsPeriodic=0
    g189: BSplineCurve PolesCount=4 KnotsCount=2 Degree=3 IsPeriodic=0
    g190: BSplineCurve PolesCount=4 KnotsCount=2 Degree=3 IsPeriodic=0
    g191: BSplineCurve PolesCount=4 KnotsCount=2 Degree=3 IsPeriodic=0
    g192: BSplineCurve PolesCount=4 KnotsCount=2 Degree=3 IsPeriodic=0
    g193: BSplineCurve PolesCount=4 KnotsCount=2 Degree=3 IsPeriodic=0
    g194: BSplineCurve PolesCount=2 KnotsCount=2 Degree=1 IsPeriodic=0
    g195: BSplineCurve PolesCount=4 KnotsCount=2 Degree=3 IsPeriodic=0
    g196: BSplineCurve PolesCount=4 KnotsCount=2 Degree=3 IsPeriodic=0
    g197: BSplineCurve PolesCount=4 KnotsCount=2 Degree=3 IsPeriodic=0
    g198: BSplineCurve PolesCount=4 KnotsCount=2 Degree=3 IsPeriodic=0
    g199: BSplineCurve PolesCount=2 KnotsCount=2 Degree=1 IsPeriodic=0
    g200: BSplineCurve PolesCount=4 KnotsCount=2 Degree=3 IsPeriodic=0
    g201: BSplineCurve PolesCount=4 KnotsCount=2 Degree=3 IsPeriodic=0
    g202: BSplineCurve PolesCount=4 KnotsCount=2 Degree=3 IsPeriodic=0
    g203: BSplineCurve PolesCount=4 KnotsCount=2 Degree=3 IsPeriodic=0
    g204: BSplineCurve PolesCount=2 KnotsCount=2 Degree=1 IsPeriodic=0
    g205: BSplineCurve PolesCount=4 KnotsCount=2 Degree=3 IsPeriodic=0
    g206: BSplineCurve PolesCount=4 KnotsCount=2 Degree=3 IsPeriodic=0
    g207: BSplineCurve PolesCount=4 KnotsCount=2 Degree=3 IsPeriodic=0
    g208: BSplineCurve PolesCount=4 KnotsCount=2 Degree=3 IsPeriodic=0
    g209: BSplineCurve PolesCount=2 KnotsCount=2 Degree=1 IsPeriodic=0
    g210: BSplineCurve PolesCount=4 KnotsCount=2 Degree=3 IsPeriodic=0
    g211: BSplineCurve PolesCount=4 KnotsCount=2 Degree=3 IsPeriodic=0
    g212: BSplineCurve PolesCount=4 KnotsCount=2 Degree=3 IsPeriodic=0
    g213: BSplineCurve PolesCount=4 KnotsCount=2 Degree=3 IsPeriodic=0
    g214: BSplineCurve PolesCount=2 KnotsCount=2 Degree=1 IsPeriodic=0
    g215: BSplineCurve PolesCount=4 KnotsCount=2 Degree=3 IsPeriodic=0
    g216: BSplineCurve PolesCount=4 KnotsCount=2 Degree=3 IsPeriodic=0
    g217: BSplineCurve PolesCount=4 KnotsCount=2 Degree=3 IsPeriodic=0
    g218: BSplineCurve PolesCount=4 KnotsCount=2 Degree=3 IsPeriodic=0
    g219: BSplineCurve PolesCount=2 KnotsCount=2 Degree=1 IsPeriodic=0
    g220: BSplineCurve PolesCount=4 KnotsCount=2 Degree=3 IsPeriodic=0
    g221: BSplineCurve PolesCount=4 KnotsCount=2 Degree=3 IsPeriodic=0
    g222: BSplineCurve PolesCount=4 KnotsCount=2 Degree=3 IsPeriodic=0
    g223: BSplineCurve PolesCount=4 KnotsCount=2 Degree=3 IsPeriodic=0
    g224: BSplineCurve PolesCount=2 KnotsCount=2 Degree=1 IsPeriodic=0
    g225: BSplineCurve PolesCount=4 KnotsCount=2 Degree=3 IsPeriodic=0
    g226: BSplineCurve PolesCount=2 KnotsCount=2 Degree=1 IsPeriodic=0
    g227: BSplineCurve PolesCount=4 KnotsCount=2 Degree=3 IsPeriodic=0
    g228: BSplineCurve PolesCount=2 KnotsCount=2 Degree=1 IsPeriodic=0
    g229: BSplineCurve PolesCount=4 KnotsCount=2 Degree=3 IsPeriodic=0
    g230: BSplineCurve PolesCount=2 KnotsCount=2 Degree=1 IsPeriodic=0
    g231: BSplineCurve PolesCount=2 KnotsCount=2 Degree=1 IsPeriodic=0
    g232: BSplineCurve PolesCount=4 KnotsCount=2 Degree=3 IsPeriodic=0
    g233: BSplineCurve PolesCount=4 KnotsCount=2 Degree=3 IsPeriodic=0
    g234: BSplineCurve PolesCount=4 KnotsCount=2 Degree=3 IsPeriodic=0
    g235: BSplineCurve PolesCount=4 KnotsCount=2 Degree=3 IsPeriodic=0
    g236: BSplineCurve PolesCount=2 KnotsCount=2 Degree=1 IsPeriodic=0
    g237: BSplineCurve PolesCount=4 KnotsCount=2 Degree=3 IsPeriodic=0
    g238: BSplineCurve PolesCount=4 KnotsCount=2 Degree=3 IsPeriodic=0
    g239: BSplineCurve PolesCount=4 KnotsCount=2 Degree=3 IsPeriodic=0
    g240: BSplineCurve PolesCount=4 KnotsCount=2 Degree=3 IsPeriodic=0
    g241: BSplineCurve PolesCount=2 KnotsCount=2 Degree=1 IsPeriodic=0
    g242: BSplineCurve PolesCount=4 KnotsCount=2 Degree=3 IsPeriodic=0
    g243: BSplineCurve PolesCount=4 KnotsCount=2 Degree=3 IsPeriodic=0
    g244: BSplineCurve PolesCount=4 KnotsCount=2 Degree=3 IsPeriodic=0
    g245: BSplineCurve PolesCount=4 KnotsCount=2 Degree=3 IsPeriodic=0
    g246: BSplineCurve PolesCount=2 KnotsCount=2 Degree=1 IsPeriodic=0
    g247: BSplineCurve PolesCount=4 KnotsCount=2 Degree=3 IsPeriodic=0
    g248: BSplineCurve PolesCount=4 KnotsCount=2 Degree=3 IsPeriodic=0
    g249: BSplineCurve PolesCount=4 KnotsCount=2 Degree=3 IsPeriodic=0
    g250: BSplineCurve PolesCount=4 KnotsCount=2 Degree=3 IsPeriodic=0
    g251: BSplineCurve PolesCount=2 KnotsCount=2 Degree=1 IsPeriodic=0
    g252: BSplineCurve PolesCount=4 KnotsCount=2 Degree=3 IsPeriodic=0
    g253: BSplineCurve PolesCount=4 KnotsCount=2 Degree=3 IsPeriodic=0
    g254: BSplineCurve PolesCount=4 KnotsCount=2 Degree=3 IsPeriodic=0
    g255: BSplineCurve PolesCount=4 KnotsCount=2 Degree=3 IsPeriodic=0
    g256: BSplineCurve PolesCount=2 KnotsCount=2 Degree=1 IsPeriodic=0
    g257: BSplineCurve PolesCount=4 KnotsCount=2 Degree=3 IsPeriodic=0
    g258: BSplineCurve PolesCount=2 KnotsCount=2 Degree=1 IsPeriodic=0
    g259: BSplineCurve PolesCount=4 KnotsCount=2 Degree=3 IsPeriodic=0
    g260: BSplineCurve PolesCount=4 KnotsCount=2 Degree=3 IsPeriodic=0
    g261: BSplineCurve PolesCount=2 KnotsCount=2 Degree=1 IsPeriodic=0
    g262: BSplineCurve PolesCount=4 KnotsCount=2 Degree=3 IsPeriodic=0
    g263: BSplineCurve PolesCount=4 KnotsCount=2 Degree=3 IsPeriodic=0
    g264: BSplineCurve PolesCount=4 KnotsCount=2 Degree=3 IsPeriodic=0
    g265: BSplineCurve PolesCount=2 KnotsCount=2 Degree=1 IsPeriodic=0
    g266: BSplineCurve PolesCount=2 KnotsCount=2 Degree=1 IsPeriodic=0
    g267: BSplineCurve PolesCount=2 KnotsCount=2 Degree=1 IsPeriodic=0
    g268: BSplineCurve PolesCount=4 KnotsCount=2 Degree=3 IsPeriodic=0
    g269: BSplineCurve PolesCount=2 KnotsCount=2 Degree=1 IsPeriodic=0
    g270: BSplineCurve PolesCount=4 KnotsCount=2 Degree=3 IsPeriodic=0
    g271: BSplineCurve PolesCount=4 KnotsCount=2 Degree=3 IsPeriodic=0
    g272: BSplineCurve PolesCount=4 KnotsCount=2 Degree=3 IsPeriodic=0
    g273: BSplineCurve PolesCount=4 KnotsCount=2 Degree=3 IsPeriodic=0
    g274: BSplineCurve PolesCount=2 KnotsCount=2 Degree=1 IsPeriodic=0
    g275: BSplineCurve PolesCount=2 KnotsCount=2 Degree=1 IsPeriodic=0
    g276: BSplineCurve PolesCount=4 KnotsCount=2 Degree=3 IsPeriodic=0
    g277: BSplineCurve PolesCount=2 KnotsCount=2 Degree=1 IsPeriodic=0
    g278: BSplineCurve PolesCount=4 KnotsCount=2 Degree=3 IsPeriodic=0
    g279: BSplineCurve PolesCount=2 KnotsCount=2 Degree=1 IsPeriodic=0
    g280: BSplineCurve PolesCount=2 KnotsCount=2 Degree=1 IsPeriodic=0
    g281: BSplineCurve PolesCount=4 KnotsCount=2 Degree=3 IsPeriodic=0
    g282: BSplineCurve PolesCount=4 KnotsCount=2 Degree=3 IsPeriodic=0
    g283: BSplineCurve PolesCount=4 KnotsCount=2 Degree=3 IsPeriodic=0
    g284: BSplineCurve PolesCount=4 KnotsCount=2 Degree=3 IsPeriodic=0
    g285: BSplineCurve PolesCount=2 KnotsCount=2 Degree=1 IsPeriodic=0
    g286: BSplineCurve PolesCount=4 KnotsCount=2 Degree=3 IsPeriodic=0
    g287: BSplineCurve PolesCount=2 KnotsCount=2 Degree=1 IsPeriodic=0
    g288: BSplineCurve PolesCount=4 KnotsCount=2 Degree=3 IsPeriodic=0
    g289: BSplineCurve PolesCount=4 KnotsCount=2 Degree=3 IsPeriodic=0
    g290: BSplineCurve PolesCount=2 KnotsCount=2 Degree=1 IsPeriodic=0
    g291: BSplineCurve PolesCount=4 KnotsCount=2 Degree=3 IsPeriodic=0
    g292: BSplineCurve PolesCount=4 KnotsCount=2 Degree=3 IsPeriodic=0
    g293: BSplineCurve PolesCount=4 KnotsCount=2 Degree=3 IsPeriodic=0
    g294: BSplineCurve PolesCount=2 KnotsCount=2 Degree=1 IsPeriodic=0
    g295: BSplineCurve PolesCount=2 KnotsCount=2 Degree=1 IsPeriodic=0
    g296: BSplineCurve PolesCount=2 KnotsCount=2 Degree=1 IsPeriodic=0
    g297: BSplineCurve PolesCount=4 KnotsCount=2 Degree=3 IsPeriodic=0
    g298: BSplineCurve PolesCount=2 KnotsCount=2 Degree=1 IsPeriodic=0
    g299: BSplineCurve PolesCount=4 KnotsCount=2 Degree=3 IsPeriodic=0
    g300: BSplineCurve PolesCount=4 KnotsCount=2 Degree=3 IsPeriodic=0
    g301: BSplineCurve PolesCount=4 KnotsCount=2 Degree=3 IsPeriodic=0
    g302: BSplineCurve PolesCount=4 KnotsCount=2 Degree=3 IsPeriodic=0
    g303: BSplineCurve PolesCount=4 KnotsCount=2 Degree=3 IsPeriodic=0
    g304: BSplineCurve PolesCount=2 KnotsCount=2 Degree=1 IsPeriodic=0
    g305: BSplineCurve PolesCount=4 KnotsCount=2 Degree=3 IsPeriodic=0
    g306: BSplineCurve PolesCount=4 KnotsCount=2 Degree=3 IsPeriodic=0
    g307: BSplineCurve PolesCount=4 KnotsCount=2 Degree=3 IsPeriodic=0
    g308: BSplineCurve PolesCount=4 KnotsCount=2 Degree=3 IsPeriodic=0
    g309: BSplineCurve PolesCount=2 KnotsCount=2 Degree=1 IsPeriodic=0
    g310: BSplineCurve PolesCount=4 KnotsCount=2 Degree=3 IsPeriodic=0
    g311: BSplineCurve PolesCount=4 KnotsCount=2 Degree=3 IsPeriodic=0
    g312: BSplineCurve PolesCount=4 KnotsCount=2 Degree=3 IsPeriodic=0
    g313: BSplineCurve PolesCount=4 KnotsCount=2 Degree=3 IsPeriodic=0
    g314: BSplineCurve PolesCount=2 KnotsCount=2 Degree=1 IsPeriodic=0
    g315: BSplineCurve PolesCount=4 KnotsCount=2 Degree=3 IsPeriodic=0
    g316: BSplineCurve PolesCount=4 KnotsCount=2 Degree=3 IsPeriodic=0
    g317: BSplineCurve PolesCount=2 KnotsCount=2 Degree=1 IsPeriodic=0
    g318: BSplineCurve PolesCount=4 KnotsCount=2 Degree=3 IsPeriodic=0
    g319: BSplineCurve PolesCount=2 KnotsCount=2 Degree=1 IsPeriodic=0
    g320: BSplineCurve PolesCount=4 KnotsCount=2 Degree=3 IsPeriodic=0
    g321: BSplineCurve PolesCount=2 KnotsCount=2 Degree=1 IsPeriodic=0
    g322: BSplineCurve PolesCount=4 KnotsCount=2 Degree=3 IsPeriodic=0
    g323: BSplineCurve PolesCount=2 KnotsCount=2 Degree=1 IsPeriodic=0
    g324: BSplineCurve PolesCount=4 KnotsCount=2 Degree=3 IsPeriodic=0
    g325: BSplineCurve PolesCount=2 KnotsCount=2 Degree=1 IsPeriodic=0
    g326: BSplineCurve PolesCount=2 KnotsCount=2 Degree=1 IsPeriodic=0
    g327: BSplineCurve PolesCount=2 KnotsCount=2 Degree=1 IsPeriodic=0
    g328: BSplineCurve PolesCount=2 KnotsCount=2 Degree=1 IsPeriodic=0
    g329: BSplineCurve PolesCount=2 KnotsCount=2 Degree=1 IsPeriodic=0
    g330: BSplineCurve PolesCount=2 KnotsCount=2 Degree=1 IsPeriodic=0
    g331: BSplineCurve PolesCount=2 KnotsCount=2 Degree=1 IsPeriodic=0
    g332: BSplineCurve PolesCount=2 KnotsCount=2 Degree=1 IsPeriodic=0
    g333: BSplineCurve PolesCount=2 KnotsCount=2 Degree=1 IsPeriodic=0
    g334: BSplineCurve PolesCount=2 KnotsCount=2 Degree=1 IsPeriodic=0
    g335: BSplineCurve PolesCount=2 KnotsCount=2 Degree=1 IsPeriodic=0
    g336: BSplineCurve PolesCount=2 KnotsCount=2 Degree=1 IsPeriodic=0
    g337: BSplineCurve PolesCount=2 KnotsCount=2 Degree=1 IsPeriodic=0
    g338: BSplineCurve PolesCount=2 KnotsCount=2 Degree=1 IsPeriodic=0
    g339: BSplineCurve PolesCount=2 KnotsCount=2 Degree=1 IsPeriodic=0
    g340: BSplineCurve PolesCount=2 KnotsCount=2 Degree=1 IsPeriodic=0
    g341: BSplineCurve PolesCount=2 KnotsCount=2 Degree=1 IsPeriodic=0
    g342: BSplineCurve PolesCount=2 KnotsCount=2 Degree=1 IsPeriodic=0
    g343: BSplineCurve PolesCount=2 KnotsCount=2 Degree=1 IsPeriodic=0
    g344: BSplineCurve PolesCount=2 KnotsCount=2 Degree=1 IsPeriodic=0
    g345: BSplineCurve PolesCount=2 KnotsCount=2 Degree=1 IsPeriodic=0
    g346: BSplineCurve PolesCount=2 KnotsCount=2 Degree=1 IsPeriodic=0
    g347: BSplineCurve PolesCount=2 KnotsCount=2 Degree=1 IsPeriodic=0
    g348: BSplineCurve PolesCount=2 KnotsCount=2 Degree=1 IsPeriodic=0
    g349: BSplineCurve PolesCount=2 KnotsCount=2 Degree=1 IsPeriodic=0
    g350: BSplineCurve PolesCount=2 KnotsCount=2 Degree=1 IsPeriodic=0
    g351: BSplineCurve PolesCount=2 KnotsCount=2 Degree=1 IsPeriodic=0
    g352: BSplineCurve PolesCount=2 KnotsCount=2 Degree=1 IsPeriodic=0
    g353: BSplineCurve PolesCount=2 KnotsCount=2 Degree=1 IsPeriodic=0
    g354: BSplineCurve PolesCount=2 KnotsCount=2 Degree=1 IsPeriodic=0
    g355: BSplineCurve PolesCount=2 KnotsCount=2 Degree=1 IsPeriodic=0
    g356: BSplineCurve PolesCount=2 KnotsCount=2 Degree=1 IsPeriodic=0
    g357: BSplineCurve PolesCount=2 KnotsCount=2 Degree=1 IsPeriodic=0
    g358: BSplineCurve PolesCount=2 KnotsCount=2 Degree=1 IsPeriodic=0
    g359: BSplineCurve PolesCount=2 KnotsCount=2 Degree=1 IsPeriodic=0
    g360: BSplineCurve PolesCount=2 KnotsCount=2 Degree=1 IsPeriodic=0
    g361: BSplineCurve PolesCount=2 KnotsCount=2 Degree=1 IsPeriodic=0
    g362: BSplineCurve PolesCount=2 KnotsCount=2 Degree=1 IsPeriodic=0
    g363: BSplineCurve PolesCount=2 KnotsCount=2 Degree=1 IsPeriodic=0
    g364: BSplineCurve PolesCount=2 KnotsCount=2 Degree=1 IsPeriodic=0
    g365: BSplineCurve PolesCount=2 KnotsCount=2 Degree=1 IsPeriodic=0
    g366: BSplineCurve PolesCount=2 KnotsCount=2 Degree=1 IsPeriodic=0
    g367: BSplineCurve PolesCount=2 KnotsCount=2 Degree=1 IsPeriodic=0
    g368: BSplineCurve PolesCount=2 KnotsCount=2 Degree=1 IsPeriodic=0
    g369: BSplineCurve PolesCount=2 KnotsCount=2 Degree=1 IsPeriodic=0
    g370: BSplineCurve PolesCount=2 KnotsCount=2 Degree=1 IsPeriodic=0
    g371: BSplineCurve PolesCount=2 KnotsCount=2 Degree=1 IsPeriodic=0
    g372: BSplineCurve PolesCount=2 KnotsCount=2 Degree=1 IsPeriodic=0
    g373: BSplineCurve PolesCount=2 KnotsCount=2 Degree=1 IsPeriodic=0
    g374: BSplineCurve PolesCount=2 KnotsCount=2 Degree=1 IsPeriodic=0
    g375: BSplineCurve PolesCount=2 KnotsCount=2 Degree=1 IsPeriodic=0
    g376: BSplineCurve PolesCount=2 KnotsCount=2 Degree=1 IsPeriodic=0
    g377: BSplineCurve PolesCount=2 KnotsCount=2 Degree=1 IsPeriodic=0
    g378: BSplineCurve PolesCount=2 KnotsCount=2 Degree=1 IsPeriodic=0
    g379: BSplineCurve PolesCount=2 KnotsCount=2 Degree=1 IsPeriodic=0
    g380: BSplineCurve PolesCount=2 KnotsCount=2 Degree=1 IsPeriodic=0
    g381: BSplineCurve PolesCount=2 KnotsCount=2 Degree=1 IsPeriodic=0
    g382: BSplineCurve PolesCount=2 KnotsCount=2 Degree=1 IsPeriodic=0
    g383: BSplineCurve PolesCount=2 KnotsCount=2 Degree=1 IsPeriodic=0
    g384: BSplineCurve PolesCount=2 KnotsCount=2 Degree=1 IsPeriodic=0
    g385: BSplineCurve PolesCount=2 KnotsCount=2 Degree=1 IsPeriodic=0
    g386: BSplineCurve PolesCount=2 KnotsCount=2 Degree=1 IsPeriodic=0
    g387: BSplineCurve PolesCount=4 KnotsCount=2 Degree=3 IsPeriodic=0
    g388: BSplineCurve PolesCount=4 KnotsCount=2 Degree=3 IsPeriodic=0
    g389: BSplineCurve PolesCount=2 KnotsCount=2 Degree=1 IsPeriodic=0
    g390: BSplineCurve PolesCount=2 KnotsCount=2 Degree=1 IsPeriodic=0
    g391: BSplineCurve PolesCount=2 KnotsCount=2 Degree=1 IsPeriodic=0
    g392: BSplineCurve PolesCount=2 KnotsCount=2 Degree=1 IsPeriodic=0
    g393: BSplineCurve PolesCount=4 KnotsCount=2 Degree=3 IsPeriodic=0
    g394: BSplineCurve PolesCount=2 KnotsCount=2 Degree=1 IsPeriodic=0
    g395: BSplineCurve PolesCount=2 KnotsCount=2 Degree=1 IsPeriodic=0
    g396: BSplineCurve PolesCount=2 KnotsCount=2 Degree=1 IsPeriodic=0
    g397: BSplineCurve PolesCount=2 KnotsCount=2 Degree=1 IsPeriodic=0
    g398: BSplineCurve PolesCount=2 KnotsCount=2 Degree=1 IsPeriodic=0
    g399: BSplineCurve PolesCount=2 KnotsCount=2 Degree=1 IsPeriodic=0
    ... +375 more geometry lines
  constraints (775):
    c: Coincident(g0,g1)
    c: Coincident(g1,g2)
    c: Coincident(g2,g3)
    c: Coincident(g3,g4)
    c: Coincident(g4,g5)
    c: Coincident(g5,g6)
    c: Coincident(g6,g7)
    c: Coincident(g7,g8)
    c: Coincident(g8,g9)
    c: Coincident(g9,g10)
    c: Coincident(g10,g11)
    c: Coincident(g11,g12)
    c: Coincident(g12,g13)
    c: Coincident(g13,g14)
    c: Coincident(g14,g15)
    c: Coincident(g15,g16)
    c: Coincident(g16,g17)
    c: Coincident(g17,g18)
    c: Coincident(g18,g19)
    c: Coincident(g19,g20)
    c: Coincident(g20,g21)
    c: Coincident(g21,g22)
    c: Coincident(g22,g23)
    c: Coincident(g23,g0)
    c: Coincident(g24,g25)
    c: Coincident(g25,g26)
    c: Coincident(g26,g27)
    c: Coincident(g27,g24)
    c: Coincident(g28,g29)
    c: Coincident(g29,g30)
    c: Coincident(g30,g31)
    c: Coincident(g31,g32)
    c: Coincident(g32,g33)
    c: Coincident(g33,g34)
    c: Coincident(g34,g35)
    c: Coincident(g35,g28)
    c: Coincident(g36,g37)
    c: Coincident(g37,g38)
    c: Coincident(g38,g39)
    c: Coincident(g39,g40)
    c: Coincident(g40,g41)
    c: Coincident(g41,g42)
    c: Coincident(g42,g43)
    c: Coincident(g43,g44)
    c: Coincident(g44,g45)
    c: Coincident(g45,g46)
    c: Coincident(g46,g47)
    c: Coincident(g47,g48)
    c: Coincident(g48,g36)
    c: Coincident(g49,g50)
    c: Coincident(g50,g51)
    c: Coincident(g51,g52)
    c: Coincident(g52,g53)
    c: Coincident(g53,g54)
    c: Coincident(g54,g55)
    c: Coincident(g55,g56)
    c: Coincident(g56,g57)
    c: Coincident(g57,g58)
    c: Coincident(g58,g59)
    c: Coincident(g59,g60)
    c: Coincident(g60,g49)
    c: Coincident(g61,g62)
    c: Coincident(g62,g63)
    c: Coincident(g63,g64)
    c: Coincident(g64,g65)
    c: Coincident(g65,g61)
    c: Coincident(g66,g67)
    c: Coincident(g67,g68)
    c: Coincident(g68,g69)
    c: Coincident(g69,g70)
    c: Coincident(g70,g71)
    c: Coincident(g71,g72)
    c: Coincident(g72,g73)
    c: Coincident(g73,g74)
    c: Coincident(g74,g75)
    c: Coincident(g75,g66)
    c: Coincident(g76,g77)
    c: Coincident(g77,g78)
    c: Coincident(g78,g79)
    c: Coincident(g79,g76)
    c: Coincident(g80,g81)
    c: Coincident(g81,g82)
    c: Coincident(g82,g83)
    c: Coincident(g83,g84)
    c: Coincident(g84,g85)
    c: Coincident(g85,g86)
    c: Coincident(g86,g87)
    c: Coincident(g87,g88)
    c: Coincident(g88,g89)
    c: Coincident(g89,g90)
    c: Coincident(g90,g91)
    c: Coincident(g91,g92)
    c: Coincident(g92,g93)
    c: Coincident(g93,g80)
    c: Coincident(g94,g95)
    c: Coincident(g95,g96)
    c: Coincident(g96,g97)
    c: Coincident(g97,g94)
    c: Coincident(g98,g99)
    c: Coincident(g99,g100)
    c: Coincident(g100,g101)
    c: Coincident(g101,g102)
    c: Coincident(g102,g103)
    c: Coincident(g103,g104)
    c: Coincident(g104,g105)
    c: Coincident(g105,g98)
    c: Coincident(g106,g107)
    c: Coincident(g107,g108)
    c: Coincident(g108,g109)
    c: Coincident(g109,g110)
    c: Coincident(g110,g111)
    c: Coincident(g111,g112)
    c: Coincident(g112,g113)
    c: Coincident(g113,g114)
    c: Coincident(g114,g115)
    c: Coincident(g115,g116)
    c: Coincident(g116,g117)
    c: Coincident(g117,g118)
    c: Coincident(g118,g119)
    c: Coincident(g119,g106)
    c: Coincident(g120,g121)
    c: Coincident(g121,g122)
    c: Coincident(g122,g123)
    c: Coincident(g123,g124)
    c: Coincident(g124,g125)
    c: Coincident(g125,g126)
    c: Coincident(g126,g127)
    c: Coincident(g127,g128)
    c: Coincident(g128,g120)
    c: Coincident(g129,g130)
    c: Coincident(g130,g131)
    c: Coincident(g131,g132)
    c: Coincident(g132,g133)
    c: Coincident(g133,g134)
    c: Coincident(g134,g129)
    c: Coincident(g135,g136)
    c: Coincident(g136,g137)
    c: Coincident(g137,g138)
    c: Coincident(g138,g139)
    c: Coincident(g139,g140)
    c: Coincident(g140,g141)
    c: Coincident(g141,g142)
    c: Coincident(g142,g143)
    c: Coincident(g143,g144)
    c: Coincident(g144,g145)
    c: Coincident(g145,g135)
    c: Coincident(g146,g147)
    c: Coincident(g147,g148)
    c: Coincident(g148,g149)
    c: Coincident(g149,g150)
    c: Coincident(g150,g151)
    c: Coincident(g151,g152)
    c: Coincident(g152,g153)
    c: Coincident(g153,g154)
    c: Coincident(g154,g155)
    c: Coincident(g155,g156)
    c: Coincident(g156,g157)
    c: Coincident(g157,g158)
    c: Coincident(g158,g159)
    c: Coincident(g159,g160)
    c: Coincident(g160,g146)
    c: Coincident(g161,g162)
    c: Coincident(g162,g163)
    c: Coincident(g163,g164)
    c: Coincident(g164,g165)
    c: Coincident(g165,g166)
    c: Coincident(g166,g167)
    c: Coincident(g167,g168)
    c: Coincident(g168,g169)
    c: Coincident(g169,g170)
    c: Coincident(g170,g171)
    c: Coincident(g171,g172)
    c: Coincident(g172,g173)
    c: Coincident(g173,g161)
    c: Coincident(g174,g175)
    c: Coincident(g175,g176)
    c: Coincident(g176,g177)
    c: Coincident(g177,g178)
    c: Coincident(g178,g179)
    c: Coincident(g179,g180)
    c: Coincident(g180,g181)
    c: Coincident(g181,g174)
    c: Coincident(g182,g183)
    c: Coincident(g183,g184)
    c: Coincident(g184,g185)
    c: Coincident(g185,g186)
    c: Coincident(g186,g187)
    c: Coincident(g187,g188)
    c: Coincident(g188,g189)
    c: Coincident(g189,g190)
    c: Coincident(g190,g191)
    c: Coincident(g191,g192)
    c: Coincident(g192,g193)
    c: Coincident(g193,g194)
    c: Coincident(g194,g195)
    c: Coincident(g195,g196)
    c: Coincident(g196,g197)
    c: Coincident(g197,g198)
    c: Coincident(g198,g199)
    c: Coincident(g199,g200)
    c: Coincident(g200,g201)
    c: Coincident(g201,g202)
    c: Coincident(g202,g203)
    c: Coincident(g203,g204)
    c: Coincident(g204,g205)
    c: Coincident(g205,g206)
    c: Coincident(g206,g207)
    c: Coincident(g207,g208)
    c: Coincident(g208,g209)
    c: Coincident(g209,g210)
    c: Coincident(g210,g211)
    c: Coincident(g211,g212)
    c: Coincident(g212,g213)
    c: Coincident(g213,g214)
    c: Coincident(g214,g215)
    c: Coincident(g215,g216)
    c: Coincident(g216,g217)
    c: Coincident(g217,g218)
    c: Coincident(g218,g219)
    c: Coincident(g219,g220)
    c: Coincident(g220,g221)
    c: Coincident(g221,g222)
    c: Coincident(g222,g223)
    c: Coincident(g223,g224)
    c: Coincident(g224,g225)
    c: Coincident(g225,g226)
    c: Coincident(g226,g227)
    c: Coincident(g227,g228)
    c: Coincident(g228,g229)
    c: Coincident(g229,g230)
    c: Coincident(g230,g231)
    c: Coincident(g231,g232)
    c: Coincident(g232,g233)
    c: Coincident(g233,g234)
    c: Coincident(g234,g235)
    c: Coincident(g235,g236)
    c: Coincident(g236,g237)
    c: Coincident(g237,g238)
    c: Coincident(g238,g239)
    c: Coincident(g239,g240)
    c: Coincident(g240,g241)
    c: Coincident(g241,g242)
    c: Coincident(g242,g243)
    c: Coincident(g243,g244)
    c: Coincident(g244,g245)
    c: Coincident(g245,g246)
    c: Coincident(g246,g247)
    c: Coincident(g247,g248)
    c: Coincident(g248,g249)
    c: Coincident(g249,g250)
    c: Coincident(g250,g251)
    c: Coincident(g251,g252)
    c: Coincident(g252,g253)
    c: Coincident(g253,g254)
    c: Coincident(g254,g255)
    c: Coincident(g255,g256)
    c: Coincident(g256,g257)
    c: Coincident(g257,g258)
    c: Coincident(g258,g259)
    c: Coincident(g259,g260)
    c: Coincident(g260,g261)
    c: Coincident(g261,g262)
    c: Coincident(g262,g263)
    c: Coincident(g263,g264)
    c: Coincident(g264,g265)
    c: Coincident(g265,g266)
    c: Coincident(g266,g267)
    c: Coincident(g267,g268)
    c: Coincident(g268,g269)
    c: Coincident(g269,g270)
    c: Coincident(g270,g271)
    c: Coincident(g271,g272)
    c: Coincident(g272,g273)
    c: Coincident(g273,g274)
    c: Coincident(g274,g275)
    c: Coincident(g275,g276)
    c: Coincident(g276,g277)
    c: Coincident(g277,g278)
    c: Coincident(g278,g279)
    c: Coincident(g279,g280)
    c: Coincident(g280,g281)
    c: Coincident(g281,g282)
    c: Coincident(g282,g283)
    c: Coincident(g283,g284)
    c: Coincident(g284,g285)
    c: Coincident(g285,g286)
    c: Coincident(g286,g287)
    c: Coincident(g287,g288)
    c: Coincident(g288,g289)
    c: Coincident(g289,g290)
    c: Coincident(g290,g291)
    c: Coincident(g291,g292)
    c: Coincident(g292,g293)
    c: Coincident(g293,g294)
    c: Coincident(g294,g295)
    c: Coincident(g295,g296)
    c: Coincident(g296,g297)
    c: Coincident(g297,g298)
    c: Coincident(g298,g299)
    c: Coincident(g299,g300)
    c: Coincident(g300,g301)
    c: Coincident(g301,g302)
    c: Coincident(g302,g303)
    c: Coincident(g303,g304)
    c: Coincident(g304,g305)
    c: Coincident(g305,g306)
    c: Coincident(g306,g307)
    c: Coincident(g307,g308)
    c: Coincident(g308,g309)
    c: Coincident(g309,g310)
    c: Coincident(g310,g311)
    c: Coincident(g311,g312)
    c: Coincident(g312,g313)
    c: Coincident(g313,g314)
    c: Coincident(g314,g315)
    c: Coincident(g315,g316)
    c: Coincident(g316,g317)
    c: Coincident(g317,g318)
    c: Coincident(g318,g182)
    c: Coincident(g319,g320)
    c: Coincident(g320,g321)
    c: Coincident(g321,g322)
    c: Coincident(g322,g323)
    c: Coincident(g323,g324)
    c: Coincident(g324,g319)
    c: Coincident(g325,g326)
    c: Coincident(g326,g327)
    c: Coincident(g327,g328)
    c: Coincident(g328,g329)
    c: Coincident(g329,g330)
    c: Coincident(g330,g331)
    c: Coincident(g331,g332)
    c: Coincident(g332,g333)
    c: Coincident(g333,g334)
    c: Coincident(g334,g335)
    c: Coincident(g335,g336)
    c: Coincident(g336,g337)
    c: Coincident(g337,g338)
    c: Coincident(g338,g339)
    c: Coincident(g339,g340)
    c: Coincident(g340,g341)
    c: Coincident(g341,g342)
    c: Coincident(g342,g343)
    c: Coincident(g343,g344)
    c: Coincident(g344,g345)
    c: Coincident(g345,g346)
    c: Coincident(g346,g347)
    c: Coincident(g347,g348)
    c: Coincident(g348,g349)
    c: Coincident(g349,g350)
    c: Coincident(g350,g351)
    c: Coincident(g351,g352)
    c: Coincident(g352,g353)
    c: Coincident(g353,g354)
    c: Coincident(g354,g355)
    c: Coincident(g355,g356)
    c: Coincident(g356,g357)
    c: Coincident(g357,g358)
    c: Coincident(g358,g359)
    c: Coincident(g359,g360)
    c: Coincident(g360,g361)
    c: Coincident(g361,g362)
    c: Coincident(g362,g363)
    c: Coincident(g363,g364)
    c: Coincident(g364,g365)
    c: Coincident(g365,g366)
    c: Coincident(g366,g367)
    c: Coincident(g367,g368)
    c: Coincident(g368,g369)
    c: Coincident(g369,g370)
    c: Coincident(g370,g371)
    c: Coincident(g371,g372)
    c: Coincident(g372,g373)
    c: Coincident(g373,g374)
    c: Coincident(g374,g375)
    c: Coincident(g375,g376)
    c: Coincident(g376,g377)
    c: Coincident(g377,g378)
    c: Coincident(g378,g379)
    c: Coincident(g379,g380)
    c: Coincident(g380,g381)
    c: Coincident(g381,g382)
    c: Coincident(g382,g383)
    c: Coincident(g383,g384)
    c: Coincident(g384,g385)
    c: Coincident(g385,g386)
    c: Coincident(g386,g387)
    c: Coincident(g387,g388)
    c: Coincident(g388,g325)
    c: Coincident(g389,g390)
    c: Coincident(g390,g391)
    c: Coincident(g391,g392)
    c: Coincident(g392,g393)
    c: Coincident(g393,g394)
    c: Coincident(g394,g395)
    c: Coincident(g395,g396)
    c: Coincident(g396,g397)
    c: Coincident(g397,g398)
    c: Coincident(g398,g399)
    c: Coincident(g399,g400)
    c: Coincident(g400,g401)
    c: Coincident(g401,g402)
    c: Coincident(g402,g403)
    c: Coincident(g403,g404)
    c: Coincident(g404,g405)
    c: Coincident(g405,g406)
    c: Coincident(g406,g407)
    c: Coincident(g407,g408)
    c: Coincident(g408,g409)
    c: Coincident(g409,g410)
    c: Coincident(g410,g411)
    c: Coincident(g411,g412)
    c: Coincident(g412,g413)
    c: Coincident(g413,g414)
    c: Coincident(g414,g415)
    c: Coincident(g415,g416)
    c: Coincident(g416,g417)
    c: Coincident(g417,g418)
    c: Coincident(g418,g419)
    c: Coincident(g419,g420)
    c: Coincident(g420,g421)
    c: Coincident(g421,g422)
    c: Coincident(g422,g423)
    c: Coincident(g423,g424)
    c: Coincident(g424,g425)
    c: Coincident(g425,g426)
    c: Coincident(g426,g427)
    c: Coincident(g427,g428)
    c: Coincident(g428,g429)
    c: Coincident(g429,g430)
    c: Coincident(g430,g431)
    c: Coincident(g431,g432)
    c: Coincident(g432,g433)
    c: Coincident(g433,g434)
    c: Coincident(g434,g435)
    c: Coincident(g435,g436)
    c: Coincident(g436,g437)
    c: Coincident(g437,g438)
    c: Coincident(g438,g439)
    c: Coincident(g439,g440)
    c: Coincident(g440,g441)
    c: Coincident(g441,g442)
    c: Coincident(g442,g443)
    c: Coincident(g443,g444)
    c: Coincident(g444,g389)
    c: Coincident(g445,g446)
    c: Coincident(g446,g447)
    c: Coincident(g447,g448)
    c: Coincident(g448,g449)
    c: Coincident(g449,g450)
    c: Coincident(g450,g451)
    c: Coincident(g451,g452)
    c: Coincident(g452,g453)
    c: Coincident(g453,g454)
    c: Coincident(g454,g455)
    c: Coincident(g455,g456)
    c: Coincident(g456,g457)
    c: Coincident(g457,g458)
    c: Coincident(g458,g459)
    c: Coincident(g459,g460)
    c: Coincident(g460,g461)
    c: Coincident(g461,g462)
    c: Coincident(g462,g463)
    c: Coincident(g463,g464)
    c: Coincident(g464,g465)
    c: Coincident(g465,g466)
    c: Coincident(g466,g467)
    c: Coincident(g467,g468)
    c: Coincident(g468,g469)
    c: Coincident(g469,g470)
    c: Coincident(g470,g471)
    c: Coincident(g471,g472)
    c: Coincident(g472,g473)
    c: Coincident(g473,g474)
    c: Coincident(g474,g475)
    c: Coincident(g475,g476)
    c: Coincident(g476,g477)
    c: Coincident(g477,g478)
    c: Coincident(g478,g479)
    c: Coincident(g479,g480)
    c: Coincident(g480,g481)
    c: Coincident(g481,g482)
    c: Coincident(g482,g483)
    c: Coincident(g483,g484)
    c: Coincident(g484,g485)
    c: Coincident(g485,g486)
    c: Coincident(g486,g487)
    c: Coincident(g487,g488)
    c: Coincident(g488,g445)
    c: Coincident(g489,g490)
    c: Coincident(g490,g491)
    c: Coincident(g491,g492)
    c: Coincident(g492,g493)
    c: Coincident(g493,g494)
    c: Coincident(g494,g495)
    c: Coincident(g495,g496)
    c: Coincident(g496,g489)
    c: Coincident(g497,g498)
    c: Coincident(g498,g499)
    c: Coincident(g499,g500)
    c: Coincident(g500,g501)
    c: Coincident(g501,g502)
    c: Coincident(g502,g503)
    c: Coincident(g503,g504)
    c: Coincident(g504,g505)
    c: Coincident(g505,g506)
    c: Coincident(g506,g507)
    c: Coincident(g507,g508)
    c: Coincident(g508,g509)
    c: Coincident(g509,g510)
    c: Coincident(g510,g511)
    c: Coincident(g511,g512)
    c: Coincident(g512,g513)
    c: Coincident(g513,g514)
    c: Coincident(g514,g515)
    c: Coincident(g515,g516)
    c: Coincident(g516,g517)
    c: Coincident(g517,g497)
    c: Coincident(g518,g519)
    c: Coincident(g519,g520)
    c: Coincident(g520,g521)
    c: Coincident(g521,g522)
    c: Coincident(g522,g523)
    c: Coincident(g523,g524)
    c: Coincident(g524,g525)
    c: Coincident(g525,g526)
    c: Coincident(g526,g527)
    c: Coincident(g527,g528)
    c: Coincident(g528,g529)
    c: Coincident(g529,g530)
    c: Coincident(g530,g518)
    c: Coincident(g531,g532)
    c: Coincident(g532,g533)
    c: Coincident(g533,g534)
    c: Coincident(g534,g535)
    c: Coincident(g535,g536)
    c: Coincident(g536,g537)
    c: Coincident(g537,g538)
    c: Coincident(g538,g539)
    c: Coincident(g539,g540)
    c: Coincident(g540,g541)
    c: Coincident(g541,g542)
    c: Coincident(g542,g543)
    c: Coincident(g543,g544)
    c: Coincident(g544,g545)
    c: Coincident(g545,g546)
    c: Coincident(g546,g547)
    c: Coincident(g547,g548)
    c: Coincident(g548,g549)
    c: Coincident(g549,g550)
    c: Coincident(g550,g551)
    c: Coincident(g551,g552)
    c: Coincident(g552,g553)
    c: Coincident(g553,g554)
    c: Coincident(g554,g555)
    c: Coincident(g555,g556)
    c: Coincident(g556,g557)
    c: Coincident(g557,g558)
    c: Coincident(g558,g559)
    c: Coincident(g559,g560)
    c: Coincident(g560,g561)
    c: Coincident(g561,g562)
    c: Coincident(g562,g563)
    c: Coincident(g563,g564)
    c: Coincident(g564,g565)
    c: Coincident(g565,g566)
    c: Coincident(g566,g567)
    c: Coincident(g567,g568)
    c: Coincident(g568,g569)
    c: Coincident(g569,g570)
    c: Coincident(g570,g571)
    c: Coincident(g571,g572)
    c: Coincident(g572,g573)
    c: Coincident(g573,g574)
    c: Coincident(g574,g575)
    c: Coincident(g575,g576)
    c: Coincident(g576,g577)
    c: Coincident(g577,g578)
    c: Coincident(g578,g579)
    c: Coincident(g579,g580)
    c: Coincident(g580,g581)
    c: Coincident(g581,g582)
    c: Coincident(g582,g583)
    c: Coincident(g583,g584)
    c: Coincident(g584,g585)
    c: Coincident(g585,g586)
    c: Coincident(g586,g587)
    c: Coincident(g587,g588)
    c: Coincident(g588,g589)
    c: Coincident(g589,g590)
    c: Coincident(g590,g591)
    c: Coincident(g591,g592)
    c: Coincident(g592,g593)
    c: Coincident(g593,g594)
    c: Coincident(g594,g595)
    c: Coincident(g595,g596)
    c: Coincident(g596,g597)
    c: Coincident(g597,g598)
    c: Coincident(g598,g599)
    c: Coincident(g599,g600)
    c: Coincident(g600,g601)
    c: Coincident(g601,g602)
    c: Coincident(g602,g603)
    c: Coincident(g603,g604)
    c: Coincident(g604,g605)
    c: Coincident(g605,g606)
    c: Coincident(g606,g607)
    c: Coincident(g607,g608)
    c: Coincident(g608,g609)
    c: Coincident(g609,g610)
    c: Coincident(g610,g611)
    c: Coincident(g611,g612)
    c: Coincident(g612,g613)
    c: Coincident(g613,g614)
    c: Coincident(g614,g615)
    c: Coincident(g615,g616)
    c: Coincident(g616,g617)
    c: Coincident(g617,g618)
    c: Coincident(g618,g619)
    c: Coincident(g619,g620)
    c: Coincident(g620,g621)
    c: Coincident(g621,g622)
    c: Coincident(g622,g623)
    c: Coincident(g623,g624)
    c: Coincident(g624,g625)
    c: Coincident(g625,g626)
    c: Coincident(g626,g627)
    c: Coincident(g627,g628)
    c: Coincident(g628,g629)
    c: Coincident(g629,g630)
    c: Coincident(g630,g631)
    c: Coincident(g631,g632)
    c: Coincident(g632,g633)
    c: Coincident(g633,g634)
    c: Coincident(g634,g635)
    c: Coincident(g635,g636)
    c: Coincident(g636,g637)
    c: Coincident(g637,g638)
    c: Coincident(g638,g639)
    c: Coincident(g639,g640)
    c: Coincident(g640,g641)
    c: Coincident(g641,g642)
    c: Coincident(g642,g643)
    c: Coincident(g643,g644)
    c: Coincident(g644,g645)
    c: Coincident(g645,g646)
    c: Coincident(g646,g647)
    c: Coincident(g647,g648)
    c: Coincident(g648,g649)
    c: Coincident(g649,g650)
    c: Coincident(g650,g651)
    c: Coincident(g651,g652)
    c: Coincident(g652,g653)
    c: Coincident(g653,g654)
    c: Coincident(g654,g655)
    c: Coincident(g655,g656)
    c: Coincident(g656,g657)
    c: Coincident(g657,g658)
    c: Coincident(g658,g659)
    c: Coincident(g659,g660)
    c: Coincident(g660,g661)
    c: Coincident(g661,g662)
    c: Coincident(g662,g663)
    c: Coincident(g663,g664)
    c: Coincident(g664,g665)
    c: Coincident(g665,g666)
    c: Coincident(g666,g667)
    c: Coincident(g667,g668)
    c: Coincident(g668,g669)
    c: Coincident(g669,g670)
    c: Coincident(g670,g671)
    c: Coincident(g671,g672)
    c: Coincident(g672,g673)
    c: Coincident(g673,g674)
    c: Coincident(g674,g675)
    c: Coincident(g675,g676)
    c: Coincident(g676,g677)
    c: Coincident(g677,g678)
    c: Coincident(g678,g679)
    c: Coincident(g679,g680)
    c: Coincident(g680,g681)
    c: Coincident(g681,g682)
    c: Coincident(g682,g683)
    c: Coincident(g683,g684)
    c: Coincident(g684,g685)
    c: Coincident(g685,g686)
    c: Coincident(g686,g687)
    c: Coincident(g687,g688)
    c: Coincident(g688,g689)
    c: Coincident(g689,g690)
    c: Coincident(g690,g691)
    c: Coincident(g691,g692)
    c: Coincident(g692,g693)
    c: Coincident(g693,g694)
    c: Coincident(g694,g695)
    c: Coincident(g695,g696)
    c: Coincident(g696,g697)
    c: Coincident(g697,g698)
    c: Coincident(g698,g699)
    c: Coincident(g699,g700)
    c: Coincident(g700,g701)
    c: Coincident(g701,g702)
    c: Coincident(g702,g703)
    c: Coincident(g703,g704)
    c: Coincident(g704,g705)
    c: Coincident(g705,g706)
    c: Coincident(g706,g707)
    c: Coincident(g707,g708)
    c: Coincident(g708,g709)
    c: Coincident(g709,g710)
    c: Coincident(g710,g711)
    c: Coincident(g711,g712)
    c: Coincident(g712,g713)
    c: Coincident(g713,g714)
    c: Coincident(g714,g715)
    c: Coincident(g715,g716)
    c: Coincident(g716,g717)
    c: Coincident(g717,g718)
    c: Coincident(g718,g719)
    c: Coincident(g719,g720)
    c: Coincident(g720,g721)
    c: Coincident(g721,g722)
    c: Coincident(g722,g723)
    c: Coincident(g723,g724)
    c: Coincident(g724,g725)
    c: Coincident(g725,g726)
    c: Coincident(g726,g727)
    c: Coincident(g727,g728)
    c: Coincident(g728,g729)
    c: Coincident(g729,g730)
    c: Coincident(g730,g731)
    c: Coincident(g731,g732)
    c: Coincident(g732,g733)
    c: Coincident(g733,g734)
    c: Coincident(g734,g735)
    c: Coincident(g735,g736)
    c: Coincident(g736,g737)
    c: Coincident(g737,g738)
    c: Coincident(g738,g739)
    c: Coincident(g739,g740)
    c: Coincident(g740,g741)
    c: Coincident(g741,g742)
    c: Coincident(g742,g743)
    c: Coincident(g743,g744)
    c: Coincident(g744,g745)
    c: Coincident(g745,g746)
    c: Coincident(g746,g747)
    c: Coincident(g747,g748)
    c: Coincident(g748,g749)
    c: Coincident(g749,g750)
    c: Coincident(g750,g751)
    c: Coincident(g751,g752)
    c: Coincident(g752,g753)
    c: Coincident(g753,g754)
    c: Coincident(g754,g755)
    c: Coincident(g755,g756)
    c: Coincident(g756,g757)
    c: Coincident(g757,g758)
    c: Coincident(g758,g759)
    c: Coincident(g759,g531)
    c: Coincident(g760,g761)
    c: Coincident(g761,g762)
    c: Coincident(g762,g763)
    c: Coincident(g763,g764)
    c: Coincident(g764,g765)
    c: Coincident(g765,g766)
    c: Coincident(g766,g767)
    c: Coincident(g767,g768)
    c: Coincident(g768,g769)
    c: Coincident(g769,g770)
    c: Coincident(g770,g771)
    c: Coincident(g771,g772)
    c: Coincident(g772,g773)
    c: Coincident(g773,g774)
    c: Coincident(g774,g760)
FEATURE [Sketcher::SketchObject] Sketch022
  ExternalGeometry = -> [Pad011]
  FullyConstrained = true
  MapMode = 5
  Placement = pos=(0,-13.95,3.1e-15) rot=(1,0,0;1.5708rad)
  Support = -> [Pad011]
  sketch-geometry (12):
    g0: LineSegment StartX=-19 StartY=104.35 StartZ=0 EndX=19 EndY=104.35 EndZ=0
    g1: LineSegment StartX=19 StartY=104.35 StartZ=0 EndX=19 EndY=83.1 EndZ=0
    g2: LineSegment StartX=19 StartY=83.1 StartZ=0 EndX=-19 EndY=83.1 EndZ=0
    g3: LineSegment StartX=-19 StartY=83.1 StartZ=0 EndX=-19 EndY=104.35 EndZ=0
    g4: LineSegment StartX=-16.75 StartY=102.1 StartZ=0 EndX=16.75 EndY=102.1 EndZ=0
    g5: LineSegment StartX=16.75 StartY=102.1 StartZ=0 EndX=16.75 EndY=85.35 EndZ=0
    g6: LineSegment StartX=16.75 StartY=85.35 StartZ=0 EndX=-16.75 EndY=85.35 EndZ=0
    g7: LineSegment StartX=-16.75 StartY=85.35 StartZ=0 EndX=-16.75 EndY=102.1 EndZ=0
    g8: LineSegment StartX=-16.75 StartY=102.1 StartZ=0 EndX=-19 EndY=102.1 EndZ=0
    g9: LineSegment StartX=-16.75 StartY=102.1 StartZ=0 EndX=-16.75 EndY=104.35 EndZ=0
    g10: LineSegment StartX=16.75 StartY=85.35 StartZ=0 EndX=16.75 EndY=83.1 EndZ=0
    g11: LineSegment StartX=16.75 StartY=85.35 StartZ=0 EndX=19 EndY=85.35 EndZ=0
  constraints (34):
    c: Coincident(g0,g1)
    c: Coincident(g1,g2)
    c: Coincident(g2,g3)
    c: Coincident(g3,g0)
    c: Horizontal(g0)
    c: Horizontal(g2)
    c: Vertical(g1)
    c: Vertical(g3)
    c: Coincident(g0,g-3)
    c: Coincident(g1,g-5)
    c: Coincident(g4,g5)
    c: Coincident(g5,g6)
    c: Coincident(g6,g7)
    c: Coincident(g7,g4)
    c: Horizontal(g4)
    c: Horizontal(g6)
    c: Vertical(g5)
    c: Vertical(g7)
    c: Coincident(g8,g4)
    c: PointOnObject(g8,g3)
    c: Horizontal(g8)
    c: Coincident(g9,g4)
    c: PointOnObject(g9,g0)
    c: Vertical(g9)
    c: Coincident(g10,g5)
    c: PointOnObject(g10,g2)
    c: Vertical(g10)
    c: Coincident(g11,g5)
    c: PointOnObject(g11,g1)
    c: Horizontal(g11)
    c: Equal(g10,g11)
    c: Equal(g11,g9)
    c: Equal(g9,g8)
    c: DistanceY(g9,g9) = 2.25
FEATURE [PartDesign::Pocket] Pocket001
  BaseFeature = -> Pad011
  Direction = (0,1,-2e-16)
  Length = 0.1
  Length2 = 5
  Profile = -> Sketch022
  ReferenceAxis = -> Sketch022 [N_Axis]
  Type = 0
FEATURE [PartDesign::Body] Body022  label="trunk"
  Group = -> [Binder017,Binder018,Binder019,Sketch011,Pad011,Sketch022,Pocket001]
  Origin = -> Origin025
  Tip = -> Pocket001
FEATURE [App::DocumentObjectGroup] Group002  label="Acrylic_parts"
  Group = -> [Body,Body003,Body004,Body002,Body008,Body009,Body010,Body014,Body007,Body015,Body017,Body018,Body023,Body024,Body022]
FEATURE [Part::Part2DObjectPython] Shape2DView018  label="trunk_DXF"  # Draft 2D object (typed FeaturePython)
  AutoUpdate = true
  Base = -> Body022
  Clip = false
  FuseArch = false
  HiddenLines = false
  InPlace = true
  OnlySolids = false
  Projection = (0,-1,0)
  ProjectionMode = 0
  SegmentLength = 0.05
  Tessellation = false
  VisibleOnly = false
FEATURE [App::DocumentObjectGroup] Group004  label="DXF_acrylic"
  Group = -> [Shape2DView,Shape2DView001,Shape2DView002,Shape2DView003,Shape2DView004,Shape2DView005,Shape2DView006,Shape2DView007,Shape2DView008,Shape2DView009,Shape2DView010,Shape2DView011,Shape2DView012,Shape2DView013,Shape2DView014,Shape2DView015,Shape2DView016,Shape2DView018,Shape2DView019]
FEATURE [Spreadsheet::Sheet] Fasteners_BOM001  label="Fasteners_BOM"
  cells = A1='Type; B1='Qty; A2='DIN967 Screw M3x14; B2=4; A3='DIN967 Screw M3x30; B3=2; A4='ISO4032 Nut M3; B4=8; A5='ISO7045 Screw M2x10; B5=2; A6='ISO7093-1 Washer M3; B6=2; A7='Threaded Rod M3x70; B7=1
